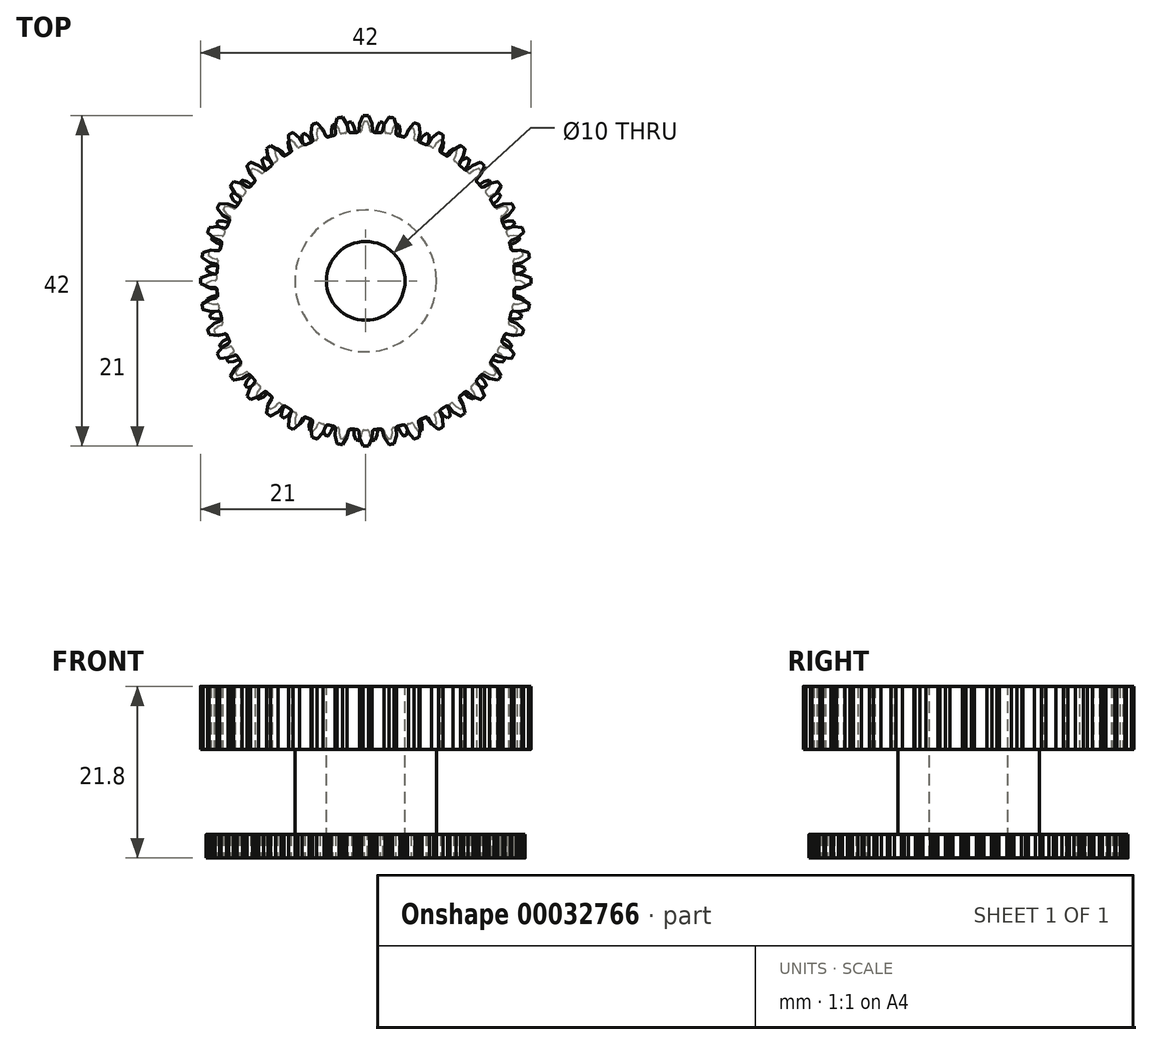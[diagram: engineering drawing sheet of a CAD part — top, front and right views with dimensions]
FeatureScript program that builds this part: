
annotation { "Feature Type Name" : "Feature", "Feature Type Description" : "" }
export const myFeature = defineFeature(function(context is Context, id is Id, definition is map)
    precondition{}
    {
        {
            var Q0;
            Q0=qCreatedBy(makeId("Top.planeOp"),FACE);
            var sketch = newSketch(context, id + "F0", { "sketchPlane" : qUnion([Q0])});
            skArc(sketch, "E0", {"start": v(31.82, 1.48) * mm, "mid": v(31.63, 1.37) * mm, "end": v(31.56, 1.16) * mm});
            skLineSegment(sketch, "E1", {"start": v(31.82, 1.48) * mm, "end": v(32.69, 1.63) * mm});
            skLineSegment(sketch, "E2", {"start": v(32.69, 1.63) * mm, "end": v(33.7, 2.16) * mm});
            skArc(sketch, "E3", {"start": v(31.39, 3.53) * mm, "mid": v(31.34, 3.91) * mm, "end": v(31.29, 4.3) * mm});
            skArc(sketch, "E4", {"start": v(31.81, -1.7) * mm, "mid": v(31.61, -1.79) * mm, "end": v(31.52, -1.99) * mm});
            skArc(sketch, "E5", {"start": v(31.52, 4.64) * mm, "mid": v(31.34, 4.51) * mm, "end": v(31.29, 4.3) * mm});
            skLineSegment(sketch, "E6", {"start": v(31.81, -1.7) * mm, "end": v(32.69, -1.63) * mm});
            skLineSegment(sketch, "E7", {"start": v(31.52, 4.64) * mm, "end": v(32.36, 4.88) * mm});
            skLineSegment(sketch, "E8", {"start": v(32.69, -1.63) * mm, "end": v(33.75, -1.2) * mm});
            skLineSegment(sketch, "E9", {"start": v(32.36, 4.88) * mm, "end": v(33.31, 5.5) * mm});
            skArc(sketch, "E10", {"start": v(30.88, 6.64) * mm, "mid": v(30.8, 7.02) * mm, "end": v(30.7, 7.4) * mm});
            skArc(sketch, "E11", {"start": v(31.49, -4.85) * mm, "mid": v(31.28, -4.93) * mm, "end": v(31.17, -5.12) * mm});
            skArc(sketch, "E12", {"start": v(30.9, 7.76) * mm, "mid": v(30.73, 7.61) * mm, "end": v(30.7, 7.4) * mm});
            skLineSegment(sketch, "E13", {"start": v(31.49, -4.85) * mm, "end": v(32.36, -4.88) * mm});
            skLineSegment(sketch, "E14", {"start": v(30.9, 7.76) * mm, "end": v(31.71, 8.07) * mm});
            skLineSegment(sketch, "E15", {"start": v(32.36, -4.88) * mm, "end": v(33.46, -4.56) * mm});
            skLineSegment(sketch, "E16", {"start": v(31.71, 8.07) * mm, "end": v(32.6, 8.8) * mm});
            skArc(sketch, "E17", {"start": v(30.06, 9.68) * mm, "mid": v(29.94, 10.05) * mm, "end": v(29.81, 10.41) * mm});
            skArc(sketch, "E18", {"start": v(30.85, -7.97) * mm, "mid": v(30.64, -8.02) * mm, "end": v(30.5, -8.2) * mm});
            skArc(sketch, "E19", {"start": v(29.97, 10.8) * mm, "mid": v(29.82, 10.63) * mm, "end": v(29.81, 10.41) * mm});
            skLineSegment(sketch, "E20", {"start": v(30.85, -7.97) * mm, "end": v(31.72, -8.08) * mm});
            skLineSegment(sketch, "E21", {"start": v(29.97, 10.8) * mm, "end": v(30.75, 11.2) * mm});
            skLineSegment(sketch, "E22", {"start": v(31.72, -8.08) * mm, "end": v(32.84, -7.86) * mm});
            skLineSegment(sketch, "E23", {"start": v(30.75, 11.2) * mm, "end": v(31.56, 12) * mm});
            skArc(sketch, "E24", {"start": v(28.95, 12.62) * mm, "mid": v(28.8, 12.98) * mm, "end": v(28.63, 13.33) * mm});
            skArc(sketch, "E25", {"start": v(29.9, -11) * mm, "mid": v(29.69, -11.03) * mm, "end": v(29.54, -11.2) * mm});
            skArc(sketch, "E26", {"start": v(28.74, 13.72) * mm, "mid": v(28.61, 13.55) * mm, "end": v(28.63, 13.33) * mm});
            skLineSegment(sketch, "E27", {"start": v(29.9, -11) * mm, "end": v(30.76, -11.2) * mm});
            skLineSegment(sketch, "E28", {"start": v(28.74, 13.72) * mm, "end": v(29.48, 14.2) * mm});
            skLineSegment(sketch, "E29", {"start": v(30.76, -11.2) * mm, "end": v(31.9, -11.1) * mm});
            skLineSegment(sketch, "E30", {"start": v(29.48, 14.2) * mm, "end": v(30.2, 15.08) * mm});
            skArc(sketch, "E31", {"start": v(27.55, 15.44) * mm, "mid": v(27.35, 15.78) * mm, "end": v(27.16, 16.11) * mm});
            skArc(sketch, "E32", {"start": v(28.66, -13.92) * mm, "mid": v(28.44, -13.93) * mm, "end": v(28.28, -14.08) * mm});
            skArc(sketch, "E33", {"start": v(27.23, 16.52) * mm, "mid": v(27.12, 16.33) * mm, "end": v(27.16, 16.11) * mm});
            skLineSegment(sketch, "E34", {"start": v(28.66, -13.92) * mm, "end": v(29.5, -14.2) * mm});
            skLineSegment(sketch, "E35", {"start": v(27.23, 16.52) * mm, "end": v(27.92, 17.06) * mm});
            skLineSegment(sketch, "E36", {"start": v(29.5, -14.2) * mm, "end": v(30.64, -14.22) * mm});
            skLineSegment(sketch, "E37", {"start": v(27.92, 17.06) * mm, "end": v(28.55, 18.02) * mm});
            skArc(sketch, "E38", {"start": v(25.87, 18.1) * mm, "mid": v(25.65, 18.42) * mm, "end": v(25.42, 18.74) * mm});
            skArc(sketch, "E39", {"start": v(27.13, -16.7) * mm, "mid": v(26.92, -16.69) * mm, "end": v(26.74, -16.82) * mm});
            skArc(sketch, "E40", {"start": v(25.45, 19.15) * mm, "mid": v(25.36, 18.95) * mm, "end": v(25.42, 18.74) * mm});
            skLineSegment(sketch, "E41", {"start": v(27.13, -16.7) * mm, "end": v(27.93, -17.07) * mm});
            skLineSegment(sketch, "E42", {"start": v(25.45, 19.15) * mm, "end": v(26.08, 19.76) * mm});
            skLineSegment(sketch, "E43", {"start": v(27.93, -17.07) * mm, "end": v(29.07, -17.2) * mm});
            skLineSegment(sketch, "E44", {"start": v(26.08, 19.76) * mm, "end": v(26.62, 20.77) * mm});
            skArc(sketch, "E45", {"start": v(23.94, 20.6) * mm, "mid": v(23.68, 20.89) * mm, "end": v(23.42, 21.18) * mm});
            skArc(sketch, "E46", {"start": v(25.34, -19.32) * mm, "mid": v(25.12, -19.29) * mm, "end": v(24.93, -19.4) * mm});
            skArc(sketch, "E47", {"start": v(23.42, 21.59) * mm, "mid": v(23.34, 21.38) * mm, "end": v(23.42, 21.18) * mm});
            skLineSegment(sketch, "E48", {"start": v(25.34, -19.32) * mm, "end": v(26.1, -19.77) * mm});
            skLineSegment(sketch, "E49", {"start": v(23.42, 21.59) * mm, "end": v(23.98, 22.26) * mm});
            skLineSegment(sketch, "E50", {"start": v(26.1, -19.77) * mm, "end": v(27.21, -20) * mm});
            skLineSegment(sketch, "E51", {"start": v(23.98, 22.26) * mm, "end": v(24.41, 23.32) * mm});
            skArc(sketch, "E52", {"start": v(21.77, 22.88) * mm, "mid": v(21.48, 23.14) * mm, "end": v(21.2, 23.4) * mm});
            skArc(sketch, "E53", {"start": v(23.29, -21.75) * mm, "mid": v(23.08, -21.7) * mm, "end": v(22.88, -21.79) * mm});
            skArc(sketch, "E54", {"start": v(21.15, 23.81) * mm, "mid": v(21.1, 23.6) * mm, "end": v(21.2, 23.4) * mm});
            skLineSegment(sketch, "E55", {"start": v(23.29, -21.75) * mm, "end": v(24, -22.27) * mm});
            skLineSegment(sketch, "E56", {"start": v(21.15, 23.81) * mm, "end": v(21.65, 24.53) * mm});
            skLineSegment(sketch, "E57", {"start": v(24, -22.27) * mm, "end": v(25.09, -22.62) * mm});
            skLineSegment(sketch, "E58", {"start": v(21.65, 24.53) * mm, "end": v(21.97, 25.63) * mm});
            skArc(sketch, "E59", {"start": v(19.38, 24.93) * mm, "mid": v(19.07, 25.16) * mm, "end": v(18.76, 25.4) * mm});
            skArc(sketch, "E60", {"start": v(21, -23.96) * mm, "mid": v(20.8, -23.88) * mm, "end": v(20.6, -23.96) * mm});
            skArc(sketch, "E61", {"start": v(18.67, 25.8) * mm, "mid": v(18.64, 25.58) * mm, "end": v(18.76, 25.4) * mm});
            skLineSegment(sketch, "E62", {"start": v(21, -23.96) * mm, "end": v(21.66, -24.55) * mm});
            skLineSegment(sketch, "E63", {"start": v(18.67, 25.8) * mm, "end": v(19.1, 26.57) * mm});
            skLineSegment(sketch, "E64", {"start": v(21.66, -24.55) * mm, "end": v(22.71, -25) * mm});
            skLineSegment(sketch, "E65", {"start": v(19.1, 26.57) * mm, "end": v(19.3, 27.7) * mm});
            skArc(sketch, "E66", {"start": v(16.8, 26.73) * mm, "mid": v(16.47, 26.94) * mm, "end": v(16.14, 27.14) * mm});
            skArc(sketch, "E67", {"start": v(18.52, -25.93) * mm, "mid": v(18.32, -25.84) * mm, "end": v(18.11, -25.89) * mm});
            skArc(sketch, "E68", {"start": v(16.01, 27.53) * mm, "mid": v(16, 27.3) * mm, "end": v(16.14, 27.14) * mm});
            skLineSegment(sketch, "E69", {"start": v(18.52, -25.93) * mm, "end": v(19.11, -26.58) * mm});
            skLineSegment(sketch, "E70", {"start": v(16.01, 27.53) * mm, "end": v(16.35, 28.34) * mm});
            skLineSegment(sketch, "E71", {"start": v(19.11, -26.58) * mm, "end": v(20.11, -27.14) * mm});
            skLineSegment(sketch, "E72", {"start": v(16.35, 28.34) * mm, "end": v(16.45, 29.47) * mm});
            skArc(sketch, "E73", {"start": v(14.05, 28.27) * mm, "mid": v(13.7, 28.44) * mm, "end": v(13.35, 28.61) * mm});
            skArc(sketch, "E74", {"start": v(15.85, -27.65) * mm, "mid": v(15.66, -27.53) * mm, "end": v(15.45, -27.56) * mm});
            skArc(sketch, "E75", {"start": v(13.19, 28.99) * mm, "mid": v(13.2, 28.77) * mm, "end": v(13.35, 28.61) * mm});
            skLineSegment(sketch, "E76", {"start": v(15.85, -27.65) * mm, "end": v(16.37, -28.35) * mm});
            skLineSegment(sketch, "E77", {"start": v(13.19, 28.99) * mm, "end": v(13.45, 29.82) * mm});
            skLineSegment(sketch, "E78", {"start": v(16.37, -28.35) * mm, "end": v(17.31, -29) * mm});
            skLineSegment(sketch, "E79", {"start": v(13.45, 29.82) * mm, "end": v(13.44, 30.97) * mm});
            skArc(sketch, "E80", {"start": v(11.17, 29.53) * mm, "mid": v(10.8, 29.67) * mm, "end": v(10.44, 29.8) * mm});
            skArc(sketch, "E81", {"start": v(13.02, -29.1) * mm, "mid": v(12.84, -28.95) * mm, "end": v(12.63, -28.97) * mm});
            skArc(sketch, "E82", {"start": v(10.24, 30.16) * mm, "mid": v(10.27, 29.94) * mm, "end": v(10.44, 29.8) * mm});
            skLineSegment(sketch, "E83", {"start": v(13.02, -29.1) * mm, "end": v(13.47, -29.84) * mm});
            skLineSegment(sketch, "E84", {"start": v(10.24, 30.16) * mm, "end": v(10.41, 31.01) * mm});
            skLineSegment(sketch, "E85", {"start": v(13.47, -29.84) * mm, "end": v(14.34, -30.59) * mm});
            skLineSegment(sketch, "E86", {"start": v(10.41, 31.01) * mm, "end": v(10.28, 32.15) * mm});
            skArc(sketch, "E87", {"start": v(8.17, 30.5) * mm, "mid": v(7.8, 30.6) * mm, "end": v(7.42, 30.69) * mm});
            skArc(sketch, "E88", {"start": v(10.06, -30.24) * mm, "mid": v(9.9, -30.09) * mm, "end": v(9.68, -30.08) * mm});
            skArc(sketch, "E89", {"start": v(7.18, 31.02) * mm, "mid": v(7.24, 30.81) * mm, "end": v(7.42, 30.69) * mm});
            skLineSegment(sketch, "E90", {"start": v(10.06, -30.24) * mm, "end": v(10.43, -31.03) * mm});
            skLineSegment(sketch, "E91", {"start": v(7.18, 31.02) * mm, "end": v(7.27, 31.9) * mm});
            skLineSegment(sketch, "E92", {"start": v(10.43, -31.03) * mm, "end": v(11.22, -31.86) * mm});
            skLineSegment(sketch, "E93", {"start": v(7.27, 31.9) * mm, "end": v(7.03, 33.01) * mm});
            skArc(sketch, "E94", {"start": v(5.1, 31.16) * mm, "mid": v(4.7, 31.22) * mm, "end": v(4.32, 31.27) * mm});
            skArc(sketch, "E95", {"start": v(7, -31.1) * mm, "mid": v(6.86, -30.93) * mm, "end": v(6.64, -30.9) * mm});
            skArc(sketch, "E96", {"start": v(4.05, 31.59) * mm, "mid": v(4.13, 31.38) * mm, "end": v(4.32, 31.27) * mm});
            skLineSegment(sketch, "E97", {"start": v(7, -31.1) * mm, "end": v(7.3, -31.92) * mm});
            skLineSegment(sketch, "E98", {"start": v(4.05, 31.59) * mm, "end": v(4.06, 32.46) * mm});
            skLineSegment(sketch, "E99", {"start": v(7.3, -31.92) * mm, "end": v(8, -32.82) * mm});
            skLineSegment(sketch, "E100", {"start": v(4.06, 32.46) * mm, "end": v(3.7, 33.55) * mm});
            skArc(sketch, "E101", {"start": v(1.96, 31.51) * mm, "mid": v(1.57, 31.53) * mm, "end": v(1.19, 31.55) * mm});
            skArc(sketch, "E102", {"start": v(3.87, -31.64) * mm, "mid": v(3.74, -31.45) * mm, "end": v(3.53, -31.4) * mm});
            skArc(sketch, "E103", {"start": v(0.89, 31.83) * mm, "mid": v(0.98, 31.63) * mm, "end": v(1.19, 31.55) * mm});
            skLineSegment(sketch, "E104", {"start": v(3.87, -31.64) * mm, "end": v(4.08, -32.49) * mm});
            skLineSegment(sketch, "E105", {"start": v(0.89, 31.83) * mm, "end": v(0.8, 32.7) * mm});
            skLineSegment(sketch, "E106", {"start": v(4.08, -32.49) * mm, "end": v(4.69, -33.45) * mm});
            skLineSegment(sketch, "E107", {"start": v(0.8, 32.7) * mm, "end": v(0.35, 33.75) * mm});
            skArc(sketch, "E108", {"start": v(-1.19, 31.55) * mm, "mid": v(-1.57, 31.53) * mm, "end": v(-1.96, 31.51) * mm});
            skArc(sketch, "E109", {"start": v(0.7, -31.86) * mm, "mid": v(0.6, -31.67) * mm, "end": v(0.39, -31.6) * mm});
            skArc(sketch, "E110", {"start": v(-2.29, 31.76) * mm, "mid": v(-2.17, 31.58) * mm, "end": v(-1.96, 31.51) * mm});
            skLineSegment(sketch, "E111", {"start": v(0.7, -31.86) * mm, "end": v(0.83, -32.73) * mm});
            skLineSegment(sketch, "E112", {"start": v(-2.29, 31.76) * mm, "end": v(-2.46, 32.62) * mm});
            skLineSegment(sketch, "E113", {"start": v(0.83, -32.73) * mm, "end": v(1.34, -33.75) * mm});
            skLineSegment(sketch, "E114", {"start": v(-2.46, 32.62) * mm, "end": v(-3.02, 33.62) * mm});
            skArc(sketch, "E115", {"start": v(-4.32, 31.27) * mm, "mid": v(-4.7, 31.22) * mm, "end": v(-5.1, 31.16) * mm});
            skArc(sketch, "E116", {"start": v(-2.47, -31.77) * mm, "mid": v(-2.56, -31.57) * mm, "end": v(-2.76, -31.48) * mm});
            skArc(sketch, "E117", {"start": v(-5.44, 31.38) * mm, "mid": v(-5.3, 31.2) * mm, "end": v(-5.1, 31.16) * mm});
            skLineSegment(sketch, "E118", {"start": v(-2.47, -31.77) * mm, "end": v(-2.44, -32.65) * mm});
            skLineSegment(sketch, "E119", {"start": v(-5.44, 31.38) * mm, "end": v(-5.7, 32.22) * mm});
            skLineSegment(sketch, "E120", {"start": v(-2.44, -32.65) * mm, "end": v(-2.03, -33.72) * mm});
            skLineSegment(sketch, "E121", {"start": v(-5.7, 32.22) * mm, "end": v(-6.35, 33.15) * mm});
            skArc(sketch, "E122", {"start": v(-7.42, 30.69) * mm, "mid": v(-7.8, 30.6) * mm, "end": v(-8.17, 30.5) * mm});
            skArc(sketch, "E123", {"start": v(-5.62, -31.37) * mm, "mid": v(-5.7, -31.16) * mm, "end": v(-5.88, -31.05) * mm});
            skArc(sketch, "E124", {"start": v(-8.54, 30.68) * mm, "mid": v(-8.39, 30.52) * mm, "end": v(-8.17, 30.5) * mm});
            skLineSegment(sketch, "E125", {"start": v(-5.62, -31.37) * mm, "end": v(-5.67, -32.25) * mm});
            skLineSegment(sketch, "E126", {"start": v(-8.54, 30.68) * mm, "end": v(-8.87, 31.49) * mm});
            skLineSegment(sketch, "E127", {"start": v(-5.67, -32.25) * mm, "end": v(-5.38, -33.35) * mm});
            skLineSegment(sketch, "E128", {"start": v(-8.87, 31.49) * mm, "end": v(-9.62, 32.35) * mm});
            skArc(sketch, "E129", {"start": v(-10.44, 29.8) * mm, "mid": v(-10.8, 29.67) * mm, "end": v(-11.17, 29.53) * mm});
            skArc(sketch, "E130", {"start": v(-8.72, -30.65) * mm, "mid": v(-8.76, -30.44) * mm, "end": v(-8.94, -30.3) * mm});
            skArc(sketch, "E131", {"start": v(-11.55, 29.68) * mm, "mid": v(-11.39, 29.53) * mm, "end": v(-11.17, 29.53) * mm});
            skLineSegment(sketch, "E132", {"start": v(-8.72, -30.65) * mm, "end": v(-8.85, -31.52) * mm});
            skLineSegment(sketch, "E133", {"start": v(-11.55, 29.68) * mm, "end": v(-11.97, 30.45) * mm});
            skLineSegment(sketch, "E134", {"start": v(-8.85, -31.52) * mm, "end": v(-8.67, -32.65) * mm});
            skLineSegment(sketch, "E135", {"start": v(-11.97, 30.45) * mm, "end": v(-12.8, 31.24) * mm});
            skArc(sketch, "E136", {"start": v(-13.35, 28.61) * mm, "mid": v(-13.7, 28.44) * mm, "end": v(-14.05, 28.27) * mm});
            skArc(sketch, "E137", {"start": v(-11.73, -29.63) * mm, "mid": v(-11.75, -29.42) * mm, "end": v(-11.91, -29.27) * mm});
            skArc(sketch, "E138", {"start": v(-14.45, 28.38) * mm, "mid": v(-14.27, 28.25) * mm, "end": v(-14.05, 28.27) * mm});
            skLineSegment(sketch, "E139", {"start": v(-11.73, -29.63) * mm, "end": v(-11.95, -30.48) * mm});
            skLineSegment(sketch, "E140", {"start": v(-14.45, 28.38) * mm, "end": v(-14.94, 29.1) * mm});
            skLineSegment(sketch, "E141", {"start": v(-11.95, -30.48) * mm, "end": v(-11.87, -31.62) * mm});
            skLineSegment(sketch, "E142", {"start": v(-14.94, 29.1) * mm, "end": v(-15.84, 29.8) * mm});
            skArc(sketch, "E143", {"start": v(-16.14, 27.14) * mm, "mid": v(-16.47, 26.94) * mm, "end": v(-16.8, 26.73) * mm});
            skArc(sketch, "E144", {"start": v(-14.62, -28.32) * mm, "mid": v(-14.62, -28.1) * mm, "end": v(-14.76, -27.94) * mm});
            skArc(sketch, "E145", {"start": v(-17.2, 26.8) * mm, "mid": v(-17.01, 26.7) * mm, "end": v(-16.8, 26.73) * mm});
            skLineSegment(sketch, "E146", {"start": v(-14.62, -28.32) * mm, "end": v(-14.92, -29.14) * mm});
            skLineSegment(sketch, "E147", {"start": v(-17.2, 26.8) * mm, "end": v(-17.77, 27.47) * mm});
            skLineSegment(sketch, "E148", {"start": v(-14.92, -29.14) * mm, "end": v(-14.96, -30.28) * mm});
            skLineSegment(sketch, "E149", {"start": v(-17.77, 27.47) * mm, "end": v(-18.73, 28.08) * mm});
            skArc(sketch, "E150", {"start": v(-18.76, 25.4) * mm, "mid": v(-19.07, 25.16) * mm, "end": v(-19.38, 24.93) * mm});
            skArc(sketch, "E151", {"start": v(-17.36, -26.72) * mm, "mid": v(-17.34, -26.5) * mm, "end": v(-17.47, -26.33) * mm});
            skArc(sketch, "E152", {"start": v(-19.79, 24.95) * mm, "mid": v(-19.59, 24.86) * mm, "end": v(-19.38, 24.93) * mm});
            skLineSegment(sketch, "E153", {"start": v(-17.36, -26.72) * mm, "end": v(-17.75, -27.51) * mm});
            skLineSegment(sketch, "E154", {"start": v(-19.79, 24.95) * mm, "end": v(-20.41, 25.57) * mm});
            skLineSegment(sketch, "E155", {"start": v(-17.75, -27.51) * mm, "end": v(-17.9, -28.64) * mm});
            skLineSegment(sketch, "E156", {"start": v(-20.41, 25.57) * mm, "end": v(-21.44, 26.08) * mm});
            skArc(sketch, "E157", {"start": v(-21.2, 23.4) * mm, "mid": v(-21.48, 23.14) * mm, "end": v(-21.77, 22.88) * mm});
            skArc(sketch, "E158", {"start": v(-19.94, -24.86) * mm, "mid": v(-19.9, -24.65) * mm, "end": v(-20, -24.46) * mm});
            skArc(sketch, "E159", {"start": v(-22.18, 22.86) * mm, "mid": v(-21.97, 22.79) * mm, "end": v(-21.77, 22.88) * mm});
            skLineSegment(sketch, "E160", {"start": v(-19.94, -24.86) * mm, "end": v(-20.4, -25.6) * mm});
            skLineSegment(sketch, "E161", {"start": v(-22.18, 22.86) * mm, "end": v(-22.86, 23.4) * mm});
            skLineSegment(sketch, "E162", {"start": v(-20.4, -25.6) * mm, "end": v(-20.66, -26.72) * mm});
            skLineSegment(sketch, "E163", {"start": v(-22.86, 23.4) * mm, "end": v(-23.93, 23.81) * mm});
            skArc(sketch, "E164", {"start": v(-23.42, 21.18) * mm, "mid": v(-23.68, 20.89) * mm, "end": v(-23.94, 20.6) * mm});
            skArc(sketch, "E165", {"start": v(-22.31, -22.75) * mm, "mid": v(-22.25, -22.54) * mm, "end": v(-22.34, -22.34) * mm});
            skArc(sketch, "E166", {"start": v(-24.34, 20.54) * mm, "mid": v(-24.13, 20.49) * mm, "end": v(-23.94, 20.6) * mm});
            skLineSegment(sketch, "E167", {"start": v(-22.31, -22.75) * mm, "end": v(-22.84, -23.45) * mm});
            skLineSegment(sketch, "E168", {"start": v(-24.34, 20.54) * mm, "end": v(-25.08, 21.02) * mm});
            skLineSegment(sketch, "E169", {"start": v(-22.84, -23.45) * mm, "end": v(-23.22, -24.53) * mm});
            skLineSegment(sketch, "E170", {"start": v(-25.08, 21.02) * mm, "end": v(-26.18, 21.31) * mm});
            skArc(sketch, "E171", {"start": v(-25.42, 18.74) * mm, "mid": v(-25.65, 18.42) * mm, "end": v(-25.87, 18.1) * mm});
            skArc(sketch, "E172", {"start": v(-24.46, -20.42) * mm, "mid": v(-24.38, -20.22) * mm, "end": v(-24.45, -20) * mm});
            skArc(sketch, "E173", {"start": v(-26.27, 18.01) * mm, "mid": v(-26.05, 17.98) * mm, "end": v(-25.87, 18.1) * mm});
            skLineSegment(sketch, "E174", {"start": v(-24.46, -20.42) * mm, "end": v(-25.06, -21.06) * mm});
            skLineSegment(sketch, "E175", {"start": v(-26.27, 18.01) * mm, "end": v(-27.05, 18.41) * mm});
            skLineSegment(sketch, "E176", {"start": v(-25.06, -21.06) * mm, "end": v(-25.55, -22.1) * mm});
            skLineSegment(sketch, "E177", {"start": v(-27.05, 18.41) * mm, "end": v(-28.18, 18.6) * mm});
            skArc(sketch, "E178", {"start": v(-27.16, 16.11) * mm, "mid": v(-27.35, 15.78) * mm, "end": v(-27.55, 15.44) * mm});
            skArc(sketch, "E179", {"start": v(-26.37, -17.88) * mm, "mid": v(-26.27, -17.69) * mm, "end": v(-26.32, -17.47) * mm});
            skArc(sketch, "E180", {"start": v(-27.93, 15.3) * mm, "mid": v(-27.71, 15.3) * mm, "end": v(-27.55, 15.44) * mm});
            skLineSegment(sketch, "E181", {"start": v(-26.37, -17.88) * mm, "end": v(-27.04, -18.46) * mm});
            skLineSegment(sketch, "E182", {"start": v(-27.93, 15.3) * mm, "end": v(-28.75, 15.63) * mm});
            skLineSegment(sketch, "E183", {"start": v(-27.04, -18.46) * mm, "end": v(-27.62, -19.44) * mm});
            skLineSegment(sketch, "E184", {"start": v(-28.75, 15.63) * mm, "end": v(-29.89, 15.7) * mm});
            skArc(sketch, "E185", {"start": v(-28.63, 13.33) * mm, "mid": v(-28.8, 12.98) * mm, "end": v(-28.95, 12.62) * mm});
            skArc(sketch, "E186", {"start": v(-28.02, -15.17) * mm, "mid": v(-27.9, -14.98) * mm, "end": v(-27.93, -14.77) * mm});
            skArc(sketch, "E187", {"start": v(-29.32, 12.45) * mm, "mid": v(-29.1, 12.47) * mm, "end": v(-28.95, 12.62) * mm});
            skLineSegment(sketch, "E188", {"start": v(-28.02, -15.17) * mm, "end": v(-28.74, -15.68) * mm});
            skLineSegment(sketch, "E189", {"start": v(-29.32, 12.45) * mm, "end": v(-30.16, 12.69) * mm});
            skLineSegment(sketch, "E190", {"start": v(-28.74, -15.68) * mm, "end": v(-29.42, -16.6) * mm});
            skLineSegment(sketch, "E191", {"start": v(-30.16, 12.69) * mm, "end": v(-31.3, 12.65) * mm});
            skArc(sketch, "E192", {"start": v(-29.82, 10.41) * mm, "mid": v(-29.94, 10.05) * mm, "end": v(-30.06, 9.68) * mm});
            skArc(sketch, "E193", {"start": v(-29.4, -12.3) * mm, "mid": v(-29.25, -12.13) * mm, "end": v(-29.26, -11.91) * mm});
            skArc(sketch, "E194", {"start": v(-30.41, 9.47) * mm, "mid": v(-30.2, 9.5) * mm, "end": v(-30.06, 9.68) * mm});
            skLineSegment(sketch, "E195", {"start": v(-29.4, -12.3) * mm, "end": v(-30.15, -12.74) * mm});
            skLineSegment(sketch, "E196", {"start": v(-30.41, 9.47) * mm, "end": v(-31.28, 9.62) * mm});
            skLineSegment(sketch, "E197", {"start": v(-30.15, -12.74) * mm, "end": v(-30.92, -13.58) * mm});
            skLineSegment(sketch, "E198", {"start": v(-31.28, 9.62) * mm, "end": v(-32.4, 9.47) * mm});
            skArc(sketch, "E199", {"start": v(-30.7, 7.4) * mm, "mid": v(-30.8, 7.02) * mm, "end": v(-30.88, 6.64) * mm});
            skArc(sketch, "E200", {"start": v(-30.47, -9.31) * mm, "mid": v(-30.31, -9.16) * mm, "end": v(-30.3, -8.94) * mm});
            skArc(sketch, "E201", {"start": v(-31.2, 6.4) * mm, "mid": v(-31, 6.45) * mm, "end": v(-30.88, 6.64) * mm});
            skLineSegment(sketch, "E202", {"start": v(-30.47, -9.31) * mm, "end": v(-31.27, -9.67) * mm});
            skLineSegment(sketch, "E203", {"start": v(-31.2, 6.4) * mm, "end": v(-32.08, 6.46) * mm});
            skLineSegment(sketch, "E204", {"start": v(-31.27, -9.67) * mm, "end": v(-32.12, -10.44) * mm});
            skLineSegment(sketch, "E205", {"start": v(-32.08, 6.46) * mm, "end": v(-33.2, 6.2) * mm});
            skArc(sketch, "E206", {"start": v(-31.29, 4.3) * mm, "mid": v(-31.34, 3.91) * mm, "end": v(-31.39, 3.53) * mm});
            skArc(sketch, "E207", {"start": v(-31.24, -6.23) * mm, "mid": v(-31.07, -6.1) * mm, "end": v(-31.04, -5.88) * mm});
            skArc(sketch, "E208", {"start": v(-31.69, 3.25) * mm, "mid": v(-31.49, 3.33) * mm, "end": v(-31.39, 3.53) * mm});
            skLineSegment(sketch, "E209", {"start": v(-31.24, -6.23) * mm, "end": v(-32.08, -6.5) * mm});
            skLineSegment(sketch, "E210", {"start": v(-31.69, 3.25) * mm, "end": v(-32.57, 3.23) * mm});
            skLineSegment(sketch, "E211", {"start": v(-32.08, -6.5) * mm, "end": v(-33, -7.19) * mm});
            skLineSegment(sketch, "E212", {"start": v(-32.57, 3.23) * mm, "end": v(-33.65, 2.86) * mm});
            skArc(sketch, "E213", {"start": v(-31.7, -3.1) * mm, "mid": v(-31.52, -2.97) * mm, "end": v(-31.47, -2.76) * mm});
            skArc(sketch, "E214", {"start": v(-31.56, 1.16) * mm, "mid": v(-31.58, 0.77) * mm, "end": v(-31.58, 0.39) * mm});
            skLineSegment(sketch, "E215", {"start": v(-31.7, -3.1) * mm, "end": v(-32.56, -3.28) * mm});
            skArc(sketch, "E216", {"start": v(-31.86, 0.08) * mm, "mid": v(-31.66, 0.18) * mm, "end": v(-31.58, 0.39) * mm});
            skLineSegment(sketch, "E217", {"start": v(-32.56, -3.28) * mm, "end": v(-33.55, -3.87) * mm});
            skLineSegment(sketch, "E218", {"start": v(-31.86, 0.08) * mm, "end": v(-32.73, -0.02) * mm});
            skLineSegment(sketch, "E219", {"start": v(-32.73, -0.02) * mm, "end": v(-33.76, -0.5) * mm});
            skLineSegment(sketch, "E220", {"start": v(-33.75, -1.2) * mm, "end": v(-32.69, -1.63) * mm});
            skLineSegment(sketch, "E221", {"start": v(-32.69, -1.63) * mm, "end": v(-31.81, -1.7) * mm});
            skArc(sketch, "E222", {"start": v(-31.52, -1.99) * mm, "mid": v(-31.61, -1.79) * mm, "end": v(-31.81, -1.7) * mm});
            skArc(sketch, "E223", {"start": v(-31.52, -1.99) * mm, "mid": v(-31.5, -2.37) * mm, "end": v(-31.47, -2.76) * mm});
            skLineSegment(sketch, "E224", {"start": v(-33.46, -4.56) * mm, "end": v(-32.36, -4.88) * mm});
            skLineSegment(sketch, "E225", {"start": v(-32.36, -4.88) * mm, "end": v(-31.49, -4.85) * mm});
            skArc(sketch, "E226", {"start": v(-31.17, -5.12) * mm, "mid": v(-31.28, -4.93) * mm, "end": v(-31.49, -4.85) * mm});
            skArc(sketch, "E227", {"start": v(-31.17, -5.12) * mm, "mid": v(-31.1, -5.5) * mm, "end": v(-31.04, -5.88) * mm});
            skLineSegment(sketch, "E228", {"start": v(-32.84, -7.86) * mm, "end": v(-31.72, -8.08) * mm});
            skLineSegment(sketch, "E229", {"start": v(-31.72, -8.08) * mm, "end": v(-30.85, -7.97) * mm});
            skArc(sketch, "E230", {"start": v(-30.5, -8.2) * mm, "mid": v(-30.64, -8.02) * mm, "end": v(-30.85, -7.97) * mm});
            skArc(sketch, "E231", {"start": v(-30.5, -8.2) * mm, "mid": v(-30.4, -8.57) * mm, "end": v(-30.3, -8.94) * mm});
            skLineSegment(sketch, "E232", {"start": v(-31.9, -11.1) * mm, "end": v(-30.76, -11.2) * mm});
            skLineSegment(sketch, "E233", {"start": v(-30.76, -11.2) * mm, "end": v(-29.9, -11) * mm});
            skArc(sketch, "E234", {"start": v(-29.54, -11.2) * mm, "mid": v(-29.69, -11.03) * mm, "end": v(-29.9, -11) * mm});
            skArc(sketch, "E235", {"start": v(-29.54, -11.2) * mm, "mid": v(-29.4, -11.55) * mm, "end": v(-29.26, -11.91) * mm});
            skLineSegment(sketch, "E236", {"start": v(-30.64, -14.22) * mm, "end": v(-29.5, -14.2) * mm});
            skLineSegment(sketch, "E237", {"start": v(-29.5, -14.2) * mm, "end": v(-28.66, -13.92) * mm});
            skArc(sketch, "E238", {"start": v(-28.28, -14.08) * mm, "mid": v(-28.44, -13.93) * mm, "end": v(-28.66, -13.92) * mm});
            skArc(sketch, "E239", {"start": v(-28.28, -14.08) * mm, "mid": v(-28.1, -14.42) * mm, "end": v(-27.93, -14.77) * mm});
            skLineSegment(sketch, "E240", {"start": v(-29.07, -17.2) * mm, "end": v(-27.93, -17.07) * mm});
            skLineSegment(sketch, "E241", {"start": v(-27.93, -17.07) * mm, "end": v(-27.13, -16.7) * mm});
            skArc(sketch, "E242", {"start": v(-26.74, -16.82) * mm, "mid": v(-26.92, -16.69) * mm, "end": v(-27.13, -16.7) * mm});
            skArc(sketch, "E243", {"start": v(-26.74, -16.82) * mm, "mid": v(-26.53, -17.15) * mm, "end": v(-26.32, -17.47) * mm});
            skLineSegment(sketch, "E244", {"start": v(-27.21, -20) * mm, "end": v(-26.1, -19.77) * mm});
            skLineSegment(sketch, "E245", {"start": v(-26.1, -19.77) * mm, "end": v(-25.34, -19.32) * mm});
            skArc(sketch, "E246", {"start": v(-24.93, -19.4) * mm, "mid": v(-25.12, -19.29) * mm, "end": v(-25.34, -19.32) * mm});
            skArc(sketch, "E247", {"start": v(-24.93, -19.4) * mm, "mid": v(-24.7, -19.7) * mm, "end": v(-24.45, -20) * mm});
            skLineSegment(sketch, "E248", {"start": v(-25.09, -22.62) * mm, "end": v(-24, -22.27) * mm});
            skLineSegment(sketch, "E249", {"start": v(-24, -22.27) * mm, "end": v(-23.29, -21.75) * mm});
            skArc(sketch, "E250", {"start": v(-22.88, -21.79) * mm, "mid": v(-23.08, -21.7) * mm, "end": v(-23.29, -21.75) * mm});
            skArc(sketch, "E251", {"start": v(-22.88, -21.79) * mm, "mid": v(-22.61, -22.07) * mm, "end": v(-22.34, -22.34) * mm});
            skLineSegment(sketch, "E252", {"start": v(-22.71, -25) * mm, "end": v(-21.66, -24.55) * mm});
            skLineSegment(sketch, "E253", {"start": v(-21.66, -24.55) * mm, "end": v(-21, -23.96) * mm});
            skArc(sketch, "E254", {"start": v(-20.6, -23.96) * mm, "mid": v(-20.8, -23.88) * mm, "end": v(-21, -23.96) * mm});
            skArc(sketch, "E255", {"start": v(-20.6, -23.96) * mm, "mid": v(-20.3, -24.2) * mm, "end": v(-20, -24.46) * mm});
            skLineSegment(sketch, "E256", {"start": v(-20.11, -27.14) * mm, "end": v(-19.11, -26.58) * mm});
            skLineSegment(sketch, "E257", {"start": v(-19.11, -26.58) * mm, "end": v(-18.52, -25.93) * mm});
            skArc(sketch, "E258", {"start": v(-18.11, -25.89) * mm, "mid": v(-18.32, -25.84) * mm, "end": v(-18.52, -25.93) * mm});
            skArc(sketch, "E259", {"start": v(-18.11, -25.89) * mm, "mid": v(-17.8, -26.11) * mm, "end": v(-17.47, -26.33) * mm});
            skLineSegment(sketch, "E260", {"start": v(-17.31, -29) * mm, "end": v(-16.37, -28.35) * mm});
            skLineSegment(sketch, "E261", {"start": v(-16.37, -28.35) * mm, "end": v(-15.85, -27.65) * mm});
            skArc(sketch, "E262", {"start": v(-15.45, -27.56) * mm, "mid": v(-15.66, -27.53) * mm, "end": v(-15.85, -27.65) * mm});
            skArc(sketch, "E263", {"start": v(-15.45, -27.56) * mm, "mid": v(-15.1, -27.75) * mm, "end": v(-14.76, -27.94) * mm});
            skLineSegment(sketch, "E264", {"start": v(-14.34, -30.59) * mm, "end": v(-13.47, -29.84) * mm});
            skLineSegment(sketch, "E265", {"start": v(-13.47, -29.84) * mm, "end": v(-13.02, -29.1) * mm});
            skArc(sketch, "E266", {"start": v(-12.63, -28.97) * mm, "mid": v(-12.84, -28.95) * mm, "end": v(-13.02, -29.1) * mm});
            skArc(sketch, "E267", {"start": v(-12.63, -28.97) * mm, "mid": v(-12.27, -29.12) * mm, "end": v(-11.91, -29.27) * mm});
            skLineSegment(sketch, "E268", {"start": v(-11.22, -31.86) * mm, "end": v(-10.43, -31.03) * mm});
            skLineSegment(sketch, "E269", {"start": v(-10.43, -31.03) * mm, "end": v(-10.06, -30.24) * mm});
            skArc(sketch, "E270", {"start": v(-9.68, -30.08) * mm, "mid": v(-9.9, -30.09) * mm, "end": v(-10.06, -30.24) * mm});
            skArc(sketch, "E271", {"start": v(-9.68, -30.08) * mm, "mid": v(-9.3, -30.2) * mm, "end": v(-8.94, -30.3) * mm});
            skLineSegment(sketch, "E272", {"start": v(-8, -32.82) * mm, "end": v(-7.3, -31.92) * mm});
            skLineSegment(sketch, "E273", {"start": v(-7.3, -31.92) * mm, "end": v(-7, -31.1) * mm});
            skArc(sketch, "E274", {"start": v(-6.64, -30.9) * mm, "mid": v(-6.86, -30.93) * mm, "end": v(-7, -31.1) * mm});
            skArc(sketch, "E275", {"start": v(-6.64, -30.9) * mm, "mid": v(-6.26, -30.97) * mm, "end": v(-5.88, -31.05) * mm});
            skLineSegment(sketch, "E276", {"start": v(-4.69, -33.45) * mm, "end": v(-4.08, -32.49) * mm});
            skLineSegment(sketch, "E277", {"start": v(-4.08, -32.49) * mm, "end": v(-3.87, -31.64) * mm});
            skArc(sketch, "E278", {"start": v(-3.53, -31.4) * mm, "mid": v(-3.74, -31.45) * mm, "end": v(-3.87, -31.64) * mm});
            skArc(sketch, "E279", {"start": v(-3.53, -31.4) * mm, "mid": v(-3.14, -31.44) * mm, "end": v(-2.76, -31.48) * mm});
            skLineSegment(sketch, "E280", {"start": v(-1.34, -33.75) * mm, "end": v(-0.83, -32.73) * mm});
            skLineSegment(sketch, "E281", {"start": v(-0.83, -32.73) * mm, "end": v(-0.7, -31.86) * mm});
            skArc(sketch, "E282", {"start": v(-0.39, -31.6) * mm, "mid": v(-0.6, -31.67) * mm, "end": v(-0.7, -31.86) * mm});
            skArc(sketch, "E283", {"start": v(-0.39, -31.6) * mm, "mid": v(0, -31.6) * mm, "end": v(0.39, -31.6) * mm});
            skLineSegment(sketch, "E284", {"start": v(2.03, -33.72) * mm, "end": v(2.44, -32.65) * mm});
            skLineSegment(sketch, "E285", {"start": v(2.44, -32.65) * mm, "end": v(2.47, -31.77) * mm});
            skArc(sketch, "E286", {"start": v(2.76, -31.48) * mm, "mid": v(2.56, -31.57) * mm, "end": v(2.47, -31.77) * mm});
            skArc(sketch, "E287", {"start": v(2.76, -31.48) * mm, "mid": v(3.14, -31.44) * mm, "end": v(3.53, -31.4) * mm});
            skLineSegment(sketch, "E288", {"start": v(5.38, -33.35) * mm, "end": v(5.67, -32.25) * mm});
            skLineSegment(sketch, "E289", {"start": v(5.67, -32.25) * mm, "end": v(5.62, -31.37) * mm});
            skArc(sketch, "E290", {"start": v(5.88, -31.05) * mm, "mid": v(5.7, -31.16) * mm, "end": v(5.62, -31.37) * mm});
            skArc(sketch, "E291", {"start": v(5.88, -31.05) * mm, "mid": v(6.26, -30.97) * mm, "end": v(6.64, -30.9) * mm});
            skLineSegment(sketch, "E292", {"start": v(8.67, -32.65) * mm, "end": v(8.85, -31.52) * mm});
            skLineSegment(sketch, "E293", {"start": v(8.85, -31.52) * mm, "end": v(8.72, -30.65) * mm});
            skArc(sketch, "E294", {"start": v(8.94, -30.3) * mm, "mid": v(8.76, -30.44) * mm, "end": v(8.72, -30.65) * mm});
            skArc(sketch, "E295", {"start": v(8.94, -30.3) * mm, "mid": v(9.3, -30.2) * mm, "end": v(9.68, -30.08) * mm});
            skLineSegment(sketch, "E296", {"start": v(11.87, -31.62) * mm, "end": v(11.95, -30.48) * mm});
            skLineSegment(sketch, "E297", {"start": v(11.95, -30.48) * mm, "end": v(11.73, -29.63) * mm});
            skArc(sketch, "E298", {"start": v(11.91, -29.27) * mm, "mid": v(11.75, -29.42) * mm, "end": v(11.73, -29.63) * mm});
            skArc(sketch, "E299", {"start": v(11.91, -29.27) * mm, "mid": v(12.27, -29.12) * mm, "end": v(12.63, -28.97) * mm});
            skLineSegment(sketch, "E300", {"start": v(14.96, -30.28) * mm, "end": v(14.92, -29.14) * mm});
            skLineSegment(sketch, "E301", {"start": v(14.92, -29.14) * mm, "end": v(14.62, -28.32) * mm});
            skArc(sketch, "E302", {"start": v(14.76, -27.94) * mm, "mid": v(14.62, -28.1) * mm, "end": v(14.62, -28.32) * mm});
            skArc(sketch, "E303", {"start": v(14.76, -27.94) * mm, "mid": v(15.1, -27.75) * mm, "end": v(15.45, -27.56) * mm});
            skLineSegment(sketch, "E304", {"start": v(17.9, -28.64) * mm, "end": v(17.75, -27.51) * mm});
            skLineSegment(sketch, "E305", {"start": v(17.75, -27.51) * mm, "end": v(17.36, -26.72) * mm});
            skArc(sketch, "E306", {"start": v(17.47, -26.33) * mm, "mid": v(17.34, -26.5) * mm, "end": v(17.36, -26.72) * mm});
            skArc(sketch, "E307", {"start": v(17.47, -26.33) * mm, "mid": v(17.8, -26.11) * mm, "end": v(18.11, -25.89) * mm});
            skLineSegment(sketch, "E308", {"start": v(20.66, -26.72) * mm, "end": v(20.4, -25.6) * mm});
            skLineSegment(sketch, "E309", {"start": v(20.4, -25.6) * mm, "end": v(19.94, -24.86) * mm});
            skArc(sketch, "E310", {"start": v(20, -24.46) * mm, "mid": v(19.9, -24.65) * mm, "end": v(19.94, -24.86) * mm});
            skArc(sketch, "E311", {"start": v(20, -24.46) * mm, "mid": v(20.3, -24.2) * mm, "end": v(20.6, -23.96) * mm});
            skLineSegment(sketch, "E312", {"start": v(23.22, -24.53) * mm, "end": v(22.84, -23.45) * mm});
            skLineSegment(sketch, "E313", {"start": v(22.84, -23.45) * mm, "end": v(22.31, -22.75) * mm});
            skArc(sketch, "E314", {"start": v(22.34, -22.34) * mm, "mid": v(22.25, -22.54) * mm, "end": v(22.31, -22.75) * mm});
            skArc(sketch, "E315", {"start": v(22.34, -22.34) * mm, "mid": v(22.61, -22.07) * mm, "end": v(22.88, -21.79) * mm});
            skLineSegment(sketch, "E316", {"start": v(25.55, -22.1) * mm, "end": v(25.06, -21.06) * mm});
            skLineSegment(sketch, "E317", {"start": v(25.06, -21.06) * mm, "end": v(24.46, -20.42) * mm});
            skArc(sketch, "E318", {"start": v(24.45, -20) * mm, "mid": v(24.38, -20.22) * mm, "end": v(24.46, -20.42) * mm});
            skArc(sketch, "E319", {"start": v(24.45, -20) * mm, "mid": v(24.7, -19.7) * mm, "end": v(24.93, -19.4) * mm});
            skLineSegment(sketch, "E320", {"start": v(27.62, -19.44) * mm, "end": v(27.04, -18.46) * mm});
            skLineSegment(sketch, "E321", {"start": v(27.04, -18.46) * mm, "end": v(26.37, -17.88) * mm});
            skArc(sketch, "E322", {"start": v(26.32, -17.47) * mm, "mid": v(26.27, -17.69) * mm, "end": v(26.37, -17.88) * mm});
            skArc(sketch, "E323", {"start": v(26.32, -17.47) * mm, "mid": v(26.53, -17.15) * mm, "end": v(26.74, -16.82) * mm});
            skLineSegment(sketch, "E324", {"start": v(29.42, -16.6) * mm, "end": v(28.74, -15.68) * mm});
            skLineSegment(sketch, "E325", {"start": v(28.74, -15.68) * mm, "end": v(28.02, -15.17) * mm});
            skArc(sketch, "E326", {"start": v(27.93, -14.77) * mm, "mid": v(27.9, -14.98) * mm, "end": v(28.02, -15.17) * mm});
            skArc(sketch, "E327", {"start": v(27.93, -14.77) * mm, "mid": v(28.1, -14.42) * mm, "end": v(28.28, -14.08) * mm});
            skLineSegment(sketch, "E328", {"start": v(30.92, -13.58) * mm, "end": v(30.15, -12.74) * mm});
            skLineSegment(sketch, "E329", {"start": v(30.15, -12.74) * mm, "end": v(29.4, -12.3) * mm});
            skArc(sketch, "E330", {"start": v(29.26, -11.91) * mm, "mid": v(29.25, -12.13) * mm, "end": v(29.4, -12.3) * mm});
            skArc(sketch, "E331", {"start": v(29.26, -11.91) * mm, "mid": v(29.4, -11.55) * mm, "end": v(29.54, -11.2) * mm});
            skLineSegment(sketch, "E332", {"start": v(32.12, -10.44) * mm, "end": v(31.27, -9.67) * mm});
            skLineSegment(sketch, "E333", {"start": v(31.27, -9.67) * mm, "end": v(30.47, -9.31) * mm});
            skArc(sketch, "E334", {"start": v(30.3, -8.94) * mm, "mid": v(30.31, -9.16) * mm, "end": v(30.47, -9.31) * mm});
            skArc(sketch, "E335", {"start": v(30.3, -8.94) * mm, "mid": v(30.4, -8.57) * mm, "end": v(30.5, -8.2) * mm});
            skLineSegment(sketch, "E336", {"start": v(33, -7.19) * mm, "end": v(32.08, -6.5) * mm});
            skLineSegment(sketch, "E337", {"start": v(32.08, -6.5) * mm, "end": v(31.24, -6.23) * mm});
            skArc(sketch, "E338", {"start": v(31.04, -5.88) * mm, "mid": v(31.07, -6.1) * mm, "end": v(31.24, -6.23) * mm});
            skArc(sketch, "E339", {"start": v(31.04, -5.88) * mm, "mid": v(31.1, -5.5) * mm, "end": v(31.17, -5.12) * mm});
            skLineSegment(sketch, "E340", {"start": v(33.55, -3.87) * mm, "end": v(32.56, -3.28) * mm});
            skLineSegment(sketch, "E341", {"start": v(32.56, -3.28) * mm, "end": v(31.7, -3.1) * mm});
            skArc(sketch, "E342", {"start": v(31.47, -2.76) * mm, "mid": v(31.52, -2.97) * mm, "end": v(31.7, -3.1) * mm});
            skArc(sketch, "E343", {"start": v(31.47, -2.76) * mm, "mid": v(31.5, -2.37) * mm, "end": v(31.52, -1.99) * mm});
            skLineSegment(sketch, "E344", {"start": v(33.76, -0.5) * mm, "end": v(32.73, -0.02) * mm});
            skLineSegment(sketch, "E345", {"start": v(32.73, -0.02) * mm, "end": v(31.86, 0.08) * mm});
            skArc(sketch, "E346", {"start": v(31.58, 0.39) * mm, "mid": v(31.66, 0.18) * mm, "end": v(31.86, 0.08) * mm});
            skArc(sketch, "E347", {"start": v(31.58, 0.39) * mm, "mid": v(31.58, 0.77) * mm, "end": v(31.56, 1.16) * mm});
            skLineSegment(sketch, "E348", {"start": v(33.65, 2.86) * mm, "end": v(32.57, 3.23) * mm});
            skLineSegment(sketch, "E349", {"start": v(32.57, 3.23) * mm, "end": v(31.69, 3.25) * mm});
            skArc(sketch, "E350", {"start": v(31.39, 3.53) * mm, "mid": v(31.49, 3.33) * mm, "end": v(31.69, 3.25) * mm});
            skLineSegment(sketch, "E351", {"start": v(33.2, 6.2) * mm, "end": v(32.08, 6.46) * mm});
            skLineSegment(sketch, "E352", {"start": v(32.08, 6.46) * mm, "end": v(31.2, 6.4) * mm});
            skArc(sketch, "E353", {"start": v(30.88, 6.64) * mm, "mid": v(31, 6.45) * mm, "end": v(31.2, 6.4) * mm});
            skLineSegment(sketch, "E354", {"start": v(32.4, 9.47) * mm, "end": v(31.28, 9.62) * mm});
            skLineSegment(sketch, "E355", {"start": v(31.28, 9.62) * mm, "end": v(30.41, 9.47) * mm});
            skArc(sketch, "E356", {"start": v(30.06, 9.68) * mm, "mid": v(30.2, 9.5) * mm, "end": v(30.41, 9.47) * mm});
            skLineSegment(sketch, "E357", {"start": v(31.3, 12.65) * mm, "end": v(30.16, 12.69) * mm});
            skLineSegment(sketch, "E358", {"start": v(30.16, 12.69) * mm, "end": v(29.32, 12.45) * mm});
            skArc(sketch, "E359", {"start": v(28.95, 12.62) * mm, "mid": v(29.1, 12.47) * mm, "end": v(29.32, 12.45) * mm});
            skLineSegment(sketch, "E360", {"start": v(29.89, 15.7) * mm, "end": v(28.75, 15.63) * mm});
            skLineSegment(sketch, "E361", {"start": v(28.75, 15.63) * mm, "end": v(27.93, 15.3) * mm});
            skArc(sketch, "E362", {"start": v(27.55, 15.44) * mm, "mid": v(27.71, 15.3) * mm, "end": v(27.93, 15.3) * mm});
            skLineSegment(sketch, "E363", {"start": v(28.18, 18.6) * mm, "end": v(27.05, 18.41) * mm});
            skLineSegment(sketch, "E364", {"start": v(27.05, 18.41) * mm, "end": v(26.27, 18.01) * mm});
            skArc(sketch, "E365", {"start": v(25.87, 18.1) * mm, "mid": v(26.05, 17.98) * mm, "end": v(26.27, 18.01) * mm});
            skLineSegment(sketch, "E366", {"start": v(26.18, 21.31) * mm, "end": v(25.08, 21.02) * mm});
            skLineSegment(sketch, "E367", {"start": v(25.08, 21.02) * mm, "end": v(24.34, 20.54) * mm});
            skArc(sketch, "E368", {"start": v(23.94, 20.6) * mm, "mid": v(24.13, 20.49) * mm, "end": v(24.34, 20.54) * mm});
            skLineSegment(sketch, "E369", {"start": v(23.93, 23.81) * mm, "end": v(22.86, 23.4) * mm});
            skLineSegment(sketch, "E370", {"start": v(22.86, 23.4) * mm, "end": v(22.18, 22.86) * mm});
            skArc(sketch, "E371", {"start": v(21.77, 22.88) * mm, "mid": v(21.97, 22.79) * mm, "end": v(22.18, 22.86) * mm});
            skLineSegment(sketch, "E372", {"start": v(21.44, 26.08) * mm, "end": v(20.41, 25.57) * mm});
            skLineSegment(sketch, "E373", {"start": v(20.41, 25.57) * mm, "end": v(19.79, 24.95) * mm});
            skArc(sketch, "E374", {"start": v(19.38, 24.93) * mm, "mid": v(19.59, 24.86) * mm, "end": v(19.79, 24.95) * mm});
            skLineSegment(sketch, "E375", {"start": v(18.73, 28.08) * mm, "end": v(17.77, 27.47) * mm});
            skLineSegment(sketch, "E376", {"start": v(17.77, 27.47) * mm, "end": v(17.2, 26.8) * mm});
            skArc(sketch, "E377", {"start": v(16.8, 26.73) * mm, "mid": v(17.01, 26.7) * mm, "end": v(17.2, 26.8) * mm});
            skLineSegment(sketch, "E378", {"start": v(15.84, 29.8) * mm, "end": v(14.94, 29.1) * mm});
            skLineSegment(sketch, "E379", {"start": v(14.94, 29.1) * mm, "end": v(14.45, 28.38) * mm});
            skArc(sketch, "E380", {"start": v(14.05, 28.27) * mm, "mid": v(14.27, 28.25) * mm, "end": v(14.45, 28.38) * mm});
            skLineSegment(sketch, "E381", {"start": v(12.8, 31.24) * mm, "end": v(11.97, 30.45) * mm});
            skLineSegment(sketch, "E382", {"start": v(11.97, 30.45) * mm, "end": v(11.55, 29.68) * mm});
            skArc(sketch, "E383", {"start": v(11.17, 29.53) * mm, "mid": v(11.39, 29.53) * mm, "end": v(11.55, 29.68) * mm});
            skLineSegment(sketch, "E384", {"start": v(9.62, 32.35) * mm, "end": v(8.87, 31.49) * mm});
            skLineSegment(sketch, "E385", {"start": v(8.87, 31.49) * mm, "end": v(8.54, 30.68) * mm});
            skArc(sketch, "E386", {"start": v(8.17, 30.5) * mm, "mid": v(8.39, 30.52) * mm, "end": v(8.54, 30.68) * mm});
            skLineSegment(sketch, "E387", {"start": v(6.35, 33.15) * mm, "end": v(5.7, 32.22) * mm});
            skLineSegment(sketch, "E388", {"start": v(5.7, 32.22) * mm, "end": v(5.44, 31.38) * mm});
            skArc(sketch, "E389", {"start": v(5.1, 31.16) * mm, "mid": v(5.3, 31.2) * mm, "end": v(5.44, 31.38) * mm});
            skLineSegment(sketch, "E390", {"start": v(3.02, 33.62) * mm, "end": v(2.46, 32.62) * mm});
            skLineSegment(sketch, "E391", {"start": v(2.46, 32.62) * mm, "end": v(2.29, 31.76) * mm});
            skArc(sketch, "E392", {"start": v(1.96, 31.51) * mm, "mid": v(2.17, 31.58) * mm, "end": v(2.29, 31.76) * mm});
            skLineSegment(sketch, "E393", {"start": v(-0.35, 33.75) * mm, "end": v(-0.8, 32.7) * mm});
            skLineSegment(sketch, "E394", {"start": v(-0.8, 32.7) * mm, "end": v(-0.89, 31.83) * mm});
            skArc(sketch, "E395", {"start": v(-1.19, 31.55) * mm, "mid": v(-0.98, 31.63) * mm, "end": v(-0.89, 31.83) * mm});
            skLineSegment(sketch, "E396", {"start": v(-3.7, 33.55) * mm, "end": v(-4.06, 32.46) * mm});
            skLineSegment(sketch, "E397", {"start": v(-4.06, 32.46) * mm, "end": v(-4.05, 31.59) * mm});
            skArc(sketch, "E398", {"start": v(-4.32, 31.27) * mm, "mid": v(-4.13, 31.38) * mm, "end": v(-4.05, 31.59) * mm});
            skLineSegment(sketch, "E399", {"start": v(-7.03, 33.01) * mm, "end": v(-7.27, 31.9) * mm});
            skLineSegment(sketch, "E400", {"start": v(-7.27, 31.9) * mm, "end": v(-7.18, 31.02) * mm});
            skArc(sketch, "E401", {"start": v(-7.42, 30.69) * mm, "mid": v(-7.24, 30.81) * mm, "end": v(-7.18, 31.02) * mm});
            skLineSegment(sketch, "E402", {"start": v(-10.28, 32.15) * mm, "end": v(-10.41, 31.01) * mm});
            skLineSegment(sketch, "E403", {"start": v(-10.41, 31.01) * mm, "end": v(-10.24, 30.16) * mm});
            skArc(sketch, "E404", {"start": v(-10.44, 29.8) * mm, "mid": v(-10.27, 29.94) * mm, "end": v(-10.24, 30.16) * mm});
            skLineSegment(sketch, "E405", {"start": v(-13.44, 30.97) * mm, "end": v(-13.45, 29.82) * mm});
            skLineSegment(sketch, "E406", {"start": v(-13.45, 29.82) * mm, "end": v(-13.19, 28.99) * mm});
            skArc(sketch, "E407", {"start": v(-13.35, 28.61) * mm, "mid": v(-13.2, 28.77) * mm, "end": v(-13.19, 28.99) * mm});
            skLineSegment(sketch, "E408", {"start": v(-16.45, 29.47) * mm, "end": v(-16.35, 28.34) * mm});
            skLineSegment(sketch, "E409", {"start": v(-16.35, 28.34) * mm, "end": v(-16.01, 27.53) * mm});
            skArc(sketch, "E410", {"start": v(-16.14, 27.14) * mm, "mid": v(-16, 27.3) * mm, "end": v(-16.01, 27.53) * mm});
            skLineSegment(sketch, "E411", {"start": v(-19.3, 27.7) * mm, "end": v(-19.1, 26.57) * mm});
            skLineSegment(sketch, "E412", {"start": v(-19.1, 26.57) * mm, "end": v(-18.67, 25.8) * mm});
            skArc(sketch, "E413", {"start": v(-18.76, 25.4) * mm, "mid": v(-18.64, 25.58) * mm, "end": v(-18.67, 25.8) * mm});
            skLineSegment(sketch, "E414", {"start": v(-21.97, 25.63) * mm, "end": v(-21.65, 24.53) * mm});
            skLineSegment(sketch, "E415", {"start": v(-21.65, 24.53) * mm, "end": v(-21.15, 23.81) * mm});
            skArc(sketch, "E416", {"start": v(-21.2, 23.4) * mm, "mid": v(-21.1, 23.6) * mm, "end": v(-21.15, 23.81) * mm});
            skLineSegment(sketch, "E417", {"start": v(-24.41, 23.32) * mm, "end": v(-23.98, 22.26) * mm});
            skLineSegment(sketch, "E418", {"start": v(-23.98, 22.26) * mm, "end": v(-23.42, 21.59) * mm});
            skArc(sketch, "E419", {"start": v(-23.42, 21.18) * mm, "mid": v(-23.34, 21.38) * mm, "end": v(-23.42, 21.59) * mm});
            skLineSegment(sketch, "E420", {"start": v(-26.62, 20.77) * mm, "end": v(-26.08, 19.76) * mm});
            skLineSegment(sketch, "E421", {"start": v(-26.08, 19.76) * mm, "end": v(-25.45, 19.15) * mm});
            skArc(sketch, "E422", {"start": v(-25.42, 18.74) * mm, "mid": v(-25.36, 18.95) * mm, "end": v(-25.45, 19.15) * mm});
            skLineSegment(sketch, "E423", {"start": v(-28.55, 18.02) * mm, "end": v(-27.92, 17.06) * mm});
            skLineSegment(sketch, "E424", {"start": v(-27.92, 17.06) * mm, "end": v(-27.23, 16.52) * mm});
            skArc(sketch, "E425", {"start": v(-27.16, 16.11) * mm, "mid": v(-27.12, 16.33) * mm, "end": v(-27.23, 16.52) * mm});
            skLineSegment(sketch, "E426", {"start": v(-30.2, 15.08) * mm, "end": v(-29.48, 14.2) * mm});
            skLineSegment(sketch, "E427", {"start": v(-29.48, 14.2) * mm, "end": v(-28.74, 13.72) * mm});
            skArc(sketch, "E428", {"start": v(-28.63, 13.33) * mm, "mid": v(-28.61, 13.55) * mm, "end": v(-28.74, 13.72) * mm});
            skLineSegment(sketch, "E429", {"start": v(-31.56, 12) * mm, "end": v(-30.75, 11.2) * mm});
            skLineSegment(sketch, "E430", {"start": v(-30.75, 11.2) * mm, "end": v(-29.97, 10.8) * mm});
            skArc(sketch, "E431", {"start": v(-29.81, 10.41) * mm, "mid": v(-29.82, 10.63) * mm, "end": v(-29.97, 10.8) * mm});
            skLineSegment(sketch, "E432", {"start": v(-32.6, 8.8) * mm, "end": v(-31.71, 8.07) * mm});
            skLineSegment(sketch, "E433", {"start": v(-31.71, 8.07) * mm, "end": v(-30.9, 7.76) * mm});
            skArc(sketch, "E434", {"start": v(-30.7, 7.4) * mm, "mid": v(-30.73, 7.61) * mm, "end": v(-30.9, 7.76) * mm});
            skLineSegment(sketch, "E435", {"start": v(-33.31, 5.5) * mm, "end": v(-32.36, 4.88) * mm});
            skLineSegment(sketch, "E436", {"start": v(-32.36, 4.88) * mm, "end": v(-31.52, 4.64) * mm});
            skArc(sketch, "E437", {"start": v(-31.29, 4.3) * mm, "mid": v(-31.34, 4.51) * mm, "end": v(-31.52, 4.64) * mm});
            skLineSegment(sketch, "E438", {"start": v(-33.7, 2.16) * mm, "end": v(-32.69, 1.63) * mm});
            skLineSegment(sketch, "E439", {"start": v(-32.69, 1.63) * mm, "end": v(-31.82, 1.48) * mm});
            skArc(sketch, "E440", {"start": v(-31.56, 1.16) * mm, "mid": v(-31.63, 1.37) * mm, "end": v(-31.82, 1.48) * mm});
            skArc(sketch, "E441", {"start": v(-33.76, -0.5) * mm, "mid": v(-33.76, -0.86) * mm, "end": v(-33.75, -1.2) * mm});
            skArc(sketch, "E442", {"start": v(-33.55, -3.87) * mm, "mid": v(-33.5, -4.21) * mm, "end": v(-33.46, -4.56) * mm});
            skArc(sketch, "E443", {"start": v(-33.65, 2.86) * mm, "mid": v(-33.67, 2.51) * mm, "end": v(-33.7, 2.16) * mm});
            skArc(sketch, "E444", {"start": v(-33, -7.19) * mm, "mid": v(-32.92, -7.53) * mm, "end": v(-32.84, -7.86) * mm});
            skArc(sketch, "E445", {"start": v(-33.2, 6.2) * mm, "mid": v(-33.25, 5.85) * mm, "end": v(-33.31, 5.5) * mm});
            skArc(sketch, "E446", {"start": v(-32.12, -10.44) * mm, "mid": v(-32, -10.77) * mm, "end": v(-31.9, -11.1) * mm});
            skArc(sketch, "E447", {"start": v(-32.4, 9.47) * mm, "mid": v(-32.5, 9.13) * mm, "end": v(-32.6, 8.8) * mm});
            skArc(sketch, "E448", {"start": v(-30.92, -13.58) * mm, "mid": v(-30.78, -13.9) * mm, "end": v(-30.64, -14.22) * mm});
            skArc(sketch, "E449", {"start": v(-31.3, 12.65) * mm, "mid": v(-31.43, 12.32) * mm, "end": v(-31.56, 12) * mm});
            skArc(sketch, "E450", {"start": v(-29.42, -16.6) * mm, "mid": v(-29.24, -16.9) * mm, "end": v(-29.07, -17.2) * mm});
            skArc(sketch, "E451", {"start": v(-29.89, 15.7) * mm, "mid": v(-30.05, 15.4) * mm, "end": v(-30.2, 15.08) * mm});
            skArc(sketch, "E452", {"start": v(-27.62, -19.44) * mm, "mid": v(-27.42, -19.72) * mm, "end": v(-27.21, -20) * mm});
            skArc(sketch, "E453", {"start": v(-28.18, 18.6) * mm, "mid": v(-28.37, 18.3) * mm, "end": v(-28.55, 18.02) * mm});
            skArc(sketch, "E454", {"start": v(-25.55, -22.1) * mm, "mid": v(-25.32, -22.36) * mm, "end": v(-25.09, -22.62) * mm});
            skArc(sketch, "E455", {"start": v(-26.18, 21.31) * mm, "mid": v(-26.4, 21.04) * mm, "end": v(-26.62, 20.77) * mm});
            skArc(sketch, "E456", {"start": v(-23.22, -24.53) * mm, "mid": v(-22.97, -24.77) * mm, "end": v(-22.71, -25) * mm});
            skArc(sketch, "E457", {"start": v(-23.93, 23.81) * mm, "mid": v(-24.17, 23.56) * mm, "end": v(-24.41, 23.32) * mm});
            skArc(sketch, "E458", {"start": v(-20.66, -26.72) * mm, "mid": v(-20.39, -26.93) * mm, "end": v(-20.11, -27.14) * mm});
            skArc(sketch, "E459", {"start": v(-21.44, 26.08) * mm, "mid": v(-21.7, 25.85) * mm, "end": v(-21.97, 25.63) * mm});
            skArc(sketch, "E460", {"start": v(-17.9, -28.64) * mm, "mid": v(-17.6, -28.83) * mm, "end": v(-17.31, -29) * mm});
            skArc(sketch, "E461", {"start": v(-18.73, 28.08) * mm, "mid": v(-19.02, 27.89) * mm, "end": v(-19.3, 27.7) * mm});
            skArc(sketch, "E462", {"start": v(-14.96, -30.28) * mm, "mid": v(-14.65, -30.44) * mm, "end": v(-14.34, -30.59) * mm});
            skArc(sketch, "E463", {"start": v(-15.84, 29.8) * mm, "mid": v(-16.15, 29.64) * mm, "end": v(-16.45, 29.47) * mm});
            skArc(sketch, "E464", {"start": v(-11.87, -31.62) * mm, "mid": v(-11.55, -31.74) * mm, "end": v(-11.22, -31.86) * mm});
            skArc(sketch, "E465", {"start": v(-12.8, 31.24) * mm, "mid": v(-13.12, 31.1) * mm, "end": v(-13.44, 30.97) * mm});
            skArc(sketch, "E466", {"start": v(-8.67, -32.65) * mm, "mid": v(-8.33, -32.74) * mm, "end": v(-8, -32.82) * mm});
            skArc(sketch, "E467", {"start": v(-9.62, 32.35) * mm, "mid": v(-9.95, 32.25) * mm, "end": v(-10.28, 32.15) * mm});
            skArc(sketch, "E468", {"start": v(-5.38, -33.35) * mm, "mid": v(-5.03, -33.4) * mm, "end": v(-4.69, -33.45) * mm});
            skArc(sketch, "E469", {"start": v(-6.35, 33.15) * mm, "mid": v(-6.7, 33.08) * mm, "end": v(-7.03, 33.01) * mm});
            skArc(sketch, "E470", {"start": v(-2.03, -33.72) * mm, "mid": v(-1.68, -33.74) * mm, "end": v(-1.34, -33.75) * mm});
            skArc(sketch, "E471", {"start": v(-3.02, 33.62) * mm, "mid": v(-3.36, 33.59) * mm, "end": v(-3.7, 33.55) * mm});
            skArc(sketch, "E472", {"start": v(1.34, -33.75) * mm, "mid": v(1.68, -33.74) * mm, "end": v(2.03, -33.72) * mm});
            skArc(sketch, "E473", {"start": v(0.35, 33.75) * mm, "mid": v(0, 33.75) * mm, "end": v(-0.35, 33.75) * mm});
            skArc(sketch, "E474", {"start": v(4.69, -33.45) * mm, "mid": v(5.03, -33.4) * mm, "end": v(5.38, -33.35) * mm});
            skArc(sketch, "E475", {"start": v(3.7, 33.55) * mm, "mid": v(3.36, 33.59) * mm, "end": v(3.02, 33.62) * mm});
            skArc(sketch, "E476", {"start": v(8, -32.82) * mm, "mid": v(8.33, -32.74) * mm, "end": v(8.67, -32.65) * mm});
            skArc(sketch, "E477", {"start": v(7.03, 33.01) * mm, "mid": v(6.7, 33.08) * mm, "end": v(6.35, 33.15) * mm});
            skArc(sketch, "E478", {"start": v(11.22, -31.86) * mm, "mid": v(11.55, -31.74) * mm, "end": v(11.87, -31.62) * mm});
            skArc(sketch, "E479", {"start": v(10.28, 32.15) * mm, "mid": v(9.95, 32.25) * mm, "end": v(9.62, 32.35) * mm});
            skArc(sketch, "E480", {"start": v(14.34, -30.59) * mm, "mid": v(14.65, -30.44) * mm, "end": v(14.96, -30.28) * mm});
            skArc(sketch, "E481", {"start": v(13.44, 30.97) * mm, "mid": v(13.12, 31.1) * mm, "end": v(12.8, 31.24) * mm});
            skArc(sketch, "E482", {"start": v(17.31, -29) * mm, "mid": v(17.6, -28.83) * mm, "end": v(17.9, -28.64) * mm});
            skArc(sketch, "E483", {"start": v(16.45, 29.47) * mm, "mid": v(16.15, 29.64) * mm, "end": v(15.84, 29.8) * mm});
            skArc(sketch, "E484", {"start": v(20.11, -27.14) * mm, "mid": v(20.39, -26.93) * mm, "end": v(20.66, -26.72) * mm});
            skArc(sketch, "E485", {"start": v(19.3, 27.7) * mm, "mid": v(19.02, 27.89) * mm, "end": v(18.73, 28.08) * mm});
            skArc(sketch, "E486", {"start": v(22.71, -25) * mm, "mid": v(22.97, -24.77) * mm, "end": v(23.22, -24.53) * mm});
            skArc(sketch, "E487", {"start": v(21.97, 25.63) * mm, "mid": v(21.7, 25.85) * mm, "end": v(21.44, 26.08) * mm});
            skArc(sketch, "E488", {"start": v(25.09, -22.62) * mm, "mid": v(25.32, -22.36) * mm, "end": v(25.55, -22.1) * mm});
            skArc(sketch, "E489", {"start": v(24.41, 23.32) * mm, "mid": v(24.17, 23.56) * mm, "end": v(23.93, 23.81) * mm});
            skArc(sketch, "E490", {"start": v(27.21, -20) * mm, "mid": v(27.42, -19.72) * mm, "end": v(27.62, -19.44) * mm});
            skArc(sketch, "E491", {"start": v(26.62, 20.77) * mm, "mid": v(26.4, 21.04) * mm, "end": v(26.18, 21.31) * mm});
            skArc(sketch, "E492", {"start": v(29.07, -17.2) * mm, "mid": v(29.24, -16.9) * mm, "end": v(29.42, -16.6) * mm});
            skArc(sketch, "E493", {"start": v(28.55, 18.02) * mm, "mid": v(28.37, 18.3) * mm, "end": v(28.18, 18.6) * mm});
            skArc(sketch, "E494", {"start": v(30.64, -14.22) * mm, "mid": v(30.78, -13.9) * mm, "end": v(30.92, -13.58) * mm});
            skArc(sketch, "E495", {"start": v(30.2, 15.08) * mm, "mid": v(30.05, 15.4) * mm, "end": v(29.89, 15.7) * mm});
            skArc(sketch, "E496", {"start": v(31.9, -11.1) * mm, "mid": v(32, -10.77) * mm, "end": v(32.12, -10.44) * mm});
            skArc(sketch, "E497", {"start": v(31.56, 12) * mm, "mid": v(31.43, 12.32) * mm, "end": v(31.3, 12.65) * mm});
            skArc(sketch, "E498", {"start": v(32.84, -7.86) * mm, "mid": v(-30.7, 14.05) * mm, "end": v(27.4, -19.76) * mm});
            skArc(sketch, "E499", {"start": v(32.6, 8.8) * mm, "mid": v(32.5, 9.13) * mm, "end": v(32.4, 9.47) * mm});
            skArc(sketch, "E500", {"start": v(33.46, -4.56) * mm, "mid": v(33.5, -4.21) * mm, "end": v(33.55, -3.87) * mm});
            skArc(sketch, "E501", {"start": v(33.31, 5.5) * mm, "mid": v(33.25, 5.85) * mm, "end": v(33.2, 6.2) * mm});
            skArc(sketch, "E502", {"start": v(33.75, -1.2) * mm, "mid": v(33.76, -0.86) * mm, "end": v(33.76, -0.5) * mm});
            skArc(sketch, "E503", {"start": v(33.7, 2.16) * mm, "mid": v(33.67, 2.51) * mm, "end": v(33.65, 2.86) * mm});
            skCircle(sketch, "E504", {"center": v(0, 0) * mm, "radius": 36.96 * mm});
            skCircle(sketch, "E505", {"center": v(0, 0) * mm, "radius": 9 * mm});
            skCircle(sketch, "E506", {"center": v(0, 0) * mm, "radius": 5 * mm});
            skLineSegment(sketch, "E507", {"start": v(0, 0) * mm, "end": v(36.96, 0) * mm});
            skLineSegment(sketch, "E508", {"start": v(0, 36.96) * mm, "end": v(0, -36.96) * mm});
            skLineSegment(sketch, "E509", {"start": v(0, 0) * mm, "end": v(-36.96, -0.02) * mm});
            skLineSegment(sketch, "E510", {"start": v(0, 0) * mm, "end": v(31.24, -19.76) * mm});
            skLineSegment(sketch, "E511", {"start": v(31.24, -19.76) * mm, "end": v(-31.24, 19.76) * mm});
            skSolve(sketch);
        }
        {
            var Q0;
            Q0=makeQuery(id+"F0.imprint","IMPRINT",FACE,{"disambiguationData":[TD([[makeQuery(id+"F0.imprint","IMPRINT",EDGE,{"derivedFrom":sQuery(id+"F0.wireOp",EDGE,"E0")}),-1.0]])]});
            var Q1;
            {var subQ8=sQuery(id+"F0.wireOp",EDGE,"E4");Q1=makeQuery(id+"F0.imprint","IMPRINT",FACE,{"disambiguationData":[TD([[makeQuery(id+"F0.imprint","IMPRINT",EDGE,{"derivedFrom":subQ8}),-1.0]])]});}
            var Q2;
            Q2=makeQuery(id+"F0.imprint","IMPRINT",FACE,{"disambiguationData":[TD([[makeQuery(id+"F0.imprint","IMPRINT",EDGE,{"derivedFrom":sQuery(id+"F0.wireOp",EDGE,"E46")}),-1.0]])]});
            var Q3;
            Q3=makeQuery(id+"F0.imprint","IMPRINT",FACE,{"disambiguationData":[TD([[makeQuery(id+"F0.imprint","IMPRINT",EDGE,{"derivedFrom":sQuery(id+"F0.wireOp",EDGE,"E116")}),-1.0]])]});
            var Q4;
            {var subQ27=sQuery(id+"F0.wireOp",EDGE,"E178");Q4=makeQuery(id+"F0.imprint","IMPRINT",FACE,{"disambiguationData":[TD([[makeQuery(id+"F0.imprint","IMPRINT",EDGE,{"derivedFrom":subQ27}),1.0]])]});}
            var Q5;
            {var subQ40=sQuery(id+"F0.wireOp",EDGE,"E108");Q5=makeQuery(id+"F0.imprint","IMPRINT",FACE,{"disambiguationData":[TD([[makeQuery(id+"F0.imprint","IMPRINT",EDGE,{"derivedFrom":subQ40}),1.0]])]});}
            var Q6;
            {var subQ3=sQuery(id+"F0.wireOp",EDGE,"E505");var subQ5=sQuery(id+"F0.wireOp",EDGE,"E508");var subQ7=makeQuery(id+"F0.imprint","INTERSECT",VERTEX,{"disambiguationData":[OD(0.0)],"derivedFrom":[subQ3,subQ5]});Q6=makeQuery(id+"F0.imprint","IMPRINT",FACE,{"disambiguationData":[TD([[makeQuery(id+"F0.imprint","IMPRINT",EDGE,{"disambiguationData":[TD([[subQ7,-1.0]])],"derivedFrom":subQ3}),1.0]])]});}
            var Q7;
            {var subQ0=sQuery(id+"F0.wireOp",EDGE,"E508");var subQ3=sQuery(id+"F0.wireOp",EDGE,"E505");var subQ4=makeQuery(id+"F0.imprint","INTERSECT",VERTEX,{"disambiguationData":[OD(0.0)],"derivedFrom":[subQ3,subQ0]});Q7=makeQuery(id+"F0.imprint","IMPRINT",FACE,{"disambiguationData":[TD([[makeQuery(id+"F0.imprint","IMPRINT",EDGE,{"disambiguationData":[TD([[subQ4,1.0]])],"derivedFrom":subQ3}),1.0]])]});}
            var Q8;
            {var subQ3=sQuery(id+"F0.wireOp",EDGE,"E505");var subQ5=sQuery(id+"F0.wireOp",EDGE,"E507");var subQ7=makeQuery(id+"F0.imprint","INTERSECT",VERTEX,{"derivedFrom":[subQ3,subQ5]});Q8=makeQuery(id+"F0.imprint","IMPRINT",FACE,{"disambiguationData":[TD([[makeQuery(id+"F0.imprint","IMPRINT",EDGE,{"disambiguationData":[TD([[subQ7,1.0]])],"derivedFrom":subQ3}),1.0]])]});}
            var Q9;
            {var subQ3=sQuery(id+"F0.wireOp",EDGE,"E505");var subQ5=sQuery(id+"F0.wireOp",EDGE,"E508");var subQ7=makeQuery(id+"F0.imprint","INTERSECT",VERTEX,{"disambiguationData":[OD(1.0)],"derivedFrom":[subQ3,subQ5]});Q9=makeQuery(id+"F0.imprint","IMPRINT",FACE,{"disambiguationData":[TD([[makeQuery(id+"F0.imprint","IMPRINT",EDGE,{"disambiguationData":[TD([[subQ7,-1.0]])],"derivedFrom":subQ3}),1.0]])]});}
            var Q10;
            {var subQ0=sQuery(id+"F0.wireOp",EDGE,"E509");var subQ3=sQuery(id+"F0.wireOp",EDGE,"E505");var subQ4=makeQuery(id+"F0.imprint","INTERSECT",VERTEX,{"derivedFrom":[subQ3,subQ0]});Q10=makeQuery(id+"F0.imprint","IMPRINT",FACE,{"disambiguationData":[TD([[makeQuery(id+"F0.imprint","IMPRINT",EDGE,{"disambiguationData":[TD([[subQ4,-1.0]])],"derivedFrom":subQ3}),1.0]])]});}
            var Q11;
            {var subQ0=sQuery(id+"F0.wireOp",EDGE,"E511");var subQ3=sQuery(id+"F0.wireOp",EDGE,"E505");var subQ4=makeQuery(id+"F0.imprint","INTERSECT",VERTEX,{"disambiguationData":[OD(0.0)],"derivedFrom":[subQ3,subQ0]});Q11=makeQuery(id+"F0.imprint","IMPRINT",FACE,{"disambiguationData":[TD([[makeQuery(id+"F0.imprint","IMPRINT",EDGE,{"disambiguationData":[TD([[subQ4,-1.0]])],"derivedFrom":subQ3}),1.0]])]});}
            extrude(context, id + "F1", {"entities" : qUnion([Q0, Q1, Q2, Q3, Q4, Q5, Q6, Q7, Q8, Q9, Q10, Q11]), "depth" : 5 * mm});
        }
        {
            var Q0;
            Q0=makeQuery(id+"F1.opExtrude","SWEPT_BODY",BODY,{"disambiguationData":[OSD([sQuery(id+"F0.wireOp",EDGE,"E0"),sQuery(id+"F0.wireOp",EDGE,"E1"),sQuery(id+"F0.wireOp",EDGE,"E2"),sQuery(id+"F0.wireOp",EDGE,"E3"),sQuery(id+"F0.wireOp",EDGE,"E4"),sQuery(id+"F0.wireOp",EDGE,"E5"),sQuery(id+"F0.wireOp",EDGE,"E6"),sQuery(id+"F0.wireOp",EDGE,"E7"),sQuery(id+"F0.wireOp",EDGE,"E8"),sQuery(id+"F0.wireOp",EDGE,"E9"),sQuery(id+"F0.wireOp",EDGE,"E10"),sQuery(id+"F0.wireOp",EDGE,"E11"),sQuery(id+"F0.wireOp",EDGE,"E12"),sQuery(id+"F0.wireOp",EDGE,"E13"),sQuery(id+"F0.wireOp",EDGE,"E14"),sQuery(id+"F0.wireOp",EDGE,"E15"),sQuery(id+"F0.wireOp",EDGE,"E16"),sQuery(id+"F0.wireOp",EDGE,"E17"),sQuery(id+"F0.wireOp",EDGE,"E18"),sQuery(id+"F0.wireOp",EDGE,"E19"),sQuery(id+"F0.wireOp",EDGE,"E20"),sQuery(id+"F0.wireOp",EDGE,"E21"),sQuery(id+"F0.wireOp",EDGE,"E22"),sQuery(id+"F0.wireOp",EDGE,"E23"),sQuery(id+"F0.wireOp",EDGE,"E24"),sQuery(id+"F0.wireOp",EDGE,"E25"),sQuery(id+"F0.wireOp",EDGE,"E26"),sQuery(id+"F0.wireOp",EDGE,"E27"),sQuery(id+"F0.wireOp",EDGE,"E28"),sQuery(id+"F0.wireOp",EDGE,"E29"),sQuery(id+"F0.wireOp",EDGE,"E30"),sQuery(id+"F0.wireOp",EDGE,"E31"),sQuery(id+"F0.wireOp",EDGE,"E32"),sQuery(id+"F0.wireOp",EDGE,"E33"),sQuery(id+"F0.wireOp",EDGE,"E34"),sQuery(id+"F0.wireOp",EDGE,"E35"),sQuery(id+"F0.wireOp",EDGE,"E36"),sQuery(id+"F0.wireOp",EDGE,"E37"),sQuery(id+"F0.wireOp",EDGE,"E38"),sQuery(id+"F0.wireOp",EDGE,"E39"),sQuery(id+"F0.wireOp",EDGE,"E40"),sQuery(id+"F0.wireOp",EDGE,"E41"),sQuery(id+"F0.wireOp",EDGE,"E42"),sQuery(id+"F0.wireOp",EDGE,"E43"),sQuery(id+"F0.wireOp",EDGE,"E44"),sQuery(id+"F0.wireOp",EDGE,"E45"),sQuery(id+"F0.wireOp",EDGE,"E46"),sQuery(id+"F0.wireOp",EDGE,"E47"),sQuery(id+"F0.wireOp",EDGE,"E48"),sQuery(id+"F0.wireOp",EDGE,"E49"),sQuery(id+"F0.wireOp",EDGE,"E50"),sQuery(id+"F0.wireOp",EDGE,"E51"),sQuery(id+"F0.wireOp",EDGE,"E52"),sQuery(id+"F0.wireOp",EDGE,"E53"),sQuery(id+"F0.wireOp",EDGE,"E54"),sQuery(id+"F0.wireOp",EDGE,"E55"),sQuery(id+"F0.wireOp",EDGE,"E56"),sQuery(id+"F0.wireOp",EDGE,"E57"),sQuery(id+"F0.wireOp",EDGE,"E58"),sQuery(id+"F0.wireOp",EDGE,"E59"),sQuery(id+"F0.wireOp",EDGE,"E60"),sQuery(id+"F0.wireOp",EDGE,"E61"),sQuery(id+"F0.wireOp",EDGE,"E62"),sQuery(id+"F0.wireOp",EDGE,"E63"),sQuery(id+"F0.wireOp",EDGE,"E64"),sQuery(id+"F0.wireOp",EDGE,"E65"),sQuery(id+"F0.wireOp",EDGE,"E66"),sQuery(id+"F0.wireOp",EDGE,"E67"),sQuery(id+"F0.wireOp",EDGE,"E68"),sQuery(id+"F0.wireOp",EDGE,"E69"),sQuery(id+"F0.wireOp",EDGE,"E70"),sQuery(id+"F0.wireOp",EDGE,"E71"),sQuery(id+"F0.wireOp",EDGE,"E72"),sQuery(id+"F0.wireOp",EDGE,"E73"),sQuery(id+"F0.wireOp",EDGE,"E74"),sQuery(id+"F0.wireOp",EDGE,"E75"),sQuery(id+"F0.wireOp",EDGE,"E76"),sQuery(id+"F0.wireOp",EDGE,"E77"),sQuery(id+"F0.wireOp",EDGE,"E78"),sQuery(id+"F0.wireOp",EDGE,"E79"),sQuery(id+"F0.wireOp",EDGE,"E80"),sQuery(id+"F0.wireOp",EDGE,"E81"),sQuery(id+"F0.wireOp",EDGE,"E82"),sQuery(id+"F0.wireOp",EDGE,"E83"),sQuery(id+"F0.wireOp",EDGE,"E84"),sQuery(id+"F0.wireOp",EDGE,"E85"),sQuery(id+"F0.wireOp",EDGE,"E86"),sQuery(id+"F0.wireOp",EDGE,"E87"),sQuery(id+"F0.wireOp",EDGE,"E88"),sQuery(id+"F0.wireOp",EDGE,"E89"),sQuery(id+"F0.wireOp",EDGE,"E90"),sQuery(id+"F0.wireOp",EDGE,"E91"),sQuery(id+"F0.wireOp",EDGE,"E92"),sQuery(id+"F0.wireOp",EDGE,"E93"),sQuery(id+"F0.wireOp",EDGE,"E94"),sQuery(id+"F0.wireOp",EDGE,"E95"),sQuery(id+"F0.wireOp",EDGE,"E96"),sQuery(id+"F0.wireOp",EDGE,"E97"),sQuery(id+"F0.wireOp",EDGE,"E98"),sQuery(id+"F0.wireOp",EDGE,"E99"),sQuery(id+"F0.wireOp",EDGE,"E100"),sQuery(id+"F0.wireOp",EDGE,"E101"),sQuery(id+"F0.wireOp",EDGE,"E102"),sQuery(id+"F0.wireOp",EDGE,"E103"),sQuery(id+"F0.wireOp",EDGE,"E104"),sQuery(id+"F0.wireOp",EDGE,"E105"),sQuery(id+"F0.wireOp",EDGE,"E106"),sQuery(id+"F0.wireOp",EDGE,"E107"),sQuery(id+"F0.wireOp",EDGE,"E108"),sQuery(id+"F0.wireOp",EDGE,"E109"),sQuery(id+"F0.wireOp",EDGE,"E110"),sQuery(id+"F0.wireOp",EDGE,"E111"),sQuery(id+"F0.wireOp",EDGE,"E112"),sQuery(id+"F0.wireOp",EDGE,"E113"),sQuery(id+"F0.wireOp",EDGE,"E114"),sQuery(id+"F0.wireOp",EDGE,"E115"),sQuery(id+"F0.wireOp",EDGE,"E116"),sQuery(id+"F0.wireOp",EDGE,"E117"),sQuery(id+"F0.wireOp",EDGE,"E118"),sQuery(id+"F0.wireOp",EDGE,"E119"),sQuery(id+"F0.wireOp",EDGE,"E120"),sQuery(id+"F0.wireOp",EDGE,"E121"),sQuery(id+"F0.wireOp",EDGE,"E122"),sQuery(id+"F0.wireOp",EDGE,"E123"),sQuery(id+"F0.wireOp",EDGE,"E124"),sQuery(id+"F0.wireOp",EDGE,"E125"),sQuery(id+"F0.wireOp",EDGE,"E126"),sQuery(id+"F0.wireOp",EDGE,"E127"),sQuery(id+"F0.wireOp",EDGE,"E128"),sQuery(id+"F0.wireOp",EDGE,"E129"),sQuery(id+"F0.wireOp",EDGE,"E130"),sQuery(id+"F0.wireOp",EDGE,"E131"),sQuery(id+"F0.wireOp",EDGE,"E132"),sQuery(id+"F0.wireOp",EDGE,"E133"),sQuery(id+"F0.wireOp",EDGE,"E134"),sQuery(id+"F0.wireOp",EDGE,"E135"),sQuery(id+"F0.wireOp",EDGE,"E136"),sQuery(id+"F0.wireOp",EDGE,"E137"),sQuery(id+"F0.wireOp",EDGE,"E138"),sQuery(id+"F0.wireOp",EDGE,"E139"),sQuery(id+"F0.wireOp",EDGE,"E140"),sQuery(id+"F0.wireOp",EDGE,"E141"),sQuery(id+"F0.wireOp",EDGE,"E142"),sQuery(id+"F0.wireOp",EDGE,"E143"),sQuery(id+"F0.wireOp",EDGE,"E144"),sQuery(id+"F0.wireOp",EDGE,"E145"),sQuery(id+"F0.wireOp",EDGE,"E146"),sQuery(id+"F0.wireOp",EDGE,"E147"),sQuery(id+"F0.wireOp",EDGE,"E148"),sQuery(id+"F0.wireOp",EDGE,"E149"),sQuery(id+"F0.wireOp",EDGE,"E150"),sQuery(id+"F0.wireOp",EDGE,"E151"),sQuery(id+"F0.wireOp",EDGE,"E152"),sQuery(id+"F0.wireOp",EDGE,"E153"),sQuery(id+"F0.wireOp",EDGE,"E154"),sQuery(id+"F0.wireOp",EDGE,"E155"),sQuery(id+"F0.wireOp",EDGE,"E156"),sQuery(id+"F0.wireOp",EDGE,"E157"),sQuery(id+"F0.wireOp",EDGE,"E158"),sQuery(id+"F0.wireOp",EDGE,"E159"),sQuery(id+"F0.wireOp",EDGE,"E160"),sQuery(id+"F0.wireOp",EDGE,"E161"),sQuery(id+"F0.wireOp",EDGE,"E162"),sQuery(id+"F0.wireOp",EDGE,"E163"),sQuery(id+"F0.wireOp",EDGE,"E164"),sQuery(id+"F0.wireOp",EDGE,"E165"),sQuery(id+"F0.wireOp",EDGE,"E166"),sQuery(id+"F0.wireOp",EDGE,"E167"),sQuery(id+"F0.wireOp",EDGE,"E168"),sQuery(id+"F0.wireOp",EDGE,"E169"),sQuery(id+"F0.wireOp",EDGE,"E170"),sQuery(id+"F0.wireOp",EDGE,"E171"),sQuery(id+"F0.wireOp",EDGE,"E172"),sQuery(id+"F0.wireOp",EDGE,"E173"),sQuery(id+"F0.wireOp",EDGE,"E174"),sQuery(id+"F0.wireOp",EDGE,"E175"),sQuery(id+"F0.wireOp",EDGE,"E176"),sQuery(id+"F0.wireOp",EDGE,"E177"),sQuery(id+"F0.wireOp",EDGE,"E178"),sQuery(id+"F0.wireOp",EDGE,"E179"),sQuery(id+"F0.wireOp",EDGE,"E180"),sQuery(id+"F0.wireOp",EDGE,"E181"),sQuery(id+"F0.wireOp",EDGE,"E182"),sQuery(id+"F0.wireOp",EDGE,"E183"),sQuery(id+"F0.wireOp",EDGE,"E184"),sQuery(id+"F0.wireOp",EDGE,"E185"),sQuery(id+"F0.wireOp",EDGE,"E186"),sQuery(id+"F0.wireOp",EDGE,"E187"),sQuery(id+"F0.wireOp",EDGE,"E188"),sQuery(id+"F0.wireOp",EDGE,"E189"),sQuery(id+"F0.wireOp",EDGE,"E190"),sQuery(id+"F0.wireOp",EDGE,"E191"),sQuery(id+"F0.wireOp",EDGE,"E192"),sQuery(id+"F0.wireOp",EDGE,"E193"),sQuery(id+"F0.wireOp",EDGE,"E194"),sQuery(id+"F0.wireOp",EDGE,"E195"),sQuery(id+"F0.wireOp",EDGE,"E196"),sQuery(id+"F0.wireOp",EDGE,"E197"),sQuery(id+"F0.wireOp",EDGE,"E198"),sQuery(id+"F0.wireOp",EDGE,"E199"),sQuery(id+"F0.wireOp",EDGE,"E200"),sQuery(id+"F0.wireOp",EDGE,"E201"),sQuery(id+"F0.wireOp",EDGE,"E202"),sQuery(id+"F0.wireOp",EDGE,"E203"),sQuery(id+"F0.wireOp",EDGE,"E204"),sQuery(id+"F0.wireOp",EDGE,"E205"),sQuery(id+"F0.wireOp",EDGE,"E206"),sQuery(id+"F0.wireOp",EDGE,"E207"),sQuery(id+"F0.wireOp",EDGE,"E208"),sQuery(id+"F0.wireOp",EDGE,"E209"),sQuery(id+"F0.wireOp",EDGE,"E210"),sQuery(id+"F0.wireOp",EDGE,"E211"),sQuery(id+"F0.wireOp",EDGE,"E212"),sQuery(id+"F0.wireOp",EDGE,"E213"),sQuery(id+"F0.wireOp",EDGE,"E214"),sQuery(id+"F0.wireOp",EDGE,"E215"),sQuery(id+"F0.wireOp",EDGE,"E216"),sQuery(id+"F0.wireOp",EDGE,"E217"),sQuery(id+"F0.wireOp",EDGE,"E218"),sQuery(id+"F0.wireOp",EDGE,"E219"),sQuery(id+"F0.wireOp",EDGE,"E220"),sQuery(id+"F0.wireOp",EDGE,"E221"),sQuery(id+"F0.wireOp",EDGE,"E222"),sQuery(id+"F0.wireOp",EDGE,"E223"),sQuery(id+"F0.wireOp",EDGE,"E224"),sQuery(id+"F0.wireOp",EDGE,"E225"),sQuery(id+"F0.wireOp",EDGE,"E226"),sQuery(id+"F0.wireOp",EDGE,"E227"),sQuery(id+"F0.wireOp",EDGE,"E228"),sQuery(id+"F0.wireOp",EDGE,"E229"),sQuery(id+"F0.wireOp",EDGE,"E230"),sQuery(id+"F0.wireOp",EDGE,"E231"),sQuery(id+"F0.wireOp",EDGE,"E232"),sQuery(id+"F0.wireOp",EDGE,"E233"),sQuery(id+"F0.wireOp",EDGE,"E234"),sQuery(id+"F0.wireOp",EDGE,"E235"),sQuery(id+"F0.wireOp",EDGE,"E236"),sQuery(id+"F0.wireOp",EDGE,"E237"),sQuery(id+"F0.wireOp",EDGE,"E238"),sQuery(id+"F0.wireOp",EDGE,"E239"),sQuery(id+"F0.wireOp",EDGE,"E240"),sQuery(id+"F0.wireOp",EDGE,"E241"),sQuery(id+"F0.wireOp",EDGE,"E242"),sQuery(id+"F0.wireOp",EDGE,"E243"),sQuery(id+"F0.wireOp",EDGE,"E244"),sQuery(id+"F0.wireOp",EDGE,"E245"),sQuery(id+"F0.wireOp",EDGE,"E246"),sQuery(id+"F0.wireOp",EDGE,"E247"),sQuery(id+"F0.wireOp",EDGE,"E248"),sQuery(id+"F0.wireOp",EDGE,"E249"),sQuery(id+"F0.wireOp",EDGE,"E250"),sQuery(id+"F0.wireOp",EDGE,"E251"),sQuery(id+"F0.wireOp",EDGE,"E252"),sQuery(id+"F0.wireOp",EDGE,"E253"),sQuery(id+"F0.wireOp",EDGE,"E254"),sQuery(id+"F0.wireOp",EDGE,"E255"),sQuery(id+"F0.wireOp",EDGE,"E256"),sQuery(id+"F0.wireOp",EDGE,"E257"),sQuery(id+"F0.wireOp",EDGE,"E258"),sQuery(id+"F0.wireOp",EDGE,"E259"),sQuery(id+"F0.wireOp",EDGE,"E260"),sQuery(id+"F0.wireOp",EDGE,"E261"),sQuery(id+"F0.wireOp",EDGE,"E262"),sQuery(id+"F0.wireOp",EDGE,"E263"),sQuery(id+"F0.wireOp",EDGE,"E264"),sQuery(id+"F0.wireOp",EDGE,"E265"),sQuery(id+"F0.wireOp",EDGE,"E266"),sQuery(id+"F0.wireOp",EDGE,"E267"),sQuery(id+"F0.wireOp",EDGE,"E268"),sQuery(id+"F0.wireOp",EDGE,"E269"),sQuery(id+"F0.wireOp",EDGE,"E270"),sQuery(id+"F0.wireOp",EDGE,"E271"),sQuery(id+"F0.wireOp",EDGE,"E272"),sQuery(id+"F0.wireOp",EDGE,"E273"),sQuery(id+"F0.wireOp",EDGE,"E274"),sQuery(id+"F0.wireOp",EDGE,"E275"),sQuery(id+"F0.wireOp",EDGE,"E276"),sQuery(id+"F0.wireOp",EDGE,"E277"),sQuery(id+"F0.wireOp",EDGE,"E278"),sQuery(id+"F0.wireOp",EDGE,"E279"),sQuery(id+"F0.wireOp",EDGE,"E280"),sQuery(id+"F0.wireOp",EDGE,"E281"),sQuery(id+"F0.wireOp",EDGE,"E282"),sQuery(id+"F0.wireOp",EDGE,"E283"),sQuery(id+"F0.wireOp",EDGE,"E284"),sQuery(id+"F0.wireOp",EDGE,"E285"),sQuery(id+"F0.wireOp",EDGE,"E286"),sQuery(id+"F0.wireOp",EDGE,"E287"),sQuery(id+"F0.wireOp",EDGE,"E288"),sQuery(id+"F0.wireOp",EDGE,"E289"),sQuery(id+"F0.wireOp",EDGE,"E290"),sQuery(id+"F0.wireOp",EDGE,"E291"),sQuery(id+"F0.wireOp",EDGE,"E292"),sQuery(id+"F0.wireOp",EDGE,"E293"),sQuery(id+"F0.wireOp",EDGE,"E294"),sQuery(id+"F0.wireOp",EDGE,"E295"),sQuery(id+"F0.wireOp",EDGE,"E296"),sQuery(id+"F0.wireOp",EDGE,"E297"),sQuery(id+"F0.wireOp",EDGE,"E298"),sQuery(id+"F0.wireOp",EDGE,"E299"),sQuery(id+"F0.wireOp",EDGE,"E300"),sQuery(id+"F0.wireOp",EDGE,"E301"),sQuery(id+"F0.wireOp",EDGE,"E302"),sQuery(id+"F0.wireOp",EDGE,"E303"),sQuery(id+"F0.wireOp",EDGE,"E304"),sQuery(id+"F0.wireOp",EDGE,"E305"),sQuery(id+"F0.wireOp",EDGE,"E306"),sQuery(id+"F0.wireOp",EDGE,"E307"),sQuery(id+"F0.wireOp",EDGE,"E308"),sQuery(id+"F0.wireOp",EDGE,"E309"),sQuery(id+"F0.wireOp",EDGE,"E310"),sQuery(id+"F0.wireOp",EDGE,"E311"),sQuery(id+"F0.wireOp",EDGE,"E312"),sQuery(id+"F0.wireOp",EDGE,"E313"),sQuery(id+"F0.wireOp",EDGE,"E314"),sQuery(id+"F0.wireOp",EDGE,"E315"),sQuery(id+"F0.wireOp",EDGE,"E316"),sQuery(id+"F0.wireOp",EDGE,"E317"),sQuery(id+"F0.wireOp",EDGE,"E318"),sQuery(id+"F0.wireOp",EDGE,"E319"),sQuery(id+"F0.wireOp",EDGE,"E320"),sQuery(id+"F0.wireOp",EDGE,"E321"),sQuery(id+"F0.wireOp",EDGE,"E322"),sQuery(id+"F0.wireOp",EDGE,"E323"),sQuery(id+"F0.wireOp",EDGE,"E324"),sQuery(id+"F0.wireOp",EDGE,"E325"),sQuery(id+"F0.wireOp",EDGE,"E326"),sQuery(id+"F0.wireOp",EDGE,"E327"),sQuery(id+"F0.wireOp",EDGE,"E328"),sQuery(id+"F0.wireOp",EDGE,"E329"),sQuery(id+"F0.wireOp",EDGE,"E330"),sQuery(id+"F0.wireOp",EDGE,"E331"),sQuery(id+"F0.wireOp",EDGE,"E332"),sQuery(id+"F0.wireOp",EDGE,"E333"),sQuery(id+"F0.wireOp",EDGE,"E334"),sQuery(id+"F0.wireOp",EDGE,"E335"),sQuery(id+"F0.wireOp",EDGE,"E336"),sQuery(id+"F0.wireOp",EDGE,"E337"),sQuery(id+"F0.wireOp",EDGE,"E338"),sQuery(id+"F0.wireOp",EDGE,"E339"),sQuery(id+"F0.wireOp",EDGE,"E340"),sQuery(id+"F0.wireOp",EDGE,"E341"),sQuery(id+"F0.wireOp",EDGE,"E342"),sQuery(id+"F0.wireOp",EDGE,"E343"),sQuery(id+"F0.wireOp",EDGE,"E344"),sQuery(id+"F0.wireOp",EDGE,"E345"),sQuery(id+"F0.wireOp",EDGE,"E346"),sQuery(id+"F0.wireOp",EDGE,"E347"),sQuery(id+"F0.wireOp",EDGE,"E348"),sQuery(id+"F0.wireOp",EDGE,"E349"),sQuery(id+"F0.wireOp",EDGE,"E350"),sQuery(id+"F0.wireOp",EDGE,"E351"),sQuery(id+"F0.wireOp",EDGE,"E352"),sQuery(id+"F0.wireOp",EDGE,"E353"),sQuery(id+"F0.wireOp",EDGE,"E354"),sQuery(id+"F0.wireOp",EDGE,"E355"),sQuery(id+"F0.wireOp",EDGE,"E356"),sQuery(id+"F0.wireOp",EDGE,"E357"),sQuery(id+"F0.wireOp",EDGE,"E358"),sQuery(id+"F0.wireOp",EDGE,"E359"),sQuery(id+"F0.wireOp",EDGE,"E360"),sQuery(id+"F0.wireOp",EDGE,"E361"),sQuery(id+"F0.wireOp",EDGE,"E362"),sQuery(id+"F0.wireOp",EDGE,"E363"),sQuery(id+"F0.wireOp",EDGE,"E364"),sQuery(id+"F0.wireOp",EDGE,"E365"),sQuery(id+"F0.wireOp",EDGE,"E366"),sQuery(id+"F0.wireOp",EDGE,"E367"),sQuery(id+"F0.wireOp",EDGE,"E368"),sQuery(id+"F0.wireOp",EDGE,"E369"),sQuery(id+"F0.wireOp",EDGE,"E370"),sQuery(id+"F0.wireOp",EDGE,"E371"),sQuery(id+"F0.wireOp",EDGE,"E372"),sQuery(id+"F0.wireOp",EDGE,"E373"),sQuery(id+"F0.wireOp",EDGE,"E374"),sQuery(id+"F0.wireOp",EDGE,"E375"),sQuery(id+"F0.wireOp",EDGE,"E376"),sQuery(id+"F0.wireOp",EDGE,"E377"),sQuery(id+"F0.wireOp",EDGE,"E378"),sQuery(id+"F0.wireOp",EDGE,"E379"),sQuery(id+"F0.wireOp",EDGE,"E380"),sQuery(id+"F0.wireOp",EDGE,"E381"),sQuery(id+"F0.wireOp",EDGE,"E382"),sQuery(id+"F0.wireOp",EDGE,"E383"),sQuery(id+"F0.wireOp",EDGE,"E384"),sQuery(id+"F0.wireOp",EDGE,"E385"),sQuery(id+"F0.wireOp",EDGE,"E386"),sQuery(id+"F0.wireOp",EDGE,"E387"),sQuery(id+"F0.wireOp",EDGE,"E388"),sQuery(id+"F0.wireOp",EDGE,"E389"),sQuery(id+"F0.wireOp",EDGE,"E390"),sQuery(id+"F0.wireOp",EDGE,"E391"),sQuery(id+"F0.wireOp",EDGE,"E392"),sQuery(id+"F0.wireOp",EDGE,"E393"),sQuery(id+"F0.wireOp",EDGE,"E394"),sQuery(id+"F0.wireOp",EDGE,"E395"),sQuery(id+"F0.wireOp",EDGE,"E396"),sQuery(id+"F0.wireOp",EDGE,"E397"),sQuery(id+"F0.wireOp",EDGE,"E398"),sQuery(id+"F0.wireOp",EDGE,"E399"),sQuery(id+"F0.wireOp",EDGE,"E400"),sQuery(id+"F0.wireOp",EDGE,"E401"),sQuery(id+"F0.wireOp",EDGE,"E402"),sQuery(id+"F0.wireOp",EDGE,"E403"),sQuery(id+"F0.wireOp",EDGE,"E404"),sQuery(id+"F0.wireOp",EDGE,"E405"),sQuery(id+"F0.wireOp",EDGE,"E406"),sQuery(id+"F0.wireOp",EDGE,"E407"),sQuery(id+"F0.wireOp",EDGE,"E408"),sQuery(id+"F0.wireOp",EDGE,"E409"),sQuery(id+"F0.wireOp",EDGE,"E410"),sQuery(id+"F0.wireOp",EDGE,"E411"),sQuery(id+"F0.wireOp",EDGE,"E412"),sQuery(id+"F0.wireOp",EDGE,"E413"),sQuery(id+"F0.wireOp",EDGE,"E414"),sQuery(id+"F0.wireOp",EDGE,"E415"),sQuery(id+"F0.wireOp",EDGE,"E416"),sQuery(id+"F0.wireOp",EDGE,"E417"),sQuery(id+"F0.wireOp",EDGE,"E418"),sQuery(id+"F0.wireOp",EDGE,"E419"),sQuery(id+"F0.wireOp",EDGE,"E420"),sQuery(id+"F0.wireOp",EDGE,"E421"),sQuery(id+"F0.wireOp",EDGE,"E422"),sQuery(id+"F0.wireOp",EDGE,"E423"),sQuery(id+"F0.wireOp",EDGE,"E424"),sQuery(id+"F0.wireOp",EDGE,"E425"),sQuery(id+"F0.wireOp",EDGE,"E426"),sQuery(id+"F0.wireOp",EDGE,"E427"),sQuery(id+"F0.wireOp",EDGE,"E428"),sQuery(id+"F0.wireOp",EDGE,"E429"),sQuery(id+"F0.wireOp",EDGE,"E430"),sQuery(id+"F0.wireOp",EDGE,"E431"),sQuery(id+"F0.wireOp",EDGE,"E432"),sQuery(id+"F0.wireOp",EDGE,"E433"),sQuery(id+"F0.wireOp",EDGE,"E434"),sQuery(id+"F0.wireOp",EDGE,"E435"),sQuery(id+"F0.wireOp",EDGE,"E436"),sQuery(id+"F0.wireOp",EDGE,"E437"),sQuery(id+"F0.wireOp",EDGE,"E438"),sQuery(id+"F0.wireOp",EDGE,"E439"),sQuery(id+"F0.wireOp",EDGE,"E440"),sQuery(id+"F0.wireOp",EDGE,"E490"),sQuery(id+"F0.wireOp",EDGE,"E492"),sQuery(id+"F0.wireOp",EDGE,"E494"),sQuery(id+"F0.wireOp",EDGE,"E496"),sQuery(id+"F0.wireOp",EDGE,"E498"),sQuery(id+"F0.wireOp",EDGE,"E499"),sQuery(id+"F0.wireOp",EDGE,"E500"),sQuery(id+"F0.wireOp",EDGE,"E501"),sQuery(id+"F0.wireOp",EDGE,"E502"),sQuery(id+"F0.wireOp",EDGE,"E503"),sQuery(id+"F0.wireOp",EDGE,"E506")])]});
            var Q1;
            Q1=qCreatedBy(makeId("Origin.pointOp"),VERTEX);
            transform(context, id + "F2", {"entities" : qUnion([Q0]), "transformType" : TransformType.SCALE_UNIFORMLY, "scale" : .6, "makeCopy" : false, "scalePoint" : qUnion([Q1])});
        }
        {
            var Q0;
            Q0=makeQuery(id+"F1.opExtrude","CAP_FACE",FACE,{"disambiguationData":[OSD([sQuery(id+"F0.wireOp",EDGE,"E0"),sQuery(id+"F0.wireOp",EDGE,"E1"),sQuery(id+"F0.wireOp",EDGE,"E2"),sQuery(id+"F0.wireOp",EDGE,"E3"),sQuery(id+"F0.wireOp",EDGE,"E4"),sQuery(id+"F0.wireOp",EDGE,"E5"),sQuery(id+"F0.wireOp",EDGE,"E6"),sQuery(id+"F0.wireOp",EDGE,"E7"),sQuery(id+"F0.wireOp",EDGE,"E8"),sQuery(id+"F0.wireOp",EDGE,"E9"),sQuery(id+"F0.wireOp",EDGE,"E10"),sQuery(id+"F0.wireOp",EDGE,"E11"),sQuery(id+"F0.wireOp",EDGE,"E12"),sQuery(id+"F0.wireOp",EDGE,"E13"),sQuery(id+"F0.wireOp",EDGE,"E14"),sQuery(id+"F0.wireOp",EDGE,"E15"),sQuery(id+"F0.wireOp",EDGE,"E16"),sQuery(id+"F0.wireOp",EDGE,"E17"),sQuery(id+"F0.wireOp",EDGE,"E18"),sQuery(id+"F0.wireOp",EDGE,"E19"),sQuery(id+"F0.wireOp",EDGE,"E20"),sQuery(id+"F0.wireOp",EDGE,"E21"),sQuery(id+"F0.wireOp",EDGE,"E22"),sQuery(id+"F0.wireOp",EDGE,"E23"),sQuery(id+"F0.wireOp",EDGE,"E24"),sQuery(id+"F0.wireOp",EDGE,"E25"),sQuery(id+"F0.wireOp",EDGE,"E26"),sQuery(id+"F0.wireOp",EDGE,"E27"),sQuery(id+"F0.wireOp",EDGE,"E28"),sQuery(id+"F0.wireOp",EDGE,"E29"),sQuery(id+"F0.wireOp",EDGE,"E30"),sQuery(id+"F0.wireOp",EDGE,"E31"),sQuery(id+"F0.wireOp",EDGE,"E32"),sQuery(id+"F0.wireOp",EDGE,"E33"),sQuery(id+"F0.wireOp",EDGE,"E34"),sQuery(id+"F0.wireOp",EDGE,"E35"),sQuery(id+"F0.wireOp",EDGE,"E36"),sQuery(id+"F0.wireOp",EDGE,"E37"),sQuery(id+"F0.wireOp",EDGE,"E38"),sQuery(id+"F0.wireOp",EDGE,"E39"),sQuery(id+"F0.wireOp",EDGE,"E40"),sQuery(id+"F0.wireOp",EDGE,"E41"),sQuery(id+"F0.wireOp",EDGE,"E42"),sQuery(id+"F0.wireOp",EDGE,"E43"),sQuery(id+"F0.wireOp",EDGE,"E44"),sQuery(id+"F0.wireOp",EDGE,"E45"),sQuery(id+"F0.wireOp",EDGE,"E46"),sQuery(id+"F0.wireOp",EDGE,"E47"),sQuery(id+"F0.wireOp",EDGE,"E48"),sQuery(id+"F0.wireOp",EDGE,"E49"),sQuery(id+"F0.wireOp",EDGE,"E50"),sQuery(id+"F0.wireOp",EDGE,"E51"),sQuery(id+"F0.wireOp",EDGE,"E52"),sQuery(id+"F0.wireOp",EDGE,"E53"),sQuery(id+"F0.wireOp",EDGE,"E54"),sQuery(id+"F0.wireOp",EDGE,"E55"),sQuery(id+"F0.wireOp",EDGE,"E56"),sQuery(id+"F0.wireOp",EDGE,"E57"),sQuery(id+"F0.wireOp",EDGE,"E58"),sQuery(id+"F0.wireOp",EDGE,"E59"),sQuery(id+"F0.wireOp",EDGE,"E60"),sQuery(id+"F0.wireOp",EDGE,"E61"),sQuery(id+"F0.wireOp",EDGE,"E62"),sQuery(id+"F0.wireOp",EDGE,"E63"),sQuery(id+"F0.wireOp",EDGE,"E64"),sQuery(id+"F0.wireOp",EDGE,"E65"),sQuery(id+"F0.wireOp",EDGE,"E66"),sQuery(id+"F0.wireOp",EDGE,"E67"),sQuery(id+"F0.wireOp",EDGE,"E68"),sQuery(id+"F0.wireOp",EDGE,"E69"),sQuery(id+"F0.wireOp",EDGE,"E70"),sQuery(id+"F0.wireOp",EDGE,"E71"),sQuery(id+"F0.wireOp",EDGE,"E72"),sQuery(id+"F0.wireOp",EDGE,"E73"),sQuery(id+"F0.wireOp",EDGE,"E74"),sQuery(id+"F0.wireOp",EDGE,"E75"),sQuery(id+"F0.wireOp",EDGE,"E76"),sQuery(id+"F0.wireOp",EDGE,"E77"),sQuery(id+"F0.wireOp",EDGE,"E78"),sQuery(id+"F0.wireOp",EDGE,"E79"),sQuery(id+"F0.wireOp",EDGE,"E80"),sQuery(id+"F0.wireOp",EDGE,"E81"),sQuery(id+"F0.wireOp",EDGE,"E82"),sQuery(id+"F0.wireOp",EDGE,"E83"),sQuery(id+"F0.wireOp",EDGE,"E84"),sQuery(id+"F0.wireOp",EDGE,"E85"),sQuery(id+"F0.wireOp",EDGE,"E86"),sQuery(id+"F0.wireOp",EDGE,"E87"),sQuery(id+"F0.wireOp",EDGE,"E88"),sQuery(id+"F0.wireOp",EDGE,"E89"),sQuery(id+"F0.wireOp",EDGE,"E90"),sQuery(id+"F0.wireOp",EDGE,"E91"),sQuery(id+"F0.wireOp",EDGE,"E92"),sQuery(id+"F0.wireOp",EDGE,"E93"),sQuery(id+"F0.wireOp",EDGE,"E94"),sQuery(id+"F0.wireOp",EDGE,"E95"),sQuery(id+"F0.wireOp",EDGE,"E96"),sQuery(id+"F0.wireOp",EDGE,"E97"),sQuery(id+"F0.wireOp",EDGE,"E98"),sQuery(id+"F0.wireOp",EDGE,"E99"),sQuery(id+"F0.wireOp",EDGE,"E100"),sQuery(id+"F0.wireOp",EDGE,"E101"),sQuery(id+"F0.wireOp",EDGE,"E102"),sQuery(id+"F0.wireOp",EDGE,"E103"),sQuery(id+"F0.wireOp",EDGE,"E104"),sQuery(id+"F0.wireOp",EDGE,"E105"),sQuery(id+"F0.wireOp",EDGE,"E106"),sQuery(id+"F0.wireOp",EDGE,"E107"),sQuery(id+"F0.wireOp",EDGE,"E108"),sQuery(id+"F0.wireOp",EDGE,"E109"),sQuery(id+"F0.wireOp",EDGE,"E110"),sQuery(id+"F0.wireOp",EDGE,"E111"),sQuery(id+"F0.wireOp",EDGE,"E112"),sQuery(id+"F0.wireOp",EDGE,"E113"),sQuery(id+"F0.wireOp",EDGE,"E114"),sQuery(id+"F0.wireOp",EDGE,"E115"),sQuery(id+"F0.wireOp",EDGE,"E116"),sQuery(id+"F0.wireOp",EDGE,"E117"),sQuery(id+"F0.wireOp",EDGE,"E118"),sQuery(id+"F0.wireOp",EDGE,"E119"),sQuery(id+"F0.wireOp",EDGE,"E120"),sQuery(id+"F0.wireOp",EDGE,"E121"),sQuery(id+"F0.wireOp",EDGE,"E122"),sQuery(id+"F0.wireOp",EDGE,"E123"),sQuery(id+"F0.wireOp",EDGE,"E124"),sQuery(id+"F0.wireOp",EDGE,"E125"),sQuery(id+"F0.wireOp",EDGE,"E126"),sQuery(id+"F0.wireOp",EDGE,"E127"),sQuery(id+"F0.wireOp",EDGE,"E128"),sQuery(id+"F0.wireOp",EDGE,"E129"),sQuery(id+"F0.wireOp",EDGE,"E130"),sQuery(id+"F0.wireOp",EDGE,"E131"),sQuery(id+"F0.wireOp",EDGE,"E132"),sQuery(id+"F0.wireOp",EDGE,"E133"),sQuery(id+"F0.wireOp",EDGE,"E134"),sQuery(id+"F0.wireOp",EDGE,"E135"),sQuery(id+"F0.wireOp",EDGE,"E136"),sQuery(id+"F0.wireOp",EDGE,"E137"),sQuery(id+"F0.wireOp",EDGE,"E138"),sQuery(id+"F0.wireOp",EDGE,"E139"),sQuery(id+"F0.wireOp",EDGE,"E140"),sQuery(id+"F0.wireOp",EDGE,"E141"),sQuery(id+"F0.wireOp",EDGE,"E142"),sQuery(id+"F0.wireOp",EDGE,"E143"),sQuery(id+"F0.wireOp",EDGE,"E144"),sQuery(id+"F0.wireOp",EDGE,"E145"),sQuery(id+"F0.wireOp",EDGE,"E146"),sQuery(id+"F0.wireOp",EDGE,"E147"),sQuery(id+"F0.wireOp",EDGE,"E148"),sQuery(id+"F0.wireOp",EDGE,"E149"),sQuery(id+"F0.wireOp",EDGE,"E150"),sQuery(id+"F0.wireOp",EDGE,"E151"),sQuery(id+"F0.wireOp",EDGE,"E152"),sQuery(id+"F0.wireOp",EDGE,"E153"),sQuery(id+"F0.wireOp",EDGE,"E154"),sQuery(id+"F0.wireOp",EDGE,"E155"),sQuery(id+"F0.wireOp",EDGE,"E156"),sQuery(id+"F0.wireOp",EDGE,"E157"),sQuery(id+"F0.wireOp",EDGE,"E158"),sQuery(id+"F0.wireOp",EDGE,"E159"),sQuery(id+"F0.wireOp",EDGE,"E160"),sQuery(id+"F0.wireOp",EDGE,"E161"),sQuery(id+"F0.wireOp",EDGE,"E162"),sQuery(id+"F0.wireOp",EDGE,"E163"),sQuery(id+"F0.wireOp",EDGE,"E164"),sQuery(id+"F0.wireOp",EDGE,"E165"),sQuery(id+"F0.wireOp",EDGE,"E166"),sQuery(id+"F0.wireOp",EDGE,"E167"),sQuery(id+"F0.wireOp",EDGE,"E168"),sQuery(id+"F0.wireOp",EDGE,"E169"),sQuery(id+"F0.wireOp",EDGE,"E170"),sQuery(id+"F0.wireOp",EDGE,"E171"),sQuery(id+"F0.wireOp",EDGE,"E172"),sQuery(id+"F0.wireOp",EDGE,"E173"),sQuery(id+"F0.wireOp",EDGE,"E174"),sQuery(id+"F0.wireOp",EDGE,"E175"),sQuery(id+"F0.wireOp",EDGE,"E176"),sQuery(id+"F0.wireOp",EDGE,"E177"),sQuery(id+"F0.wireOp",EDGE,"E178"),sQuery(id+"F0.wireOp",EDGE,"E179"),sQuery(id+"F0.wireOp",EDGE,"E180"),sQuery(id+"F0.wireOp",EDGE,"E181"),sQuery(id+"F0.wireOp",EDGE,"E182"),sQuery(id+"F0.wireOp",EDGE,"E183"),sQuery(id+"F0.wireOp",EDGE,"E184"),sQuery(id+"F0.wireOp",EDGE,"E185"),sQuery(id+"F0.wireOp",EDGE,"E186"),sQuery(id+"F0.wireOp",EDGE,"E187"),sQuery(id+"F0.wireOp",EDGE,"E188"),sQuery(id+"F0.wireOp",EDGE,"E189"),sQuery(id+"F0.wireOp",EDGE,"E190"),sQuery(id+"F0.wireOp",EDGE,"E191"),sQuery(id+"F0.wireOp",EDGE,"E192"),sQuery(id+"F0.wireOp",EDGE,"E193"),sQuery(id+"F0.wireOp",EDGE,"E194"),sQuery(id+"F0.wireOp",EDGE,"E195"),sQuery(id+"F0.wireOp",EDGE,"E196"),sQuery(id+"F0.wireOp",EDGE,"E197"),sQuery(id+"F0.wireOp",EDGE,"E198"),sQuery(id+"F0.wireOp",EDGE,"E199"),sQuery(id+"F0.wireOp",EDGE,"E200"),sQuery(id+"F0.wireOp",EDGE,"E201"),sQuery(id+"F0.wireOp",EDGE,"E202"),sQuery(id+"F0.wireOp",EDGE,"E203"),sQuery(id+"F0.wireOp",EDGE,"E204"),sQuery(id+"F0.wireOp",EDGE,"E205"),sQuery(id+"F0.wireOp",EDGE,"E206"),sQuery(id+"F0.wireOp",EDGE,"E207"),sQuery(id+"F0.wireOp",EDGE,"E208"),sQuery(id+"F0.wireOp",EDGE,"E209"),sQuery(id+"F0.wireOp",EDGE,"E210"),sQuery(id+"F0.wireOp",EDGE,"E211"),sQuery(id+"F0.wireOp",EDGE,"E212"),sQuery(id+"F0.wireOp",EDGE,"E213"),sQuery(id+"F0.wireOp",EDGE,"E214"),sQuery(id+"F0.wireOp",EDGE,"E215"),sQuery(id+"F0.wireOp",EDGE,"E216"),sQuery(id+"F0.wireOp",EDGE,"E217"),sQuery(id+"F0.wireOp",EDGE,"E218"),sQuery(id+"F0.wireOp",EDGE,"E219"),sQuery(id+"F0.wireOp",EDGE,"E220"),sQuery(id+"F0.wireOp",EDGE,"E221"),sQuery(id+"F0.wireOp",EDGE,"E222"),sQuery(id+"F0.wireOp",EDGE,"E223"),sQuery(id+"F0.wireOp",EDGE,"E224"),sQuery(id+"F0.wireOp",EDGE,"E225"),sQuery(id+"F0.wireOp",EDGE,"E226"),sQuery(id+"F0.wireOp",EDGE,"E227"),sQuery(id+"F0.wireOp",EDGE,"E228"),sQuery(id+"F0.wireOp",EDGE,"E229"),sQuery(id+"F0.wireOp",EDGE,"E230"),sQuery(id+"F0.wireOp",EDGE,"E231"),sQuery(id+"F0.wireOp",EDGE,"E232"),sQuery(id+"F0.wireOp",EDGE,"E233"),sQuery(id+"F0.wireOp",EDGE,"E234"),sQuery(id+"F0.wireOp",EDGE,"E235"),sQuery(id+"F0.wireOp",EDGE,"E236"),sQuery(id+"F0.wireOp",EDGE,"E237"),sQuery(id+"F0.wireOp",EDGE,"E238"),sQuery(id+"F0.wireOp",EDGE,"E239"),sQuery(id+"F0.wireOp",EDGE,"E240"),sQuery(id+"F0.wireOp",EDGE,"E241"),sQuery(id+"F0.wireOp",EDGE,"E242"),sQuery(id+"F0.wireOp",EDGE,"E243"),sQuery(id+"F0.wireOp",EDGE,"E244"),sQuery(id+"F0.wireOp",EDGE,"E245"),sQuery(id+"F0.wireOp",EDGE,"E246"),sQuery(id+"F0.wireOp",EDGE,"E247"),sQuery(id+"F0.wireOp",EDGE,"E248"),sQuery(id+"F0.wireOp",EDGE,"E249"),sQuery(id+"F0.wireOp",EDGE,"E250"),sQuery(id+"F0.wireOp",EDGE,"E251"),sQuery(id+"F0.wireOp",EDGE,"E252"),sQuery(id+"F0.wireOp",EDGE,"E253"),sQuery(id+"F0.wireOp",EDGE,"E254"),sQuery(id+"F0.wireOp",EDGE,"E255"),sQuery(id+"F0.wireOp",EDGE,"E256"),sQuery(id+"F0.wireOp",EDGE,"E257"),sQuery(id+"F0.wireOp",EDGE,"E258"),sQuery(id+"F0.wireOp",EDGE,"E259"),sQuery(id+"F0.wireOp",EDGE,"E260"),sQuery(id+"F0.wireOp",EDGE,"E261"),sQuery(id+"F0.wireOp",EDGE,"E262"),sQuery(id+"F0.wireOp",EDGE,"E263"),sQuery(id+"F0.wireOp",EDGE,"E264"),sQuery(id+"F0.wireOp",EDGE,"E265"),sQuery(id+"F0.wireOp",EDGE,"E266"),sQuery(id+"F0.wireOp",EDGE,"E267"),sQuery(id+"F0.wireOp",EDGE,"E268"),sQuery(id+"F0.wireOp",EDGE,"E269"),sQuery(id+"F0.wireOp",EDGE,"E270"),sQuery(id+"F0.wireOp",EDGE,"E271"),sQuery(id+"F0.wireOp",EDGE,"E272"),sQuery(id+"F0.wireOp",EDGE,"E273"),sQuery(id+"F0.wireOp",EDGE,"E274"),sQuery(id+"F0.wireOp",EDGE,"E275"),sQuery(id+"F0.wireOp",EDGE,"E276"),sQuery(id+"F0.wireOp",EDGE,"E277"),sQuery(id+"F0.wireOp",EDGE,"E278"),sQuery(id+"F0.wireOp",EDGE,"E279"),sQuery(id+"F0.wireOp",EDGE,"E280"),sQuery(id+"F0.wireOp",EDGE,"E281"),sQuery(id+"F0.wireOp",EDGE,"E282"),sQuery(id+"F0.wireOp",EDGE,"E283"),sQuery(id+"F0.wireOp",EDGE,"E284"),sQuery(id+"F0.wireOp",EDGE,"E285"),sQuery(id+"F0.wireOp",EDGE,"E286"),sQuery(id+"F0.wireOp",EDGE,"E287"),sQuery(id+"F0.wireOp",EDGE,"E288"),sQuery(id+"F0.wireOp",EDGE,"E289"),sQuery(id+"F0.wireOp",EDGE,"E290"),sQuery(id+"F0.wireOp",EDGE,"E291"),sQuery(id+"F0.wireOp",EDGE,"E292"),sQuery(id+"F0.wireOp",EDGE,"E293"),sQuery(id+"F0.wireOp",EDGE,"E294"),sQuery(id+"F0.wireOp",EDGE,"E295"),sQuery(id+"F0.wireOp",EDGE,"E296"),sQuery(id+"F0.wireOp",EDGE,"E297"),sQuery(id+"F0.wireOp",EDGE,"E298"),sQuery(id+"F0.wireOp",EDGE,"E299"),sQuery(id+"F0.wireOp",EDGE,"E300"),sQuery(id+"F0.wireOp",EDGE,"E301"),sQuery(id+"F0.wireOp",EDGE,"E302"),sQuery(id+"F0.wireOp",EDGE,"E303"),sQuery(id+"F0.wireOp",EDGE,"E304"),sQuery(id+"F0.wireOp",EDGE,"E305"),sQuery(id+"F0.wireOp",EDGE,"E306"),sQuery(id+"F0.wireOp",EDGE,"E307"),sQuery(id+"F0.wireOp",EDGE,"E308"),sQuery(id+"F0.wireOp",EDGE,"E309"),sQuery(id+"F0.wireOp",EDGE,"E310"),sQuery(id+"F0.wireOp",EDGE,"E311"),sQuery(id+"F0.wireOp",EDGE,"E312"),sQuery(id+"F0.wireOp",EDGE,"E313"),sQuery(id+"F0.wireOp",EDGE,"E314"),sQuery(id+"F0.wireOp",EDGE,"E315"),sQuery(id+"F0.wireOp",EDGE,"E316"),sQuery(id+"F0.wireOp",EDGE,"E317"),sQuery(id+"F0.wireOp",EDGE,"E318"),sQuery(id+"F0.wireOp",EDGE,"E319"),sQuery(id+"F0.wireOp",EDGE,"E320"),sQuery(id+"F0.wireOp",EDGE,"E321"),sQuery(id+"F0.wireOp",EDGE,"E322"),sQuery(id+"F0.wireOp",EDGE,"E323"),sQuery(id+"F0.wireOp",EDGE,"E324"),sQuery(id+"F0.wireOp",EDGE,"E325"),sQuery(id+"F0.wireOp",EDGE,"E326"),sQuery(id+"F0.wireOp",EDGE,"E327"),sQuery(id+"F0.wireOp",EDGE,"E328"),sQuery(id+"F0.wireOp",EDGE,"E329"),sQuery(id+"F0.wireOp",EDGE,"E330"),sQuery(id+"F0.wireOp",EDGE,"E331"),sQuery(id+"F0.wireOp",EDGE,"E332"),sQuery(id+"F0.wireOp",EDGE,"E333"),sQuery(id+"F0.wireOp",EDGE,"E334"),sQuery(id+"F0.wireOp",EDGE,"E335"),sQuery(id+"F0.wireOp",EDGE,"E336"),sQuery(id+"F0.wireOp",EDGE,"E337"),sQuery(id+"F0.wireOp",EDGE,"E338"),sQuery(id+"F0.wireOp",EDGE,"E339"),sQuery(id+"F0.wireOp",EDGE,"E340"),sQuery(id+"F0.wireOp",EDGE,"E341"),sQuery(id+"F0.wireOp",EDGE,"E342"),sQuery(id+"F0.wireOp",EDGE,"E343"),sQuery(id+"F0.wireOp",EDGE,"E344"),sQuery(id+"F0.wireOp",EDGE,"E345"),sQuery(id+"F0.wireOp",EDGE,"E346"),sQuery(id+"F0.wireOp",EDGE,"E347"),sQuery(id+"F0.wireOp",EDGE,"E348"),sQuery(id+"F0.wireOp",EDGE,"E349"),sQuery(id+"F0.wireOp",EDGE,"E350"),sQuery(id+"F0.wireOp",EDGE,"E351"),sQuery(id+"F0.wireOp",EDGE,"E352"),sQuery(id+"F0.wireOp",EDGE,"E353"),sQuery(id+"F0.wireOp",EDGE,"E354"),sQuery(id+"F0.wireOp",EDGE,"E355"),sQuery(id+"F0.wireOp",EDGE,"E356"),sQuery(id+"F0.wireOp",EDGE,"E357"),sQuery(id+"F0.wireOp",EDGE,"E358"),sQuery(id+"F0.wireOp",EDGE,"E359"),sQuery(id+"F0.wireOp",EDGE,"E360"),sQuery(id+"F0.wireOp",EDGE,"E361"),sQuery(id+"F0.wireOp",EDGE,"E362"),sQuery(id+"F0.wireOp",EDGE,"E363"),sQuery(id+"F0.wireOp",EDGE,"E364"),sQuery(id+"F0.wireOp",EDGE,"E365"),sQuery(id+"F0.wireOp",EDGE,"E366"),sQuery(id+"F0.wireOp",EDGE,"E367"),sQuery(id+"F0.wireOp",EDGE,"E368"),sQuery(id+"F0.wireOp",EDGE,"E369"),sQuery(id+"F0.wireOp",EDGE,"E370"),sQuery(id+"F0.wireOp",EDGE,"E371"),sQuery(id+"F0.wireOp",EDGE,"E372"),sQuery(id+"F0.wireOp",EDGE,"E373"),sQuery(id+"F0.wireOp",EDGE,"E374"),sQuery(id+"F0.wireOp",EDGE,"E375"),sQuery(id+"F0.wireOp",EDGE,"E376"),sQuery(id+"F0.wireOp",EDGE,"E377"),sQuery(id+"F0.wireOp",EDGE,"E378"),sQuery(id+"F0.wireOp",EDGE,"E379"),sQuery(id+"F0.wireOp",EDGE,"E380"),sQuery(id+"F0.wireOp",EDGE,"E381"),sQuery(id+"F0.wireOp",EDGE,"E382"),sQuery(id+"F0.wireOp",EDGE,"E383"),sQuery(id+"F0.wireOp",EDGE,"E384"),sQuery(id+"F0.wireOp",EDGE,"E385"),sQuery(id+"F0.wireOp",EDGE,"E386"),sQuery(id+"F0.wireOp",EDGE,"E387"),sQuery(id+"F0.wireOp",EDGE,"E388"),sQuery(id+"F0.wireOp",EDGE,"E389"),sQuery(id+"F0.wireOp",EDGE,"E390"),sQuery(id+"F0.wireOp",EDGE,"E391"),sQuery(id+"F0.wireOp",EDGE,"E392"),sQuery(id+"F0.wireOp",EDGE,"E393"),sQuery(id+"F0.wireOp",EDGE,"E394"),sQuery(id+"F0.wireOp",EDGE,"E395"),sQuery(id+"F0.wireOp",EDGE,"E396"),sQuery(id+"F0.wireOp",EDGE,"E397"),sQuery(id+"F0.wireOp",EDGE,"E398"),sQuery(id+"F0.wireOp",EDGE,"E399"),sQuery(id+"F0.wireOp",EDGE,"E400"),sQuery(id+"F0.wireOp",EDGE,"E401"),sQuery(id+"F0.wireOp",EDGE,"E402"),sQuery(id+"F0.wireOp",EDGE,"E403"),sQuery(id+"F0.wireOp",EDGE,"E404"),sQuery(id+"F0.wireOp",EDGE,"E405"),sQuery(id+"F0.wireOp",EDGE,"E406"),sQuery(id+"F0.wireOp",EDGE,"E407"),sQuery(id+"F0.wireOp",EDGE,"E408"),sQuery(id+"F0.wireOp",EDGE,"E409"),sQuery(id+"F0.wireOp",EDGE,"E410"),sQuery(id+"F0.wireOp",EDGE,"E411"),sQuery(id+"F0.wireOp",EDGE,"E412"),sQuery(id+"F0.wireOp",EDGE,"E413"),sQuery(id+"F0.wireOp",EDGE,"E414"),sQuery(id+"F0.wireOp",EDGE,"E415"),sQuery(id+"F0.wireOp",EDGE,"E416"),sQuery(id+"F0.wireOp",EDGE,"E417"),sQuery(id+"F0.wireOp",EDGE,"E418"),sQuery(id+"F0.wireOp",EDGE,"E419"),sQuery(id+"F0.wireOp",EDGE,"E420"),sQuery(id+"F0.wireOp",EDGE,"E421"),sQuery(id+"F0.wireOp",EDGE,"E422"),sQuery(id+"F0.wireOp",EDGE,"E423"),sQuery(id+"F0.wireOp",EDGE,"E424"),sQuery(id+"F0.wireOp",EDGE,"E425"),sQuery(id+"F0.wireOp",EDGE,"E426"),sQuery(id+"F0.wireOp",EDGE,"E427"),sQuery(id+"F0.wireOp",EDGE,"E428"),sQuery(id+"F0.wireOp",EDGE,"E429"),sQuery(id+"F0.wireOp",EDGE,"E430"),sQuery(id+"F0.wireOp",EDGE,"E431"),sQuery(id+"F0.wireOp",EDGE,"E432"),sQuery(id+"F0.wireOp",EDGE,"E433"),sQuery(id+"F0.wireOp",EDGE,"E434"),sQuery(id+"F0.wireOp",EDGE,"E435"),sQuery(id+"F0.wireOp",EDGE,"E436"),sQuery(id+"F0.wireOp",EDGE,"E437"),sQuery(id+"F0.wireOp",EDGE,"E438"),sQuery(id+"F0.wireOp",EDGE,"E439"),sQuery(id+"F0.wireOp",EDGE,"E440"),sQuery(id+"F0.wireOp",EDGE,"E490"),sQuery(id+"F0.wireOp",EDGE,"E492"),sQuery(id+"F0.wireOp",EDGE,"E494"),sQuery(id+"F0.wireOp",EDGE,"E496"),sQuery(id+"F0.wireOp",EDGE,"E498"),sQuery(id+"F0.wireOp",EDGE,"E499"),sQuery(id+"F0.wireOp",EDGE,"E500"),sQuery(id+"F0.wireOp",EDGE,"E501"),sQuery(id+"F0.wireOp",EDGE,"E502"),sQuery(id+"F0.wireOp",EDGE,"E503"),sQuery(id+"F0.wireOp",EDGE,"E506")])],"isStart":false});
            cPlane(context, id + "F3", {"entities" : qUnion([Q0]), "cplaneType" : CPlaneType.OFFSET, "offset" : 10.8 * mm, "width" : 150 * mm, "height" : 150 * mm});
        }
        {
            var Q0;
            Q0=qCreatedBy(id+"F3.planeOp",FACE);
            var sketch = newSketch(context, id + "F4", { "sketchPlane" : qUnion([Q0])});
            skArc(sketch, "E512", {"start": v(21, -0.33) * mm, "mid": v(21, -0.17) * mm, "end": v(21, 0) * mm});
            skArc(sketch, "E513", {"start": v(0, -5) * mm, "mid": v(5, 0) * mm, "end": v(0, 5) * mm});
            skArc(sketch, "E514", {"start": v(-21, 0) * mm, "mid": v(-21, -0.17) * mm, "end": v(-21, -0.33) * mm});
            skArc(sketch, "E515", {"start": v(18.87, 1.14) * mm, "mid": v(18.84, 1.48) * mm, "end": v(18.81, 1.83) * mm});
            skArc(sketch, "E516", {"start": v(19.04, 2.15) * mm, "mid": v(18.86, 2.03) * mm, "end": v(18.81, 1.83) * mm});
            skLineSegment(sketch, "E517", {"start": v(19.04, 2.15) * mm, "end": v(19.86, 2.36) * mm});
            skArc(sketch, "E518", {"start": v(19.14, -0.86) * mm, "mid": v(18.95, -0.95) * mm, "end": v(18.87, -1.14) * mm});
            skLineSegment(sketch, "E519", {"start": v(19.86, 2.36) * mm, "end": v(20.8, 2.96) * mm});
            skArc(sketch, "E520", {"start": v(18.46, 4.07) * mm, "mid": v(18.38, 4.41) * mm, "end": v(18.3, 4.75) * mm});
            skLineSegment(sketch, "E521", {"start": v(19.14, -0.86) * mm, "end": v(19.98, -0.78) * mm});
            skArc(sketch, "E522", {"start": v(18.46, 5.1) * mm, "mid": v(18.31, 4.96) * mm, "end": v(18.3, 4.75) * mm});
            skLineSegment(sketch, "E523", {"start": v(19.98, -0.78) * mm, "end": v(21, -0.33) * mm});
            skLineSegment(sketch, "E524", {"start": v(18.46, 5.1) * mm, "end": v(19.25, 5.44) * mm});
            skArc(sketch, "E525", {"start": v(18.77, -3.84) * mm, "mid": v(18.57, -3.9) * mm, "end": v(18.46, -4.07) * mm});
            skLineSegment(sketch, "E526", {"start": v(19.25, 5.44) * mm, "end": v(20.07, 6.17) * mm});
            skArc(sketch, "E527", {"start": v(17.6, 6.91) * mm, "mid": v(17.46, 7.23) * mm, "end": v(17.33, 7.55) * mm});
            skLineSegment(sketch, "E528", {"start": v(18.77, -3.84) * mm, "end": v(19.62, -3.9) * mm});
            skArc(sketch, "E529", {"start": v(17.44, 7.93) * mm, "mid": v(17.31, 7.76) * mm, "end": v(17.33, 7.55) * mm});
            skLineSegment(sketch, "E530", {"start": v(19.62, -3.9) * mm, "end": v(20.69, -3.61) * mm});
            skLineSegment(sketch, "E531", {"start": v(17.44, 7.93) * mm, "end": v(18.16, 8.38) * mm});
            skArc(sketch, "E532", {"start": v(17.94, -6.73) * mm, "mid": v(17.73, -6.76) * mm, "end": v(17.6, -6.91) * mm});
            skLineSegment(sketch, "E533", {"start": v(18.16, 8.38) * mm, "end": v(18.86, 9.24) * mm});
            skArc(sketch, "E534", {"start": v(16.3, 9.58) * mm, "mid": v(16.11, 9.88) * mm, "end": v(15.93, 10.17) * mm});
            skLineSegment(sketch, "E535", {"start": v(17.94, -6.73) * mm, "end": v(18.77, -6.91) * mm});
            skArc(sketch, "E536", {"start": v(15.98, 10.56) * mm, "mid": v(15.89, 10.37) * mm, "end": v(15.93, 10.17) * mm});
            skLineSegment(sketch, "E537", {"start": v(18.77, -6.91) * mm, "end": v(19.87, -6.8) * mm});
            skLineSegment(sketch, "E538", {"start": v(15.98, 10.56) * mm, "end": v(16.62, 11.12) * mm});
            skArc(sketch, "E539", {"start": v(16.66, -9.45) * mm, "mid": v(16.45, -9.45) * mm, "end": v(16.3, -9.58) * mm});
            skLineSegment(sketch, "E540", {"start": v(16.62, 11.12) * mm, "end": v(17.18, 12.07) * mm});
            skArc(sketch, "E541", {"start": v(14.6, 12) * mm, "mid": v(14.37, 12.27) * mm, "end": v(14.14, 12.54) * mm});
            skLineSegment(sketch, "E542", {"start": v(16.66, -9.45) * mm, "end": v(17.45, -9.76) * mm});
            skArc(sketch, "E543", {"start": v(14.14, 12.93) * mm, "mid": v(14.07, 12.73) * mm, "end": v(14.14, 12.54) * mm});
            skLineSegment(sketch, "E544", {"start": v(17.45, -9.76) * mm, "end": v(18.56, -9.83) * mm});
            skLineSegment(sketch, "E545", {"start": v(14.14, 12.93) * mm, "end": v(14.68, 13.58) * mm});
            skArc(sketch, "E546", {"start": v(14.98, -11.94) * mm, "mid": v(14.77, -11.9) * mm, "end": v(14.6, -12) * mm});
            skLineSegment(sketch, "E547", {"start": v(14.68, 13.58) * mm, "end": v(15.08, 14.61) * mm});
            skArc(sketch, "E548", {"start": v(12.54, 14.14) * mm, "mid": v(12.27, 14.37) * mm, "end": v(12, 14.6) * mm});
            skLineSegment(sketch, "E549", {"start": v(14.98, -11.94) * mm, "end": v(15.71, -12.37) * mm});
            skArc(sketch, "E550", {"start": v(11.94, 14.98) * mm, "mid": v(11.9, 14.77) * mm, "end": v(12, 14.6) * mm});
            skLineSegment(sketch, "E551", {"start": v(15.71, -12.37) * mm, "end": v(16.8, -12.61) * mm});
            skArc(sketch, "E552", {"start": v(12.93, -14.14) * mm, "mid": v(12.73, -14.07) * mm, "end": v(12.54, -14.14) * mm});
            skLineSegment(sketch, "E553", {"start": v(11.94, 14.98) * mm, "end": v(12.37, 15.71) * mm});
            skLineSegment(sketch, "E554", {"start": v(12.93, -14.14) * mm, "end": v(13.58, -14.68) * mm});
            skLineSegment(sketch, "E555", {"start": v(12.37, 15.71) * mm, "end": v(12.61, 16.8) * mm});
            skArc(sketch, "E556", {"start": v(10.17, 15.93) * mm, "mid": v(9.88, 16.11) * mm, "end": v(9.58, 16.3) * mm});
            skLineSegment(sketch, "E557", {"start": v(13.58, -14.68) * mm, "end": v(14.61, -15.08) * mm});
            skArc(sketch, "E558", {"start": v(9.45, 16.66) * mm, "mid": v(9.45, 16.45) * mm, "end": v(9.58, 16.3) * mm});
            skArc(sketch, "E559", {"start": v(10.56, -15.98) * mm, "mid": v(10.37, -15.89) * mm, "end": v(10.17, -15.93) * mm});
            skLineSegment(sketch, "E560", {"start": v(9.45, 16.66) * mm, "end": v(9.76, 17.45) * mm});
            skLineSegment(sketch, "E561", {"start": v(10.56, -15.98) * mm, "end": v(11.12, -16.62) * mm});
            skLineSegment(sketch, "E562", {"start": v(9.76, 17.45) * mm, "end": v(9.83, 18.56) * mm});
            skArc(sketch, "E563", {"start": v(7.55, 17.33) * mm, "mid": v(7.23, 17.46) * mm, "end": v(6.91, 17.6) * mm});
            skLineSegment(sketch, "E564", {"start": v(11.12, -16.62) * mm, "end": v(12.07, -17.18) * mm});
            skArc(sketch, "E565", {"start": v(6.73, 17.94) * mm, "mid": v(6.76, 17.73) * mm, "end": v(6.91, 17.6) * mm});
            skArc(sketch, "E566", {"start": v(7.93, -17.44) * mm, "mid": v(7.76, -17.31) * mm, "end": v(7.55, -17.33) * mm});
            skLineSegment(sketch, "E567", {"start": v(6.73, 17.94) * mm, "end": v(6.91, 18.77) * mm});
            skLineSegment(sketch, "E568", {"start": v(7.93, -17.44) * mm, "end": v(8.38, -18.16) * mm});
            skLineSegment(sketch, "E569", {"start": v(6.91, 18.77) * mm, "end": v(6.8, 19.87) * mm});
            skArc(sketch, "E570", {"start": v(4.75, 18.3) * mm, "mid": v(4.41, 18.38) * mm, "end": v(4.07, 18.46) * mm});
            skLineSegment(sketch, "E571", {"start": v(8.38, -18.16) * mm, "end": v(9.24, -18.86) * mm});
            skArc(sketch, "E572", {"start": v(3.84, 18.77) * mm, "mid": v(3.9, 18.57) * mm, "end": v(4.07, 18.46) * mm});
            skArc(sketch, "E573", {"start": v(5.1, -18.46) * mm, "mid": v(4.96, -18.31) * mm, "end": v(4.75, -18.3) * mm});
            skLineSegment(sketch, "E574", {"start": v(3.84, 18.77) * mm, "end": v(3.9, 19.62) * mm});
            skLineSegment(sketch, "E575", {"start": v(5.1, -18.46) * mm, "end": v(5.44, -19.25) * mm});
            skLineSegment(sketch, "E576", {"start": v(3.9, 19.62) * mm, "end": v(3.61, 20.69) * mm});
            skArc(sketch, "E577", {"start": v(1.83, 18.81) * mm, "mid": v(1.48, 18.84) * mm, "end": v(1.14, 18.87) * mm});
            skLineSegment(sketch, "E578", {"start": v(5.44, -19.25) * mm, "end": v(6.17, -20.07) * mm});
            skArc(sketch, "E579", {"start": v(0.86, 19.14) * mm, "mid": v(0.95, 18.95) * mm, "end": v(1.14, 18.87) * mm});
            skArc(sketch, "E580", {"start": v(2.15, -19.04) * mm, "mid": v(2.03, -18.86) * mm, "end": v(1.83, -18.81) * mm});
            skLineSegment(sketch, "E581", {"start": v(0.86, 19.14) * mm, "end": v(0.78, 19.98) * mm});
            skArc(sketch, "E582", {"start": v(-1.14, 18.87) * mm, "mid": v(-1.48, 18.84) * mm, "end": v(-1.83, 18.81) * mm});
            skLineSegment(sketch, "E583", {"start": v(2.15, -19.04) * mm, "end": v(2.36, -19.86) * mm});
            skLineSegment(sketch, "E584", {"start": v(0.78, 19.98) * mm, "end": v(0.33, 21) * mm});
            skArc(sketch, "E585", {"start": v(-2.15, 19.04) * mm, "mid": v(-2.03, 18.86) * mm, "end": v(-1.83, 18.81) * mm});
            skLineSegment(sketch, "E586", {"start": v(2.36, -19.86) * mm, "end": v(2.96, -20.8) * mm});
            skArc(sketch, "E587", {"start": v(-0.86, -19.14) * mm, "mid": v(-0.95, -18.95) * mm, "end": v(-1.14, -18.87) * mm});
            skLineSegment(sketch, "E588", {"start": v(-2.15, 19.04) * mm, "end": v(-2.36, 19.86) * mm});
            skLineSegment(sketch, "E589", {"start": v(-0.86, -19.14) * mm, "end": v(-0.78, -19.98) * mm});
            skLineSegment(sketch, "E590", {"start": v(-2.36, 19.86) * mm, "end": v(-2.96, 20.8) * mm});
            skArc(sketch, "E591", {"start": v(-4.07, 18.46) * mm, "mid": v(-4.41, 18.38) * mm, "end": v(-4.75, 18.3) * mm});
            skLineSegment(sketch, "E592", {"start": v(-0.78, -19.98) * mm, "end": v(-0.33, -21) * mm});
            skArc(sketch, "E593", {"start": v(-5.1, 18.46) * mm, "mid": v(-4.96, 18.31) * mm, "end": v(-4.75, 18.3) * mm});
            skArc(sketch, "E594", {"start": v(-3.84, -18.77) * mm, "mid": v(-3.9, -18.57) * mm, "end": v(-4.07, -18.46) * mm});
            skLineSegment(sketch, "E595", {"start": v(-5.1, 18.46) * mm, "end": v(-5.44, 19.25) * mm});
            skLineSegment(sketch, "E596", {"start": v(-3.84, -18.77) * mm, "end": v(-3.9, -19.62) * mm});
            skLineSegment(sketch, "E597", {"start": v(-5.44, 19.25) * mm, "end": v(-6.17, 20.07) * mm});
            skArc(sketch, "E598", {"start": v(-6.91, 17.6) * mm, "mid": v(-7.23, 17.46) * mm, "end": v(-7.55, 17.33) * mm});
            skLineSegment(sketch, "E599", {"start": v(-3.9, -19.62) * mm, "end": v(-3.61, -20.69) * mm});
            skArc(sketch, "E600", {"start": v(-7.93, 17.44) * mm, "mid": v(-7.76, 17.31) * mm, "end": v(-7.55, 17.33) * mm});
            skArc(sketch, "E601", {"start": v(-6.73, -17.94) * mm, "mid": v(-6.76, -17.73) * mm, "end": v(-6.91, -17.6) * mm});
            skLineSegment(sketch, "E602", {"start": v(-7.93, 17.44) * mm, "end": v(-8.38, 18.16) * mm});
            skLineSegment(sketch, "E603", {"start": v(-6.73, -17.94) * mm, "end": v(-6.91, -18.77) * mm});
            skLineSegment(sketch, "E604", {"start": v(-8.38, 18.16) * mm, "end": v(-9.24, 18.86) * mm});
            skArc(sketch, "E605", {"start": v(-9.58, 16.3) * mm, "mid": v(-9.88, 16.11) * mm, "end": v(-10.17, 15.93) * mm});
            skLineSegment(sketch, "E606", {"start": v(-6.91, -18.77) * mm, "end": v(-6.8, -19.87) * mm});
            skArc(sketch, "E607", {"start": v(-10.56, 15.98) * mm, "mid": v(-10.37, 15.89) * mm, "end": v(-10.17, 15.93) * mm});
            skArc(sketch, "E608", {"start": v(-9.45, -16.66) * mm, "mid": v(-9.45, -16.45) * mm, "end": v(-9.58, -16.3) * mm});
            skLineSegment(sketch, "E609", {"start": v(-10.56, 15.98) * mm, "end": v(-11.12, 16.62) * mm});
            skLineSegment(sketch, "E610", {"start": v(-9.45, -16.66) * mm, "end": v(-9.76, -17.45) * mm});
            skLineSegment(sketch, "E611", {"start": v(-11.12, 16.62) * mm, "end": v(-12.07, 17.18) * mm});
            skArc(sketch, "E612", {"start": v(-12, 14.6) * mm, "mid": v(-12.27, 14.37) * mm, "end": v(-12.54, 14.14) * mm});
            skLineSegment(sketch, "E613", {"start": v(-9.76, -17.45) * mm, "end": v(-9.83, -18.56) * mm});
            skArc(sketch, "E614", {"start": v(-12.93, 14.14) * mm, "mid": v(-12.73, 14.07) * mm, "end": v(-12.54, 14.14) * mm});
            skArc(sketch, "E615", {"start": v(-11.94, -14.98) * mm, "mid": v(-11.9, -14.77) * mm, "end": v(-12, -14.6) * mm});
            skLineSegment(sketch, "E616", {"start": v(-12.93, 14.14) * mm, "end": v(-13.58, 14.68) * mm});
            skLineSegment(sketch, "E617", {"start": v(-11.94, -14.98) * mm, "end": v(-12.37, -15.71) * mm});
            skLineSegment(sketch, "E618", {"start": v(-13.58, 14.68) * mm, "end": v(-14.61, 15.08) * mm});
            skArc(sketch, "E619", {"start": v(-14.14, 12.54) * mm, "mid": v(-14.37, 12.27) * mm, "end": v(-14.6, 12) * mm});
            skLineSegment(sketch, "E620", {"start": v(-12.37, -15.71) * mm, "end": v(-12.61, -16.8) * mm});
            skArc(sketch, "E621", {"start": v(-14.98, 11.94) * mm, "mid": v(-14.77, 11.9) * mm, "end": v(-14.6, 12) * mm});
            skArc(sketch, "E622", {"start": v(-14.14, -12.93) * mm, "mid": v(-14.07, -12.73) * mm, "end": v(-14.14, -12.54) * mm});
            skLineSegment(sketch, "E623", {"start": v(-14.98, 11.94) * mm, "end": v(-15.71, 12.37) * mm});
            skLineSegment(sketch, "E624", {"start": v(-14.14, -12.93) * mm, "end": v(-14.68, -13.58) * mm});
            skLineSegment(sketch, "E625", {"start": v(-15.71, 12.37) * mm, "end": v(-16.8, 12.61) * mm});
            skArc(sketch, "E626", {"start": v(-15.93, 10.17) * mm, "mid": v(-16.11, 9.88) * mm, "end": v(-16.3, 9.58) * mm});
            skLineSegment(sketch, "E627", {"start": v(-14.68, -13.58) * mm, "end": v(-15.08, -14.61) * mm});
            skArc(sketch, "E628", {"start": v(-16.66, 9.45) * mm, "mid": v(-16.45, 9.45) * mm, "end": v(-16.3, 9.58) * mm});
            skArc(sketch, "E629", {"start": v(-15.98, -10.56) * mm, "mid": v(-15.89, -10.37) * mm, "end": v(-15.93, -10.17) * mm});
            skLineSegment(sketch, "E630", {"start": v(-16.66, 9.45) * mm, "end": v(-17.45, 9.76) * mm});
            skLineSegment(sketch, "E631", {"start": v(-15.98, -10.56) * mm, "end": v(-16.62, -11.12) * mm});
            skLineSegment(sketch, "E632", {"start": v(-17.45, 9.76) * mm, "end": v(-18.56, 9.83) * mm});
            skArc(sketch, "E633", {"start": v(-17.33, 7.55) * mm, "mid": v(-17.46, 7.23) * mm, "end": v(-17.6, 6.91) * mm});
            skLineSegment(sketch, "E634", {"start": v(-16.62, -11.12) * mm, "end": v(-17.18, -12.07) * mm});
            skArc(sketch, "E635", {"start": v(-17.94, 6.73) * mm, "mid": v(-17.73, 6.76) * mm, "end": v(-17.6, 6.91) * mm});
            skArc(sketch, "E636", {"start": v(-17.44, -7.93) * mm, "mid": v(-17.31, -7.76) * mm, "end": v(-17.33, -7.55) * mm});
            skLineSegment(sketch, "E637", {"start": v(-17.94, 6.73) * mm, "end": v(-18.77, 6.91) * mm});
            skLineSegment(sketch, "E638", {"start": v(-17.44, -7.93) * mm, "end": v(-18.16, -8.38) * mm});
            skLineSegment(sketch, "E639", {"start": v(-18.77, 6.91) * mm, "end": v(-19.87, 6.8) * mm});
            skArc(sketch, "E640", {"start": v(-18.3, 4.75) * mm, "mid": v(-18.38, 4.41) * mm, "end": v(-18.46, 4.07) * mm});
            skLineSegment(sketch, "E641", {"start": v(-18.16, -8.38) * mm, "end": v(-18.86, -9.24) * mm});
            skArc(sketch, "E642", {"start": v(-18.77, 3.84) * mm, "mid": v(-18.57, 3.9) * mm, "end": v(-18.46, 4.07) * mm});
            skArc(sketch, "E643", {"start": v(-18.46, -5.1) * mm, "mid": v(-18.31, -4.96) * mm, "end": v(-18.3, -4.75) * mm});
            skLineSegment(sketch, "E644", {"start": v(-18.77, 3.84) * mm, "end": v(-19.62, 3.9) * mm});
            skLineSegment(sketch, "E645", {"start": v(-18.46, -5.1) * mm, "end": v(-19.25, -5.44) * mm});
            skLineSegment(sketch, "E646", {"start": v(-19.62, 3.9) * mm, "end": v(-20.69, 3.61) * mm});
            skArc(sketch, "E647", {"start": v(-18.81, 1.83) * mm, "mid": v(-18.84, 1.48) * mm, "end": v(-18.87, 1.14) * mm});
            skLineSegment(sketch, "E648", {"start": v(-19.25, -5.44) * mm, "end": v(-20.07, -6.17) * mm});
            skArc(sketch, "E649", {"start": v(-19.14, 0.86) * mm, "mid": v(-18.95, 0.95) * mm, "end": v(-18.87, 1.14) * mm});
            skLineSegment(sketch, "E650", {"start": v(-19.14, 0.86) * mm, "end": v(-19.98, 0.78) * mm});
            skArc(sketch, "E651", {"start": v(-19.04, -2.15) * mm, "mid": v(-18.86, -2.03) * mm, "end": v(-18.81, -1.83) * mm});
            skLineSegment(sketch, "E652", {"start": v(-19.04, -2.15) * mm, "end": v(-19.86, -2.36) * mm});
            skLineSegment(sketch, "E653", {"start": v(-19.98, 0.78) * mm, "end": v(-21, 0.33) * mm});
            skLineSegment(sketch, "E654", {"start": v(-19.86, -2.36) * mm, "end": v(-20.8, -2.96) * mm});
            skLineSegment(sketch, "E655", {"start": v(-21, -0.33) * mm, "end": v(-19.98, -0.78) * mm});
            skLineSegment(sketch, "E656", {"start": v(-19.98, -0.78) * mm, "end": v(-19.14, -0.86) * mm});
            skArc(sketch, "E657", {"start": v(-18.87, -1.14) * mm, "mid": v(-18.95, -0.95) * mm, "end": v(-19.14, -0.86) * mm});
            skArc(sketch, "E658", {"start": v(-18.87, -1.14) * mm, "mid": v(-18.84, -1.48) * mm, "end": v(-18.81, -1.83) * mm});
            skLineSegment(sketch, "E659", {"start": v(-20.69, -3.61) * mm, "end": v(-19.62, -3.9) * mm});
            skLineSegment(sketch, "E660", {"start": v(-19.62, -3.9) * mm, "end": v(-18.77, -3.84) * mm});
            skArc(sketch, "E661", {"start": v(-18.46, -4.07) * mm, "mid": v(-18.57, -3.9) * mm, "end": v(-18.77, -3.84) * mm});
            skArc(sketch, "E662", {"start": v(-18.46, -4.07) * mm, "mid": v(-18.38, -4.41) * mm, "end": v(-18.3, -4.75) * mm});
            skLineSegment(sketch, "E663", {"start": v(-19.87, -6.8) * mm, "end": v(-18.77, -6.91) * mm});
            skLineSegment(sketch, "E664", {"start": v(-18.77, -6.91) * mm, "end": v(-17.94, -6.73) * mm});
            skArc(sketch, "E665", {"start": v(-17.6, -6.91) * mm, "mid": v(-17.73, -6.76) * mm, "end": v(-17.94, -6.73) * mm});
            skArc(sketch, "E666", {"start": v(-17.6, -6.91) * mm, "mid": v(-17.46, -7.23) * mm, "end": v(-17.33, -7.55) * mm});
            skLineSegment(sketch, "E667", {"start": v(-18.56, -9.83) * mm, "end": v(-17.45, -9.76) * mm});
            skLineSegment(sketch, "E668", {"start": v(-17.45, -9.76) * mm, "end": v(-16.66, -9.45) * mm});
            skArc(sketch, "E669", {"start": v(-16.3, -9.58) * mm, "mid": v(-16.45, -9.45) * mm, "end": v(-16.66, -9.45) * mm});
            skArc(sketch, "E670", {"start": v(-16.3, -9.58) * mm, "mid": v(-16.11, -9.88) * mm, "end": v(-15.93, -10.17) * mm});
            skLineSegment(sketch, "E671", {"start": v(-16.8, -12.61) * mm, "end": v(-15.71, -12.37) * mm});
            skLineSegment(sketch, "E672", {"start": v(-15.71, -12.37) * mm, "end": v(-14.98, -11.94) * mm});
            skArc(sketch, "E673", {"start": v(-14.6, -12) * mm, "mid": v(-14.77, -11.9) * mm, "end": v(-14.98, -11.94) * mm});
            skArc(sketch, "E674", {"start": v(-14.6, -12) * mm, "mid": v(-14.37, -12.27) * mm, "end": v(-14.14, -12.54) * mm});
            skLineSegment(sketch, "E675", {"start": v(-14.61, -15.08) * mm, "end": v(-13.58, -14.68) * mm});
            skLineSegment(sketch, "E676", {"start": v(-13.58, -14.68) * mm, "end": v(-12.93, -14.14) * mm});
            skArc(sketch, "E677", {"start": v(-12.54, -14.14) * mm, "mid": v(-12.73, -14.07) * mm, "end": v(-12.93, -14.14) * mm});
            skArc(sketch, "E678", {"start": v(-12.54, -14.14) * mm, "mid": v(-12.27, -14.37) * mm, "end": v(-12, -14.6) * mm});
            skLineSegment(sketch, "E679", {"start": v(-12.07, -17.18) * mm, "end": v(-11.12, -16.62) * mm});
            skLineSegment(sketch, "E680", {"start": v(-11.12, -16.62) * mm, "end": v(-10.56, -15.98) * mm});
            skArc(sketch, "E681", {"start": v(-10.17, -15.93) * mm, "mid": v(-10.37, -15.89) * mm, "end": v(-10.56, -15.98) * mm});
            skArc(sketch, "E682", {"start": v(-10.17, -15.93) * mm, "mid": v(-9.88, -16.11) * mm, "end": v(-9.58, -16.3) * mm});
            skLineSegment(sketch, "E683", {"start": v(-9.24, -18.86) * mm, "end": v(-8.38, -18.16) * mm});
            skLineSegment(sketch, "E684", {"start": v(-8.38, -18.16) * mm, "end": v(-7.93, -17.44) * mm});
            skArc(sketch, "E685", {"start": v(-7.55, -17.33) * mm, "mid": v(-7.76, -17.31) * mm, "end": v(-7.93, -17.44) * mm});
            skArc(sketch, "E686", {"start": v(-7.55, -17.33) * mm, "mid": v(-7.23, -17.46) * mm, "end": v(-6.91, -17.6) * mm});
            skLineSegment(sketch, "E687", {"start": v(-6.17, -20.07) * mm, "end": v(-5.44, -19.25) * mm});
            skLineSegment(sketch, "E688", {"start": v(-5.44, -19.25) * mm, "end": v(-5.1, -18.46) * mm});
            skArc(sketch, "E689", {"start": v(-4.75, -18.3) * mm, "mid": v(-4.96, -18.31) * mm, "end": v(-5.1, -18.46) * mm});
            skArc(sketch, "E690", {"start": v(-4.75, -18.3) * mm, "mid": v(-4.41, -18.38) * mm, "end": v(-4.07, -18.46) * mm});
            skLineSegment(sketch, "E691", {"start": v(-2.96, -20.8) * mm, "end": v(-2.36, -19.86) * mm});
            skLineSegment(sketch, "E692", {"start": v(-2.36, -19.86) * mm, "end": v(-2.15, -19.04) * mm});
            skArc(sketch, "E693", {"start": v(-1.83, -18.81) * mm, "mid": v(-2.03, -18.86) * mm, "end": v(-2.15, -19.04) * mm});
            skArc(sketch, "E694", {"start": v(-1.83, -18.81) * mm, "mid": v(-1.48, -18.84) * mm, "end": v(-1.14, -18.87) * mm});
            skLineSegment(sketch, "E695", {"start": v(0.33, -21) * mm, "end": v(0.78, -19.98) * mm});
            skLineSegment(sketch, "E696", {"start": v(0.78, -19.98) * mm, "end": v(0.86, -19.14) * mm});
            skArc(sketch, "E697", {"start": v(1.14, -18.87) * mm, "mid": v(0.95, -18.95) * mm, "end": v(0.86, -19.14) * mm});
            skArc(sketch, "E698", {"start": v(1.14, -18.87) * mm, "mid": v(1.48, -18.84) * mm, "end": v(1.83, -18.81) * mm});
            skLineSegment(sketch, "E699", {"start": v(3.61, -20.69) * mm, "end": v(3.9, -19.62) * mm});
            skLineSegment(sketch, "E700", {"start": v(3.9, -19.62) * mm, "end": v(3.84, -18.77) * mm});
            skArc(sketch, "E701", {"start": v(4.07, -18.46) * mm, "mid": v(3.9, -18.57) * mm, "end": v(3.84, -18.77) * mm});
            skArc(sketch, "E702", {"start": v(4.07, -18.46) * mm, "mid": v(4.41, -18.38) * mm, "end": v(4.75, -18.3) * mm});
            skLineSegment(sketch, "E703", {"start": v(6.8, -19.87) * mm, "end": v(6.91, -18.77) * mm});
            skLineSegment(sketch, "E704", {"start": v(6.91, -18.77) * mm, "end": v(6.73, -17.94) * mm});
            skArc(sketch, "E705", {"start": v(6.91, -17.6) * mm, "mid": v(6.76, -17.73) * mm, "end": v(6.73, -17.94) * mm});
            skArc(sketch, "E706", {"start": v(6.91, -17.6) * mm, "mid": v(7.23, -17.46) * mm, "end": v(7.55, -17.33) * mm});
            skLineSegment(sketch, "E707", {"start": v(9.83, -18.56) * mm, "end": v(9.76, -17.45) * mm});
            skLineSegment(sketch, "E708", {"start": v(9.76, -17.45) * mm, "end": v(9.45, -16.66) * mm});
            skArc(sketch, "E709", {"start": v(9.58, -16.3) * mm, "mid": v(9.45, -16.45) * mm, "end": v(9.45, -16.66) * mm});
            skArc(sketch, "E710", {"start": v(9.58, -16.3) * mm, "mid": v(9.88, -16.11) * mm, "end": v(10.17, -15.93) * mm});
            skLineSegment(sketch, "E711", {"start": v(12.61, -16.8) * mm, "end": v(12.37, -15.71) * mm});
            skLineSegment(sketch, "E712", {"start": v(12.37, -15.71) * mm, "end": v(11.94, -14.98) * mm});
            skArc(sketch, "E713", {"start": v(12, -14.6) * mm, "mid": v(11.9, -14.77) * mm, "end": v(11.94, -14.98) * mm});
            skArc(sketch, "E714", {"start": v(12, -14.6) * mm, "mid": v(12.27, -14.37) * mm, "end": v(12.54, -14.14) * mm});
            skLineSegment(sketch, "E715", {"start": v(15.08, -14.61) * mm, "end": v(14.68, -13.58) * mm});
            skLineSegment(sketch, "E716", {"start": v(14.68, -13.58) * mm, "end": v(14.14, -12.93) * mm});
            skArc(sketch, "E717", {"start": v(14.14, -12.54) * mm, "mid": v(14.07, -12.73) * mm, "end": v(14.14, -12.93) * mm});
            skArc(sketch, "E718", {"start": v(14.14, -12.54) * mm, "mid": v(14.37, -12.27) * mm, "end": v(14.6, -12) * mm});
            skLineSegment(sketch, "E719", {"start": v(17.18, -12.07) * mm, "end": v(16.62, -11.12) * mm});
            skLineSegment(sketch, "E720", {"start": v(16.62, -11.12) * mm, "end": v(15.98, -10.56) * mm});
            skArc(sketch, "E721", {"start": v(15.93, -10.17) * mm, "mid": v(15.89, -10.37) * mm, "end": v(15.98, -10.56) * mm});
            skArc(sketch, "E722", {"start": v(15.93, -10.17) * mm, "mid": v(16.11, -9.88) * mm, "end": v(16.3, -9.58) * mm});
            skLineSegment(sketch, "E723", {"start": v(18.86, -9.24) * mm, "end": v(18.16, -8.38) * mm});
            skLineSegment(sketch, "E724", {"start": v(18.16, -8.38) * mm, "end": v(17.44, -7.93) * mm});
            skArc(sketch, "E725", {"start": v(17.33, -7.55) * mm, "mid": v(17.31, -7.76) * mm, "end": v(17.44, -7.93) * mm});
            skArc(sketch, "E726", {"start": v(17.33, -7.55) * mm, "mid": v(17.46, -7.23) * mm, "end": v(17.6, -6.91) * mm});
            skLineSegment(sketch, "E727", {"start": v(20.07, -6.17) * mm, "end": v(19.25, -5.44) * mm});
            skLineSegment(sketch, "E728", {"start": v(19.25, -5.44) * mm, "end": v(18.46, -5.1) * mm});
            skArc(sketch, "E729", {"start": v(18.3, -4.75) * mm, "mid": v(18.31, -4.96) * mm, "end": v(18.46, -5.1) * mm});
            skArc(sketch, "E730", {"start": v(18.3, -4.75) * mm, "mid": v(18.38, -4.41) * mm, "end": v(18.46, -4.07) * mm});
            skLineSegment(sketch, "E731", {"start": v(20.8, -2.96) * mm, "end": v(19.86, -2.36) * mm});
            skLineSegment(sketch, "E732", {"start": v(19.86, -2.36) * mm, "end": v(19.04, -2.15) * mm});
            skArc(sketch, "E733", {"start": v(18.81, -1.83) * mm, "mid": v(18.86, -2.03) * mm, "end": v(19.04, -2.15) * mm});
            skArc(sketch, "E734", {"start": v(18.81, -1.83) * mm, "mid": v(18.84, -1.48) * mm, "end": v(18.87, -1.14) * mm});
            skLineSegment(sketch, "E735", {"start": v(21, 0.33) * mm, "end": v(19.98, 0.78) * mm});
            skLineSegment(sketch, "E736", {"start": v(19.98, 0.78) * mm, "end": v(19.14, 0.86) * mm});
            skArc(sketch, "E737", {"start": v(18.87, 1.14) * mm, "mid": v(18.95, 0.95) * mm, "end": v(19.14, 0.86) * mm});
            skLineSegment(sketch, "E738", {"start": v(20.69, 3.61) * mm, "end": v(19.62, 3.9) * mm});
            skLineSegment(sketch, "E739", {"start": v(19.62, 3.9) * mm, "end": v(18.77, 3.84) * mm});
            skArc(sketch, "E740", {"start": v(18.46, 4.07) * mm, "mid": v(18.57, 3.9) * mm, "end": v(18.77, 3.84) * mm});
            skLineSegment(sketch, "E741", {"start": v(19.87, 6.8) * mm, "end": v(18.77, 6.91) * mm});
            skLineSegment(sketch, "E742", {"start": v(18.77, 6.91) * mm, "end": v(17.94, 6.73) * mm});
            skArc(sketch, "E743", {"start": v(17.6, 6.91) * mm, "mid": v(17.73, 6.76) * mm, "end": v(17.94, 6.73) * mm});
            skLineSegment(sketch, "E744", {"start": v(18.56, 9.83) * mm, "end": v(17.45, 9.76) * mm});
            skLineSegment(sketch, "E745", {"start": v(17.45, 9.76) * mm, "end": v(16.66, 9.45) * mm});
            skArc(sketch, "E746", {"start": v(16.3, 9.58) * mm, "mid": v(16.45, 9.45) * mm, "end": v(16.66, 9.45) * mm});
            skLineSegment(sketch, "E747", {"start": v(16.8, 12.61) * mm, "end": v(15.71, 12.37) * mm});
            skLineSegment(sketch, "E748", {"start": v(15.71, 12.37) * mm, "end": v(14.98, 11.94) * mm});
            skArc(sketch, "E749", {"start": v(14.6, 12) * mm, "mid": v(14.77, 11.9) * mm, "end": v(14.98, 11.94) * mm});
            skLineSegment(sketch, "E750", {"start": v(14.61, 15.08) * mm, "end": v(13.58, 14.68) * mm});
            skLineSegment(sketch, "E751", {"start": v(13.58, 14.68) * mm, "end": v(12.93, 14.14) * mm});
            skArc(sketch, "E752", {"start": v(12.54, 14.14) * mm, "mid": v(12.73, 14.07) * mm, "end": v(12.93, 14.14) * mm});
            skLineSegment(sketch, "E753", {"start": v(12.07, 17.18) * mm, "end": v(11.12, 16.62) * mm});
            skLineSegment(sketch, "E754", {"start": v(11.12, 16.62) * mm, "end": v(10.56, 15.98) * mm});
            skArc(sketch, "E755", {"start": v(10.17, 15.93) * mm, "mid": v(10.37, 15.89) * mm, "end": v(10.56, 15.98) * mm});
            skLineSegment(sketch, "E756", {"start": v(9.24, 18.86) * mm, "end": v(8.38, 18.16) * mm});
            skLineSegment(sketch, "E757", {"start": v(8.38, 18.16) * mm, "end": v(7.93, 17.44) * mm});
            skArc(sketch, "E758", {"start": v(7.55, 17.33) * mm, "mid": v(7.76, 17.31) * mm, "end": v(7.93, 17.44) * mm});
            skLineSegment(sketch, "E759", {"start": v(6.17, 20.07) * mm, "end": v(5.44, 19.25) * mm});
            skLineSegment(sketch, "E760", {"start": v(5.44, 19.25) * mm, "end": v(5.1, 18.46) * mm});
            skArc(sketch, "E761", {"start": v(4.75, 18.3) * mm, "mid": v(4.96, 18.31) * mm, "end": v(5.1, 18.46) * mm});
            skLineSegment(sketch, "E762", {"start": v(2.96, 20.8) * mm, "end": v(2.36, 19.86) * mm});
            skLineSegment(sketch, "E763", {"start": v(2.36, 19.86) * mm, "end": v(2.15, 19.04) * mm});
            skArc(sketch, "E764", {"start": v(1.83, 18.81) * mm, "mid": v(2.03, 18.86) * mm, "end": v(2.15, 19.04) * mm});
            skLineSegment(sketch, "E765", {"start": v(-0.33, 21) * mm, "end": v(-0.78, 19.98) * mm});
            skLineSegment(sketch, "E766", {"start": v(-0.78, 19.98) * mm, "end": v(-0.86, 19.14) * mm});
            skArc(sketch, "E767", {"start": v(-1.14, 18.87) * mm, "mid": v(-0.95, 18.95) * mm, "end": v(-0.86, 19.14) * mm});
            skLineSegment(sketch, "E768", {"start": v(-3.61, 20.69) * mm, "end": v(-3.9, 19.62) * mm});
            skLineSegment(sketch, "E769", {"start": v(-3.9, 19.62) * mm, "end": v(-3.84, 18.77) * mm});
            skArc(sketch, "E770", {"start": v(-4.07, 18.46) * mm, "mid": v(-3.9, 18.57) * mm, "end": v(-3.84, 18.77) * mm});
            skLineSegment(sketch, "E771", {"start": v(-6.8, 19.87) * mm, "end": v(-6.91, 18.77) * mm});
            skLineSegment(sketch, "E772", {"start": v(-6.91, 18.77) * mm, "end": v(-6.73, 17.94) * mm});
            skArc(sketch, "E773", {"start": v(-6.91, 17.6) * mm, "mid": v(-6.76, 17.73) * mm, "end": v(-6.73, 17.94) * mm});
            skLineSegment(sketch, "E774", {"start": v(-9.83, 18.56) * mm, "end": v(-9.76, 17.45) * mm});
            skLineSegment(sketch, "E775", {"start": v(-9.76, 17.45) * mm, "end": v(-9.45, 16.66) * mm});
            skArc(sketch, "E776", {"start": v(-9.58, 16.3) * mm, "mid": v(-9.45, 16.45) * mm, "end": v(-9.45, 16.66) * mm});
            skLineSegment(sketch, "E777", {"start": v(-12.61, 16.8) * mm, "end": v(-12.37, 15.71) * mm});
            skLineSegment(sketch, "E778", {"start": v(-12.37, 15.71) * mm, "end": v(-11.94, 14.98) * mm});
            skArc(sketch, "E779", {"start": v(-12, 14.6) * mm, "mid": v(-11.9, 14.77) * mm, "end": v(-11.94, 14.98) * mm});
            skLineSegment(sketch, "E780", {"start": v(-15.08, 14.61) * mm, "end": v(-14.68, 13.58) * mm});
            skLineSegment(sketch, "E781", {"start": v(-14.68, 13.58) * mm, "end": v(-14.14, 12.93) * mm});
            skArc(sketch, "E782", {"start": v(-14.14, 12.54) * mm, "mid": v(-14.07, 12.73) * mm, "end": v(-14.14, 12.93) * mm});
            skLineSegment(sketch, "E783", {"start": v(-17.18, 12.07) * mm, "end": v(-16.62, 11.12) * mm});
            skLineSegment(sketch, "E784", {"start": v(-16.62, 11.12) * mm, "end": v(-15.98, 10.56) * mm});
            skArc(sketch, "E785", {"start": v(-15.93, 10.17) * mm, "mid": v(-15.89, 10.37) * mm, "end": v(-15.98, 10.56) * mm});
            skLineSegment(sketch, "E786", {"start": v(-18.86, 9.24) * mm, "end": v(-18.16, 8.38) * mm});
            skLineSegment(sketch, "E787", {"start": v(-18.16, 8.38) * mm, "end": v(-17.44, 7.93) * mm});
            skArc(sketch, "E788", {"start": v(-17.33, 7.55) * mm, "mid": v(-17.31, 7.76) * mm, "end": v(-17.44, 7.93) * mm});
            skLineSegment(sketch, "E789", {"start": v(-20.07, 6.17) * mm, "end": v(-19.25, 5.44) * mm});
            skLineSegment(sketch, "E790", {"start": v(-19.25, 5.44) * mm, "end": v(-18.46, 5.1) * mm});
            skArc(sketch, "E791", {"start": v(-18.3, 4.75) * mm, "mid": v(-18.31, 4.96) * mm, "end": v(-18.46, 5.1) * mm});
            skLineSegment(sketch, "E792", {"start": v(-20.8, 2.96) * mm, "end": v(-19.86, 2.36) * mm});
            skLineSegment(sketch, "E793", {"start": v(-19.86, 2.36) * mm, "end": v(-19.04, 2.15) * mm});
            skArc(sketch, "E794", {"start": v(-18.81, 1.83) * mm, "mid": v(-18.86, 2.03) * mm, "end": v(-19.04, 2.15) * mm});
            skArc(sketch, "E795", {"start": v(21, 0) * mm, "mid": v(21, 0.17) * mm, "end": v(21, 0.33) * mm});
            skArc(sketch, "E796", {"start": v(20.8, 2.96) * mm, "mid": v(20.74, 3.29) * mm, "end": v(20.69, 3.61) * mm});
            skArc(sketch, "E797", {"start": v(20.07, 6.17) * mm, "mid": v(19.97, 6.49) * mm, "end": v(19.87, 6.8) * mm});
            skArc(sketch, "E798", {"start": v(18.86, 9.24) * mm, "mid": v(18.71, 9.53) * mm, "end": v(18.56, 9.83) * mm});
            skArc(sketch, "E799", {"start": v(17.18, 12.07) * mm, "mid": v(16.99, 12.34) * mm, "end": v(16.8, 12.61) * mm});
            skArc(sketch, "E800", {"start": v(15.08, 14.61) * mm, "mid": v(14.85, 14.85) * mm, "end": v(14.61, 15.08) * mm});
            skArc(sketch, "E801", {"start": v(12.61, 16.8) * mm, "mid": v(12.34, 16.99) * mm, "end": v(12.07, 17.18) * mm});
            skArc(sketch, "E802", {"start": v(9.83, 18.56) * mm, "mid": v(9.53, 18.71) * mm, "end": v(9.24, 18.86) * mm});
            skArc(sketch, "E803", {"start": v(6.8, 19.87) * mm, "mid": v(6.49, 19.97) * mm, "end": v(6.17, 20.07) * mm});
            skArc(sketch, "E804", {"start": v(3.61, 20.69) * mm, "mid": v(3.29, 20.74) * mm, "end": v(2.96, 20.8) * mm});
            skArc(sketch, "E805", {"start": v(0.33, 21) * mm, "mid": v(0, 21) * mm, "end": v(-0.33, 21) * mm});
            skArc(sketch, "E806", {"start": v(-2.96, 20.8) * mm, "mid": v(-3.29, 20.74) * mm, "end": v(-3.61, 20.69) * mm});
            skArc(sketch, "E807", {"start": v(-6.17, 20.07) * mm, "mid": v(-6.49, 19.97) * mm, "end": v(-6.8, 19.87) * mm});
            skArc(sketch, "E808", {"start": v(-9.24, 18.86) * mm, "mid": v(-9.53, 18.71) * mm, "end": v(-9.83, 18.56) * mm});
            skArc(sketch, "E809", {"start": v(-12.07, 17.18) * mm, "mid": v(-12.34, 16.99) * mm, "end": v(-12.61, 16.8) * mm});
            skArc(sketch, "E810", {"start": v(-14.61, 15.08) * mm, "mid": v(-14.85, 14.85) * mm, "end": v(-15.08, 14.61) * mm});
            skArc(sketch, "E811", {"start": v(-16.8, 12.61) * mm, "mid": v(-16.99, 12.34) * mm, "end": v(-17.18, 12.07) * mm});
            skArc(sketch, "E812", {"start": v(-18.56, 9.83) * mm, "mid": v(-18.71, 9.53) * mm, "end": v(-18.86, 9.24) * mm});
            skArc(sketch, "E813", {"start": v(-19.87, 6.8) * mm, "mid": v(-19.97, 6.49) * mm, "end": v(-20.07, 6.17) * mm});
            skArc(sketch, "E814", {"start": v(-20.69, 3.61) * mm, "mid": v(-20.74, 3.29) * mm, "end": v(-20.8, 2.96) * mm});
            skArc(sketch, "E815", {"start": v(-21, 0.33) * mm, "mid": v(-21, 0.17) * mm, "end": v(-21, 0) * mm});
            skArc(sketch, "E816", {"start": v(-20.8, -2.96) * mm, "mid": v(-20.74, -3.29) * mm, "end": v(-20.69, -3.61) * mm});
            skArc(sketch, "E817", {"start": v(-20.07, -6.17) * mm, "mid": v(-19.97, -6.49) * mm, "end": v(-19.87, -6.8) * mm});
            skArc(sketch, "E818", {"start": v(-18.86, -9.24) * mm, "mid": v(-18.71, -9.53) * mm, "end": v(-18.56, -9.83) * mm});
            skArc(sketch, "E819", {"start": v(-17.18, -12.07) * mm, "mid": v(-16.99, -12.34) * mm, "end": v(-16.8, -12.61) * mm});
            skArc(sketch, "E820", {"start": v(-15.08, -14.61) * mm, "mid": v(-14.85, -14.85) * mm, "end": v(-14.61, -15.08) * mm});
            skArc(sketch, "E821", {"start": v(-12.61, -16.8) * mm, "mid": v(-12.34, -16.99) * mm, "end": v(-12.07, -17.18) * mm});
            skArc(sketch, "E822", {"start": v(-9.83, -18.56) * mm, "mid": v(-9.53, -18.71) * mm, "end": v(-9.24, -18.86) * mm});
            skArc(sketch, "E823", {"start": v(-6.8, -19.87) * mm, "mid": v(-6.49, -19.97) * mm, "end": v(-6.17, -20.07) * mm});
            skArc(sketch, "E824", {"start": v(-3.61, -20.69) * mm, "mid": v(-3.29, -20.74) * mm, "end": v(-2.96, -20.8) * mm});
            skArc(sketch, "E825", {"start": v(-0.33, -21) * mm, "mid": v(0, -21) * mm, "end": v(0.33, -21) * mm});
            skArc(sketch, "E826", {"start": v(2.96, -20.8) * mm, "mid": v(3.29, -20.74) * mm, "end": v(3.61, -20.69) * mm});
            skArc(sketch, "E827", {"start": v(6.17, -20.07) * mm, "mid": v(6.49, -19.97) * mm, "end": v(6.8, -19.87) * mm});
            skArc(sketch, "E828", {"start": v(9.24, -18.86) * mm, "mid": v(9.53, -18.71) * mm, "end": v(9.83, -18.56) * mm});
            skArc(sketch, "E829", {"start": v(12.07, -17.18) * mm, "mid": v(12.34, -16.99) * mm, "end": v(12.61, -16.8) * mm});
            skArc(sketch, "E830", {"start": v(14.61, -15.08) * mm, "mid": v(14.85, -14.85) * mm, "end": v(15.08, -14.61) * mm});
            skArc(sketch, "E831", {"start": v(16.8, -12.61) * mm, "mid": v(16.99, -12.34) * mm, "end": v(17.18, -12.07) * mm});
            skArc(sketch, "E832", {"start": v(18.56, -9.83) * mm, "mid": v(18.71, -9.53) * mm, "end": v(18.86, -9.24) * mm});
            skArc(sketch, "E833", {"start": v(19.87, -6.8) * mm, "mid": v(19.97, -6.49) * mm, "end": v(20.07, -6.17) * mm});
            skArc(sketch, "E834", {"start": v(20.69, -3.61) * mm, "mid": v(20.74, -3.29) * mm, "end": v(20.8, -2.96) * mm});
            skArc(sketch, "E835", {"start": v(0, 5) * mm, "mid": v(-5, 0) * mm, "end": v(0, -5) * mm});
            skCircle(sketch, "E836", {"center": v(0, 0) * mm, "radius": 9 * mm});
            skCircle(sketch, "E837.cCircle", {"center": v(0, 0) * mm, "radius": 9 * mm, "construction": true});
            skLineSegment(sketch, "E837.0", {"start": v(6.93, -5.75) * mm, "end": v(-1.51, -8.87) * mm});
            skLineSegment(sketch, "E837.1", {"start": v(-1.51, -8.87) * mm, "end": v(-8.44, -3.12) * mm});
            skLineSegment(sketch, "E837.2", {"start": v(-8.44, -3.12) * mm, "end": v(-6.93, 5.75) * mm});
            skLineSegment(sketch, "E837.3", {"start": v(-6.93, 5.75) * mm, "end": v(1.51, 8.87) * mm});
            skLineSegment(sketch, "E837.4", {"start": v(1.51, 8.87) * mm, "end": v(8.44, 3.12) * mm});
            skLineSegment(sketch, "E837.5", {"start": v(8.44, 3.12) * mm, "end": v(6.93, -5.75) * mm});
            skSolve(sketch);
        }
        {
            var Q0;
            Q0=makeQuery(id+"F4.imprint","IMPRINT",FACE,{"disambiguationData":[TD([[makeQuery(id+"F4.imprint","IMPRINT",EDGE,{"derivedFrom":sQuery(id+"F4.wireOp",EDGE,"E512")}),1.0]])]});
            var Q1;
            {var subQ0=sQuery(id+"F4.wireOp",EDGE,"E837.2");Q1=makeQuery(id+"F4.imprint","IMPRINT",FACE,{"disambiguationData":[TD([[makeQuery(id+"F4.imprint","IMPRINT",EDGE,{"derivedFrom":subQ0}),1.0]])]});}
            var Q2;
            {var subQ0=sQuery(id+"F4.wireOp",EDGE,"E837.3");Q2=makeQuery(id+"F4.imprint","IMPRINT",FACE,{"disambiguationData":[TD([[makeQuery(id+"F4.imprint","IMPRINT",EDGE,{"derivedFrom":subQ0}),1.0]])]});}
            var Q3;
            {var subQ0=sQuery(id+"F4.wireOp",EDGE,"E837.4");Q3=makeQuery(id+"F4.imprint","IMPRINT",FACE,{"disambiguationData":[TD([[makeQuery(id+"F4.imprint","IMPRINT",EDGE,{"derivedFrom":subQ0}),1.0]])]});}
            var Q4;
            {var subQ0=sQuery(id+"F4.wireOp",EDGE,"E837.5");Q4=makeQuery(id+"F4.imprint","IMPRINT",FACE,{"disambiguationData":[TD([[makeQuery(id+"F4.imprint","IMPRINT",EDGE,{"derivedFrom":subQ0}),1.0]])]});}
            var Q5;
            {var subQ0=sQuery(id+"F4.wireOp",EDGE,"E837.1");Q5=makeQuery(id+"F4.imprint","IMPRINT",FACE,{"disambiguationData":[TD([[makeQuery(id+"F4.imprint","IMPRINT",EDGE,{"derivedFrom":subQ0}),1.0]])]});}
            var Q6;
            {var subQ0=sQuery(id+"F4.wireOp",EDGE,"E837.0");Q6=makeQuery(id+"F4.imprint","IMPRINT",FACE,{"disambiguationData":[TD([[makeQuery(id+"F4.imprint","IMPRINT",EDGE,{"derivedFrom":subQ0}),1.0]])]});}
            extrude(context, id + "F5", {"entities" : qUnion([Q0, Q1, Q2, Q3, Q4, Q5, Q6]), "depth" : 8 * mm});
        }
        {
            var Q0;
            Q0=makeQuery(id+"F1.opExtrude","CAP_FACE",FACE,{"disambiguationData":[OSD([sQuery(id+"F0.wireOp",EDGE,"E0"),sQuery(id+"F0.wireOp",EDGE,"E1"),sQuery(id+"F0.wireOp",EDGE,"E2"),sQuery(id+"F0.wireOp",EDGE,"E3"),sQuery(id+"F0.wireOp",EDGE,"E4"),sQuery(id+"F0.wireOp",EDGE,"E5"),sQuery(id+"F0.wireOp",EDGE,"E6"),sQuery(id+"F0.wireOp",EDGE,"E7"),sQuery(id+"F0.wireOp",EDGE,"E8"),sQuery(id+"F0.wireOp",EDGE,"E9"),sQuery(id+"F0.wireOp",EDGE,"E10"),sQuery(id+"F0.wireOp",EDGE,"E11"),sQuery(id+"F0.wireOp",EDGE,"E12"),sQuery(id+"F0.wireOp",EDGE,"E13"),sQuery(id+"F0.wireOp",EDGE,"E14"),sQuery(id+"F0.wireOp",EDGE,"E15"),sQuery(id+"F0.wireOp",EDGE,"E16"),sQuery(id+"F0.wireOp",EDGE,"E17"),sQuery(id+"F0.wireOp",EDGE,"E18"),sQuery(id+"F0.wireOp",EDGE,"E19"),sQuery(id+"F0.wireOp",EDGE,"E20"),sQuery(id+"F0.wireOp",EDGE,"E21"),sQuery(id+"F0.wireOp",EDGE,"E22"),sQuery(id+"F0.wireOp",EDGE,"E23"),sQuery(id+"F0.wireOp",EDGE,"E24"),sQuery(id+"F0.wireOp",EDGE,"E25"),sQuery(id+"F0.wireOp",EDGE,"E26"),sQuery(id+"F0.wireOp",EDGE,"E27"),sQuery(id+"F0.wireOp",EDGE,"E28"),sQuery(id+"F0.wireOp",EDGE,"E29"),sQuery(id+"F0.wireOp",EDGE,"E30"),sQuery(id+"F0.wireOp",EDGE,"E31"),sQuery(id+"F0.wireOp",EDGE,"E32"),sQuery(id+"F0.wireOp",EDGE,"E33"),sQuery(id+"F0.wireOp",EDGE,"E34"),sQuery(id+"F0.wireOp",EDGE,"E35"),sQuery(id+"F0.wireOp",EDGE,"E36"),sQuery(id+"F0.wireOp",EDGE,"E37"),sQuery(id+"F0.wireOp",EDGE,"E38"),sQuery(id+"F0.wireOp",EDGE,"E39"),sQuery(id+"F0.wireOp",EDGE,"E40"),sQuery(id+"F0.wireOp",EDGE,"E41"),sQuery(id+"F0.wireOp",EDGE,"E42"),sQuery(id+"F0.wireOp",EDGE,"E43"),sQuery(id+"F0.wireOp",EDGE,"E44"),sQuery(id+"F0.wireOp",EDGE,"E45"),sQuery(id+"F0.wireOp",EDGE,"E46"),sQuery(id+"F0.wireOp",EDGE,"E47"),sQuery(id+"F0.wireOp",EDGE,"E48"),sQuery(id+"F0.wireOp",EDGE,"E49"),sQuery(id+"F0.wireOp",EDGE,"E50"),sQuery(id+"F0.wireOp",EDGE,"E51"),sQuery(id+"F0.wireOp",EDGE,"E52"),sQuery(id+"F0.wireOp",EDGE,"E53"),sQuery(id+"F0.wireOp",EDGE,"E54"),sQuery(id+"F0.wireOp",EDGE,"E55"),sQuery(id+"F0.wireOp",EDGE,"E56"),sQuery(id+"F0.wireOp",EDGE,"E57"),sQuery(id+"F0.wireOp",EDGE,"E58"),sQuery(id+"F0.wireOp",EDGE,"E59"),sQuery(id+"F0.wireOp",EDGE,"E60"),sQuery(id+"F0.wireOp",EDGE,"E61"),sQuery(id+"F0.wireOp",EDGE,"E62"),sQuery(id+"F0.wireOp",EDGE,"E63"),sQuery(id+"F0.wireOp",EDGE,"E64"),sQuery(id+"F0.wireOp",EDGE,"E65"),sQuery(id+"F0.wireOp",EDGE,"E66"),sQuery(id+"F0.wireOp",EDGE,"E67"),sQuery(id+"F0.wireOp",EDGE,"E68"),sQuery(id+"F0.wireOp",EDGE,"E69"),sQuery(id+"F0.wireOp",EDGE,"E70"),sQuery(id+"F0.wireOp",EDGE,"E71"),sQuery(id+"F0.wireOp",EDGE,"E72"),sQuery(id+"F0.wireOp",EDGE,"E73"),sQuery(id+"F0.wireOp",EDGE,"E74"),sQuery(id+"F0.wireOp",EDGE,"E75"),sQuery(id+"F0.wireOp",EDGE,"E76"),sQuery(id+"F0.wireOp",EDGE,"E77"),sQuery(id+"F0.wireOp",EDGE,"E78"),sQuery(id+"F0.wireOp",EDGE,"E79"),sQuery(id+"F0.wireOp",EDGE,"E80"),sQuery(id+"F0.wireOp",EDGE,"E81"),sQuery(id+"F0.wireOp",EDGE,"E82"),sQuery(id+"F0.wireOp",EDGE,"E83"),sQuery(id+"F0.wireOp",EDGE,"E84"),sQuery(id+"F0.wireOp",EDGE,"E85"),sQuery(id+"F0.wireOp",EDGE,"E86"),sQuery(id+"F0.wireOp",EDGE,"E87"),sQuery(id+"F0.wireOp",EDGE,"E88"),sQuery(id+"F0.wireOp",EDGE,"E89"),sQuery(id+"F0.wireOp",EDGE,"E90"),sQuery(id+"F0.wireOp",EDGE,"E91"),sQuery(id+"F0.wireOp",EDGE,"E92"),sQuery(id+"F0.wireOp",EDGE,"E93"),sQuery(id+"F0.wireOp",EDGE,"E94"),sQuery(id+"F0.wireOp",EDGE,"E95"),sQuery(id+"F0.wireOp",EDGE,"E96"),sQuery(id+"F0.wireOp",EDGE,"E97"),sQuery(id+"F0.wireOp",EDGE,"E98"),sQuery(id+"F0.wireOp",EDGE,"E99"),sQuery(id+"F0.wireOp",EDGE,"E100"),sQuery(id+"F0.wireOp",EDGE,"E101"),sQuery(id+"F0.wireOp",EDGE,"E102"),sQuery(id+"F0.wireOp",EDGE,"E103"),sQuery(id+"F0.wireOp",EDGE,"E104"),sQuery(id+"F0.wireOp",EDGE,"E105"),sQuery(id+"F0.wireOp",EDGE,"E106"),sQuery(id+"F0.wireOp",EDGE,"E107"),sQuery(id+"F0.wireOp",EDGE,"E108"),sQuery(id+"F0.wireOp",EDGE,"E109"),sQuery(id+"F0.wireOp",EDGE,"E110"),sQuery(id+"F0.wireOp",EDGE,"E111"),sQuery(id+"F0.wireOp",EDGE,"E112"),sQuery(id+"F0.wireOp",EDGE,"E113"),sQuery(id+"F0.wireOp",EDGE,"E114"),sQuery(id+"F0.wireOp",EDGE,"E115"),sQuery(id+"F0.wireOp",EDGE,"E116"),sQuery(id+"F0.wireOp",EDGE,"E117"),sQuery(id+"F0.wireOp",EDGE,"E118"),sQuery(id+"F0.wireOp",EDGE,"E119"),sQuery(id+"F0.wireOp",EDGE,"E120"),sQuery(id+"F0.wireOp",EDGE,"E121"),sQuery(id+"F0.wireOp",EDGE,"E122"),sQuery(id+"F0.wireOp",EDGE,"E123"),sQuery(id+"F0.wireOp",EDGE,"E124"),sQuery(id+"F0.wireOp",EDGE,"E125"),sQuery(id+"F0.wireOp",EDGE,"E126"),sQuery(id+"F0.wireOp",EDGE,"E127"),sQuery(id+"F0.wireOp",EDGE,"E128"),sQuery(id+"F0.wireOp",EDGE,"E129"),sQuery(id+"F0.wireOp",EDGE,"E130"),sQuery(id+"F0.wireOp",EDGE,"E131"),sQuery(id+"F0.wireOp",EDGE,"E132"),sQuery(id+"F0.wireOp",EDGE,"E133"),sQuery(id+"F0.wireOp",EDGE,"E134"),sQuery(id+"F0.wireOp",EDGE,"E135"),sQuery(id+"F0.wireOp",EDGE,"E136"),sQuery(id+"F0.wireOp",EDGE,"E137"),sQuery(id+"F0.wireOp",EDGE,"E138"),sQuery(id+"F0.wireOp",EDGE,"E139"),sQuery(id+"F0.wireOp",EDGE,"E140"),sQuery(id+"F0.wireOp",EDGE,"E141"),sQuery(id+"F0.wireOp",EDGE,"E142"),sQuery(id+"F0.wireOp",EDGE,"E143"),sQuery(id+"F0.wireOp",EDGE,"E144"),sQuery(id+"F0.wireOp",EDGE,"E145"),sQuery(id+"F0.wireOp",EDGE,"E146"),sQuery(id+"F0.wireOp",EDGE,"E147"),sQuery(id+"F0.wireOp",EDGE,"E148"),sQuery(id+"F0.wireOp",EDGE,"E149"),sQuery(id+"F0.wireOp",EDGE,"E150"),sQuery(id+"F0.wireOp",EDGE,"E151"),sQuery(id+"F0.wireOp",EDGE,"E152"),sQuery(id+"F0.wireOp",EDGE,"E153"),sQuery(id+"F0.wireOp",EDGE,"E154"),sQuery(id+"F0.wireOp",EDGE,"E155"),sQuery(id+"F0.wireOp",EDGE,"E156"),sQuery(id+"F0.wireOp",EDGE,"E157"),sQuery(id+"F0.wireOp",EDGE,"E158"),sQuery(id+"F0.wireOp",EDGE,"E159"),sQuery(id+"F0.wireOp",EDGE,"E160"),sQuery(id+"F0.wireOp",EDGE,"E161"),sQuery(id+"F0.wireOp",EDGE,"E162"),sQuery(id+"F0.wireOp",EDGE,"E163"),sQuery(id+"F0.wireOp",EDGE,"E164"),sQuery(id+"F0.wireOp",EDGE,"E165"),sQuery(id+"F0.wireOp",EDGE,"E166"),sQuery(id+"F0.wireOp",EDGE,"E167"),sQuery(id+"F0.wireOp",EDGE,"E168"),sQuery(id+"F0.wireOp",EDGE,"E169"),sQuery(id+"F0.wireOp",EDGE,"E170"),sQuery(id+"F0.wireOp",EDGE,"E171"),sQuery(id+"F0.wireOp",EDGE,"E172"),sQuery(id+"F0.wireOp",EDGE,"E173"),sQuery(id+"F0.wireOp",EDGE,"E174"),sQuery(id+"F0.wireOp",EDGE,"E175"),sQuery(id+"F0.wireOp",EDGE,"E176"),sQuery(id+"F0.wireOp",EDGE,"E177"),sQuery(id+"F0.wireOp",EDGE,"E178"),sQuery(id+"F0.wireOp",EDGE,"E179"),sQuery(id+"F0.wireOp",EDGE,"E180"),sQuery(id+"F0.wireOp",EDGE,"E181"),sQuery(id+"F0.wireOp",EDGE,"E182"),sQuery(id+"F0.wireOp",EDGE,"E183"),sQuery(id+"F0.wireOp",EDGE,"E184"),sQuery(id+"F0.wireOp",EDGE,"E185"),sQuery(id+"F0.wireOp",EDGE,"E186"),sQuery(id+"F0.wireOp",EDGE,"E187"),sQuery(id+"F0.wireOp",EDGE,"E188"),sQuery(id+"F0.wireOp",EDGE,"E189"),sQuery(id+"F0.wireOp",EDGE,"E190"),sQuery(id+"F0.wireOp",EDGE,"E191"),sQuery(id+"F0.wireOp",EDGE,"E192"),sQuery(id+"F0.wireOp",EDGE,"E193"),sQuery(id+"F0.wireOp",EDGE,"E194"),sQuery(id+"F0.wireOp",EDGE,"E195"),sQuery(id+"F0.wireOp",EDGE,"E196"),sQuery(id+"F0.wireOp",EDGE,"E197"),sQuery(id+"F0.wireOp",EDGE,"E198"),sQuery(id+"F0.wireOp",EDGE,"E199"),sQuery(id+"F0.wireOp",EDGE,"E200"),sQuery(id+"F0.wireOp",EDGE,"E201"),sQuery(id+"F0.wireOp",EDGE,"E202"),sQuery(id+"F0.wireOp",EDGE,"E203"),sQuery(id+"F0.wireOp",EDGE,"E204"),sQuery(id+"F0.wireOp",EDGE,"E205"),sQuery(id+"F0.wireOp",EDGE,"E206"),sQuery(id+"F0.wireOp",EDGE,"E207"),sQuery(id+"F0.wireOp",EDGE,"E208"),sQuery(id+"F0.wireOp",EDGE,"E209"),sQuery(id+"F0.wireOp",EDGE,"E210"),sQuery(id+"F0.wireOp",EDGE,"E211"),sQuery(id+"F0.wireOp",EDGE,"E212"),sQuery(id+"F0.wireOp",EDGE,"E213"),sQuery(id+"F0.wireOp",EDGE,"E214"),sQuery(id+"F0.wireOp",EDGE,"E215"),sQuery(id+"F0.wireOp",EDGE,"E216"),sQuery(id+"F0.wireOp",EDGE,"E217"),sQuery(id+"F0.wireOp",EDGE,"E218"),sQuery(id+"F0.wireOp",EDGE,"E219"),sQuery(id+"F0.wireOp",EDGE,"E220"),sQuery(id+"F0.wireOp",EDGE,"E221"),sQuery(id+"F0.wireOp",EDGE,"E222"),sQuery(id+"F0.wireOp",EDGE,"E223"),sQuery(id+"F0.wireOp",EDGE,"E224"),sQuery(id+"F0.wireOp",EDGE,"E225"),sQuery(id+"F0.wireOp",EDGE,"E226"),sQuery(id+"F0.wireOp",EDGE,"E227"),sQuery(id+"F0.wireOp",EDGE,"E228"),sQuery(id+"F0.wireOp",EDGE,"E229"),sQuery(id+"F0.wireOp",EDGE,"E230"),sQuery(id+"F0.wireOp",EDGE,"E231"),sQuery(id+"F0.wireOp",EDGE,"E232"),sQuery(id+"F0.wireOp",EDGE,"E233"),sQuery(id+"F0.wireOp",EDGE,"E234"),sQuery(id+"F0.wireOp",EDGE,"E235"),sQuery(id+"F0.wireOp",EDGE,"E236"),sQuery(id+"F0.wireOp",EDGE,"E237"),sQuery(id+"F0.wireOp",EDGE,"E238"),sQuery(id+"F0.wireOp",EDGE,"E239"),sQuery(id+"F0.wireOp",EDGE,"E240"),sQuery(id+"F0.wireOp",EDGE,"E241"),sQuery(id+"F0.wireOp",EDGE,"E242"),sQuery(id+"F0.wireOp",EDGE,"E243"),sQuery(id+"F0.wireOp",EDGE,"E244"),sQuery(id+"F0.wireOp",EDGE,"E245"),sQuery(id+"F0.wireOp",EDGE,"E246"),sQuery(id+"F0.wireOp",EDGE,"E247"),sQuery(id+"F0.wireOp",EDGE,"E248"),sQuery(id+"F0.wireOp",EDGE,"E249"),sQuery(id+"F0.wireOp",EDGE,"E250"),sQuery(id+"F0.wireOp",EDGE,"E251"),sQuery(id+"F0.wireOp",EDGE,"E252"),sQuery(id+"F0.wireOp",EDGE,"E253"),sQuery(id+"F0.wireOp",EDGE,"E254"),sQuery(id+"F0.wireOp",EDGE,"E255"),sQuery(id+"F0.wireOp",EDGE,"E256"),sQuery(id+"F0.wireOp",EDGE,"E257"),sQuery(id+"F0.wireOp",EDGE,"E258"),sQuery(id+"F0.wireOp",EDGE,"E259"),sQuery(id+"F0.wireOp",EDGE,"E260"),sQuery(id+"F0.wireOp",EDGE,"E261"),sQuery(id+"F0.wireOp",EDGE,"E262"),sQuery(id+"F0.wireOp",EDGE,"E263"),sQuery(id+"F0.wireOp",EDGE,"E264"),sQuery(id+"F0.wireOp",EDGE,"E265"),sQuery(id+"F0.wireOp",EDGE,"E266"),sQuery(id+"F0.wireOp",EDGE,"E267"),sQuery(id+"F0.wireOp",EDGE,"E268"),sQuery(id+"F0.wireOp",EDGE,"E269"),sQuery(id+"F0.wireOp",EDGE,"E270"),sQuery(id+"F0.wireOp",EDGE,"E271"),sQuery(id+"F0.wireOp",EDGE,"E272"),sQuery(id+"F0.wireOp",EDGE,"E273"),sQuery(id+"F0.wireOp",EDGE,"E274"),sQuery(id+"F0.wireOp",EDGE,"E275"),sQuery(id+"F0.wireOp",EDGE,"E276"),sQuery(id+"F0.wireOp",EDGE,"E277"),sQuery(id+"F0.wireOp",EDGE,"E278"),sQuery(id+"F0.wireOp",EDGE,"E279"),sQuery(id+"F0.wireOp",EDGE,"E280"),sQuery(id+"F0.wireOp",EDGE,"E281"),sQuery(id+"F0.wireOp",EDGE,"E282"),sQuery(id+"F0.wireOp",EDGE,"E283"),sQuery(id+"F0.wireOp",EDGE,"E284"),sQuery(id+"F0.wireOp",EDGE,"E285"),sQuery(id+"F0.wireOp",EDGE,"E286"),sQuery(id+"F0.wireOp",EDGE,"E287"),sQuery(id+"F0.wireOp",EDGE,"E288"),sQuery(id+"F0.wireOp",EDGE,"E289"),sQuery(id+"F0.wireOp",EDGE,"E290"),sQuery(id+"F0.wireOp",EDGE,"E291"),sQuery(id+"F0.wireOp",EDGE,"E292"),sQuery(id+"F0.wireOp",EDGE,"E293"),sQuery(id+"F0.wireOp",EDGE,"E294"),sQuery(id+"F0.wireOp",EDGE,"E295"),sQuery(id+"F0.wireOp",EDGE,"E296"),sQuery(id+"F0.wireOp",EDGE,"E297"),sQuery(id+"F0.wireOp",EDGE,"E298"),sQuery(id+"F0.wireOp",EDGE,"E299"),sQuery(id+"F0.wireOp",EDGE,"E300"),sQuery(id+"F0.wireOp",EDGE,"E301"),sQuery(id+"F0.wireOp",EDGE,"E302"),sQuery(id+"F0.wireOp",EDGE,"E303"),sQuery(id+"F0.wireOp",EDGE,"E304"),sQuery(id+"F0.wireOp",EDGE,"E305"),sQuery(id+"F0.wireOp",EDGE,"E306"),sQuery(id+"F0.wireOp",EDGE,"E307"),sQuery(id+"F0.wireOp",EDGE,"E308"),sQuery(id+"F0.wireOp",EDGE,"E309"),sQuery(id+"F0.wireOp",EDGE,"E310"),sQuery(id+"F0.wireOp",EDGE,"E311"),sQuery(id+"F0.wireOp",EDGE,"E312"),sQuery(id+"F0.wireOp",EDGE,"E313"),sQuery(id+"F0.wireOp",EDGE,"E314"),sQuery(id+"F0.wireOp",EDGE,"E315"),sQuery(id+"F0.wireOp",EDGE,"E316"),sQuery(id+"F0.wireOp",EDGE,"E317"),sQuery(id+"F0.wireOp",EDGE,"E318"),sQuery(id+"F0.wireOp",EDGE,"E319"),sQuery(id+"F0.wireOp",EDGE,"E320"),sQuery(id+"F0.wireOp",EDGE,"E321"),sQuery(id+"F0.wireOp",EDGE,"E322"),sQuery(id+"F0.wireOp",EDGE,"E323"),sQuery(id+"F0.wireOp",EDGE,"E324"),sQuery(id+"F0.wireOp",EDGE,"E325"),sQuery(id+"F0.wireOp",EDGE,"E326"),sQuery(id+"F0.wireOp",EDGE,"E327"),sQuery(id+"F0.wireOp",EDGE,"E328"),sQuery(id+"F0.wireOp",EDGE,"E329"),sQuery(id+"F0.wireOp",EDGE,"E330"),sQuery(id+"F0.wireOp",EDGE,"E331"),sQuery(id+"F0.wireOp",EDGE,"E332"),sQuery(id+"F0.wireOp",EDGE,"E333"),sQuery(id+"F0.wireOp",EDGE,"E334"),sQuery(id+"F0.wireOp",EDGE,"E335"),sQuery(id+"F0.wireOp",EDGE,"E336"),sQuery(id+"F0.wireOp",EDGE,"E337"),sQuery(id+"F0.wireOp",EDGE,"E338"),sQuery(id+"F0.wireOp",EDGE,"E339"),sQuery(id+"F0.wireOp",EDGE,"E340"),sQuery(id+"F0.wireOp",EDGE,"E341"),sQuery(id+"F0.wireOp",EDGE,"E342"),sQuery(id+"F0.wireOp",EDGE,"E343"),sQuery(id+"F0.wireOp",EDGE,"E344"),sQuery(id+"F0.wireOp",EDGE,"E345"),sQuery(id+"F0.wireOp",EDGE,"E346"),sQuery(id+"F0.wireOp",EDGE,"E347"),sQuery(id+"F0.wireOp",EDGE,"E348"),sQuery(id+"F0.wireOp",EDGE,"E349"),sQuery(id+"F0.wireOp",EDGE,"E350"),sQuery(id+"F0.wireOp",EDGE,"E351"),sQuery(id+"F0.wireOp",EDGE,"E352"),sQuery(id+"F0.wireOp",EDGE,"E353"),sQuery(id+"F0.wireOp",EDGE,"E354"),sQuery(id+"F0.wireOp",EDGE,"E355"),sQuery(id+"F0.wireOp",EDGE,"E356"),sQuery(id+"F0.wireOp",EDGE,"E357"),sQuery(id+"F0.wireOp",EDGE,"E358"),sQuery(id+"F0.wireOp",EDGE,"E359"),sQuery(id+"F0.wireOp",EDGE,"E360"),sQuery(id+"F0.wireOp",EDGE,"E361"),sQuery(id+"F0.wireOp",EDGE,"E362"),sQuery(id+"F0.wireOp",EDGE,"E363"),sQuery(id+"F0.wireOp",EDGE,"E364"),sQuery(id+"F0.wireOp",EDGE,"E365"),sQuery(id+"F0.wireOp",EDGE,"E366"),sQuery(id+"F0.wireOp",EDGE,"E367"),sQuery(id+"F0.wireOp",EDGE,"E368"),sQuery(id+"F0.wireOp",EDGE,"E369"),sQuery(id+"F0.wireOp",EDGE,"E370"),sQuery(id+"F0.wireOp",EDGE,"E371"),sQuery(id+"F0.wireOp",EDGE,"E372"),sQuery(id+"F0.wireOp",EDGE,"E373"),sQuery(id+"F0.wireOp",EDGE,"E374"),sQuery(id+"F0.wireOp",EDGE,"E375"),sQuery(id+"F0.wireOp",EDGE,"E376"),sQuery(id+"F0.wireOp",EDGE,"E377"),sQuery(id+"F0.wireOp",EDGE,"E378"),sQuery(id+"F0.wireOp",EDGE,"E379"),sQuery(id+"F0.wireOp",EDGE,"E380"),sQuery(id+"F0.wireOp",EDGE,"E381"),sQuery(id+"F0.wireOp",EDGE,"E382"),sQuery(id+"F0.wireOp",EDGE,"E383"),sQuery(id+"F0.wireOp",EDGE,"E384"),sQuery(id+"F0.wireOp",EDGE,"E385"),sQuery(id+"F0.wireOp",EDGE,"E386"),sQuery(id+"F0.wireOp",EDGE,"E387"),sQuery(id+"F0.wireOp",EDGE,"E388"),sQuery(id+"F0.wireOp",EDGE,"E389"),sQuery(id+"F0.wireOp",EDGE,"E390"),sQuery(id+"F0.wireOp",EDGE,"E391"),sQuery(id+"F0.wireOp",EDGE,"E392"),sQuery(id+"F0.wireOp",EDGE,"E393"),sQuery(id+"F0.wireOp",EDGE,"E394"),sQuery(id+"F0.wireOp",EDGE,"E395"),sQuery(id+"F0.wireOp",EDGE,"E396"),sQuery(id+"F0.wireOp",EDGE,"E397"),sQuery(id+"F0.wireOp",EDGE,"E398"),sQuery(id+"F0.wireOp",EDGE,"E399"),sQuery(id+"F0.wireOp",EDGE,"E400"),sQuery(id+"F0.wireOp",EDGE,"E401"),sQuery(id+"F0.wireOp",EDGE,"E402"),sQuery(id+"F0.wireOp",EDGE,"E403"),sQuery(id+"F0.wireOp",EDGE,"E404"),sQuery(id+"F0.wireOp",EDGE,"E405"),sQuery(id+"F0.wireOp",EDGE,"E406"),sQuery(id+"F0.wireOp",EDGE,"E407"),sQuery(id+"F0.wireOp",EDGE,"E408"),sQuery(id+"F0.wireOp",EDGE,"E409"),sQuery(id+"F0.wireOp",EDGE,"E410"),sQuery(id+"F0.wireOp",EDGE,"E411"),sQuery(id+"F0.wireOp",EDGE,"E412"),sQuery(id+"F0.wireOp",EDGE,"E413"),sQuery(id+"F0.wireOp",EDGE,"E414"),sQuery(id+"F0.wireOp",EDGE,"E415"),sQuery(id+"F0.wireOp",EDGE,"E416"),sQuery(id+"F0.wireOp",EDGE,"E417"),sQuery(id+"F0.wireOp",EDGE,"E418"),sQuery(id+"F0.wireOp",EDGE,"E419"),sQuery(id+"F0.wireOp",EDGE,"E420"),sQuery(id+"F0.wireOp",EDGE,"E421"),sQuery(id+"F0.wireOp",EDGE,"E422"),sQuery(id+"F0.wireOp",EDGE,"E423"),sQuery(id+"F0.wireOp",EDGE,"E424"),sQuery(id+"F0.wireOp",EDGE,"E425"),sQuery(id+"F0.wireOp",EDGE,"E426"),sQuery(id+"F0.wireOp",EDGE,"E427"),sQuery(id+"F0.wireOp",EDGE,"E428"),sQuery(id+"F0.wireOp",EDGE,"E429"),sQuery(id+"F0.wireOp",EDGE,"E430"),sQuery(id+"F0.wireOp",EDGE,"E431"),sQuery(id+"F0.wireOp",EDGE,"E432"),sQuery(id+"F0.wireOp",EDGE,"E433"),sQuery(id+"F0.wireOp",EDGE,"E434"),sQuery(id+"F0.wireOp",EDGE,"E435"),sQuery(id+"F0.wireOp",EDGE,"E436"),sQuery(id+"F0.wireOp",EDGE,"E437"),sQuery(id+"F0.wireOp",EDGE,"E438"),sQuery(id+"F0.wireOp",EDGE,"E439"),sQuery(id+"F0.wireOp",EDGE,"E440"),sQuery(id+"F0.wireOp",EDGE,"E490"),sQuery(id+"F0.wireOp",EDGE,"E492"),sQuery(id+"F0.wireOp",EDGE,"E494"),sQuery(id+"F0.wireOp",EDGE,"E496"),sQuery(id+"F0.wireOp",EDGE,"E498"),sQuery(id+"F0.wireOp",EDGE,"E499"),sQuery(id+"F0.wireOp",EDGE,"E500"),sQuery(id+"F0.wireOp",EDGE,"E501"),sQuery(id+"F0.wireOp",EDGE,"E502"),sQuery(id+"F0.wireOp",EDGE,"E503"),sQuery(id+"F0.wireOp",EDGE,"E506")])],"isStart":false});
            var sketch = newSketch(context, id + "F6", { "sketchPlane" : qUnion([Q0])});
            skLineSegment(sketch, "E838.0", {"start": v(-6.93, 5.75) * mm, "end": v(1.51, 8.87) * mm});
            skLineSegment(sketch, "E839.0", {"start": v(1.51, 8.87) * mm, "end": v(8.44, 3.12) * mm});
            skLineSegment(sketch, "E840.0", {"start": v(8.44, 3.12) * mm, "end": v(6.93, -5.75) * mm});
            skLineSegment(sketch, "E841.0", {"start": v(6.93, -5.75) * mm, "end": v(-1.51, -8.87) * mm});
            skLineSegment(sketch, "E842.0", {"start": v(-1.51, -8.87) * mm, "end": v(-8.44, -3.12) * mm});
            skLineSegment(sketch, "E843.0", {"start": v(-8.44, -3.12) * mm, "end": v(-6.93, 5.75) * mm});
            skCircle(sketch, "E844", {"center": v(0, 0) * mm, "radius": 9 * mm});
            skSolve(sketch);
        }
        {
            var Q0;
            {var subQ1=sQuery(id+"F6.wireOp",EDGE,"E841.0");Q0=makeQuery(id+"F6.imprint","IMPRINT",FACE,{"disambiguationData":[TD([[makeQuery(id+"F6.imprint","IMPRINT",EDGE,{"derivedFrom":subQ1}),1.0]])]});}
            var Q1;
            Q1=makeQuery(id+"F6.imprint","IMPRINT",FACE,{"disambiguationData":[TD([[makeQuery(id+"F6.imprint","IMPRINT",EDGE,{"derivedFrom":sQuery(id+"F6.wireOp",EDGE,"E838.0")}),-1.0]])]});
            var Q2;
            {var subQ1=sQuery(id+"F6.wireOp",EDGE,"E840.0");Q2=makeQuery(id+"F6.imprint","IMPRINT",FACE,{"disambiguationData":[TD([[makeQuery(id+"F6.imprint","IMPRINT",EDGE,{"derivedFrom":subQ1}),1.0]])]});}
            var Q3;
            {var subQ1=sQuery(id+"F6.wireOp",EDGE,"E842.0");Q3=makeQuery(id+"F6.imprint","IMPRINT",FACE,{"disambiguationData":[TD([[makeQuery(id+"F6.imprint","IMPRINT",EDGE,{"derivedFrom":subQ1}),1.0]])]});}
            var Q4;
            Q4=makeQuery(id+"F6.imprint","IMPRINT",FACE,{"disambiguationData":[TD([[makeQuery(id+"F6.imprint","IMPRINT",EDGE,{"derivedFrom":makeQuery(id+"F1.opExtrude","CAP_EDGE",EDGE,{"disambiguationData":[OSD([sQuery(id+"F0.wireOp",EDGE,"E506")])],"isStart":false})}),1.0]])]});
            var Q5;
            {var subQ1=sQuery(id+"F6.wireOp",EDGE,"E839.0");Q5=makeQuery(id+"F6.imprint","IMPRINT",FACE,{"disambiguationData":[TD([[makeQuery(id+"F6.imprint","IMPRINT",EDGE,{"derivedFrom":subQ1}),1.0]])]});}
            var Q6;
            {var subQ1=sQuery(id+"F6.wireOp",EDGE,"E843.0");Q6=makeQuery(id+"F6.imprint","IMPRINT",FACE,{"disambiguationData":[TD([[makeQuery(id+"F6.imprint","IMPRINT",EDGE,{"derivedFrom":subQ1}),1.0]])]});}
            var Q7;
            {var subQ1=sQuery(id+"F6.wireOp",EDGE,"E838.0");Q7=makeQuery(id+"F6.imprint","IMPRINT",FACE,{"disambiguationData":[TD([[makeQuery(id+"F6.imprint","IMPRINT",EDGE,{"derivedFrom":subQ1}),1.0]])]});}
            var Q8;
            Q8=makeQuery(id+"F5.opExtrude","CAP_FACE",FACE,{"disambiguationData":[OSD([sQuery(id+"F4.wireOp",EDGE,"E512"),sQuery(id+"F4.wireOp",EDGE,"E514"),sQuery(id+"F4.wireOp",EDGE,"E515"),sQuery(id+"F4.wireOp",EDGE,"E516"),sQuery(id+"F4.wireOp",EDGE,"E517"),sQuery(id+"F4.wireOp",EDGE,"E518"),sQuery(id+"F4.wireOp",EDGE,"E519"),sQuery(id+"F4.wireOp",EDGE,"E520"),sQuery(id+"F4.wireOp",EDGE,"E521"),sQuery(id+"F4.wireOp",EDGE,"E522"),sQuery(id+"F4.wireOp",EDGE,"E523"),sQuery(id+"F4.wireOp",EDGE,"E524"),sQuery(id+"F4.wireOp",EDGE,"E525"),sQuery(id+"F4.wireOp",EDGE,"E526"),sQuery(id+"F4.wireOp",EDGE,"E527"),sQuery(id+"F4.wireOp",EDGE,"E528"),sQuery(id+"F4.wireOp",EDGE,"E529"),sQuery(id+"F4.wireOp",EDGE,"E530"),sQuery(id+"F4.wireOp",EDGE,"E531"),sQuery(id+"F4.wireOp",EDGE,"E532"),sQuery(id+"F4.wireOp",EDGE,"E533"),sQuery(id+"F4.wireOp",EDGE,"E534"),sQuery(id+"F4.wireOp",EDGE,"E535"),sQuery(id+"F4.wireOp",EDGE,"E536"),sQuery(id+"F4.wireOp",EDGE,"E537"),sQuery(id+"F4.wireOp",EDGE,"E538"),sQuery(id+"F4.wireOp",EDGE,"E539"),sQuery(id+"F4.wireOp",EDGE,"E540"),sQuery(id+"F4.wireOp",EDGE,"E541"),sQuery(id+"F4.wireOp",EDGE,"E542"),sQuery(id+"F4.wireOp",EDGE,"E543"),sQuery(id+"F4.wireOp",EDGE,"E544"),sQuery(id+"F4.wireOp",EDGE,"E545"),sQuery(id+"F4.wireOp",EDGE,"E546"),sQuery(id+"F4.wireOp",EDGE,"E547"),sQuery(id+"F4.wireOp",EDGE,"E548"),sQuery(id+"F4.wireOp",EDGE,"E549"),sQuery(id+"F4.wireOp",EDGE,"E550"),sQuery(id+"F4.wireOp",EDGE,"E551"),sQuery(id+"F4.wireOp",EDGE,"E552"),sQuery(id+"F4.wireOp",EDGE,"E553"),sQuery(id+"F4.wireOp",EDGE,"E554"),sQuery(id+"F4.wireOp",EDGE,"E555"),sQuery(id+"F4.wireOp",EDGE,"E556"),sQuery(id+"F4.wireOp",EDGE,"E557"),sQuery(id+"F4.wireOp",EDGE,"E558"),sQuery(id+"F4.wireOp",EDGE,"E559"),sQuery(id+"F4.wireOp",EDGE,"E560"),sQuery(id+"F4.wireOp",EDGE,"E561"),sQuery(id+"F4.wireOp",EDGE,"E562"),sQuery(id+"F4.wireOp",EDGE,"E563"),sQuery(id+"F4.wireOp",EDGE,"E564"),sQuery(id+"F4.wireOp",EDGE,"E565"),sQuery(id+"F4.wireOp",EDGE,"E566"),sQuery(id+"F4.wireOp",EDGE,"E567"),sQuery(id+"F4.wireOp",EDGE,"E568"),sQuery(id+"F4.wireOp",EDGE,"E569"),sQuery(id+"F4.wireOp",EDGE,"E570"),sQuery(id+"F4.wireOp",EDGE,"E571"),sQuery(id+"F4.wireOp",EDGE,"E572"),sQuery(id+"F4.wireOp",EDGE,"E573"),sQuery(id+"F4.wireOp",EDGE,"E574"),sQuery(id+"F4.wireOp",EDGE,"E575"),sQuery(id+"F4.wireOp",EDGE,"E576"),sQuery(id+"F4.wireOp",EDGE,"E577"),sQuery(id+"F4.wireOp",EDGE,"E578"),sQuery(id+"F4.wireOp",EDGE,"E579"),sQuery(id+"F4.wireOp",EDGE,"E580"),sQuery(id+"F4.wireOp",EDGE,"E581"),sQuery(id+"F4.wireOp",EDGE,"E582"),sQuery(id+"F4.wireOp",EDGE,"E583"),sQuery(id+"F4.wireOp",EDGE,"E584"),sQuery(id+"F4.wireOp",EDGE,"E585"),sQuery(id+"F4.wireOp",EDGE,"E586"),sQuery(id+"F4.wireOp",EDGE,"E587"),sQuery(id+"F4.wireOp",EDGE,"E588"),sQuery(id+"F4.wireOp",EDGE,"E589"),sQuery(id+"F4.wireOp",EDGE,"E590"),sQuery(id+"F4.wireOp",EDGE,"E591"),sQuery(id+"F4.wireOp",EDGE,"E592"),sQuery(id+"F4.wireOp",EDGE,"E593"),sQuery(id+"F4.wireOp",EDGE,"E594"),sQuery(id+"F4.wireOp",EDGE,"E595"),sQuery(id+"F4.wireOp",EDGE,"E596"),sQuery(id+"F4.wireOp",EDGE,"E597"),sQuery(id+"F4.wireOp",EDGE,"E598"),sQuery(id+"F4.wireOp",EDGE,"E599"),sQuery(id+"F4.wireOp",EDGE,"E600"),sQuery(id+"F4.wireOp",EDGE,"E601"),sQuery(id+"F4.wireOp",EDGE,"E602"),sQuery(id+"F4.wireOp",EDGE,"E603"),sQuery(id+"F4.wireOp",EDGE,"E604"),sQuery(id+"F4.wireOp",EDGE,"E605"),sQuery(id+"F4.wireOp",EDGE,"E606"),sQuery(id+"F4.wireOp",EDGE,"E607"),sQuery(id+"F4.wireOp",EDGE,"E608"),sQuery(id+"F4.wireOp",EDGE,"E609"),sQuery(id+"F4.wireOp",EDGE,"E610"),sQuery(id+"F4.wireOp",EDGE,"E611"),sQuery(id+"F4.wireOp",EDGE,"E612"),sQuery(id+"F4.wireOp",EDGE,"E613"),sQuery(id+"F4.wireOp",EDGE,"E614"),sQuery(id+"F4.wireOp",EDGE,"E615"),sQuery(id+"F4.wireOp",EDGE,"E616"),sQuery(id+"F4.wireOp",EDGE,"E617"),sQuery(id+"F4.wireOp",EDGE,"E618"),sQuery(id+"F4.wireOp",EDGE,"E619"),sQuery(id+"F4.wireOp",EDGE,"E620"),sQuery(id+"F4.wireOp",EDGE,"E621"),sQuery(id+"F4.wireOp",EDGE,"E622"),sQuery(id+"F4.wireOp",EDGE,"E623"),sQuery(id+"F4.wireOp",EDGE,"E624"),sQuery(id+"F4.wireOp",EDGE,"E625"),sQuery(id+"F4.wireOp",EDGE,"E626"),sQuery(id+"F4.wireOp",EDGE,"E627"),sQuery(id+"F4.wireOp",EDGE,"E628"),sQuery(id+"F4.wireOp",EDGE,"E629"),sQuery(id+"F4.wireOp",EDGE,"E630"),sQuery(id+"F4.wireOp",EDGE,"E631"),sQuery(id+"F4.wireOp",EDGE,"E632"),sQuery(id+"F4.wireOp",EDGE,"E633"),sQuery(id+"F4.wireOp",EDGE,"E634"),sQuery(id+"F4.wireOp",EDGE,"E635"),sQuery(id+"F4.wireOp",EDGE,"E636"),sQuery(id+"F4.wireOp",EDGE,"E637"),sQuery(id+"F4.wireOp",EDGE,"E638"),sQuery(id+"F4.wireOp",EDGE,"E639"),sQuery(id+"F4.wireOp",EDGE,"E640"),sQuery(id+"F4.wireOp",EDGE,"E641"),sQuery(id+"F4.wireOp",EDGE,"E642"),sQuery(id+"F4.wireOp",EDGE,"E643"),sQuery(id+"F4.wireOp",EDGE,"E644"),sQuery(id+"F4.wireOp",EDGE,"E645"),sQuery(id+"F4.wireOp",EDGE,"E646"),sQuery(id+"F4.wireOp",EDGE,"E647"),sQuery(id+"F4.wireOp",EDGE,"E648"),sQuery(id+"F4.wireOp",EDGE,"E649"),sQuery(id+"F4.wireOp",EDGE,"E650"),sQuery(id+"F4.wireOp",EDGE,"E651"),sQuery(id+"F4.wireOp",EDGE,"E652"),sQuery(id+"F4.wireOp",EDGE,"E653"),sQuery(id+"F4.wireOp",EDGE,"E654"),sQuery(id+"F4.wireOp",EDGE,"E655"),sQuery(id+"F4.wireOp",EDGE,"E656"),sQuery(id+"F4.wireOp",EDGE,"E657"),sQuery(id+"F4.wireOp",EDGE,"E658"),sQuery(id+"F4.wireOp",EDGE,"E659"),sQuery(id+"F4.wireOp",EDGE,"E660"),sQuery(id+"F4.wireOp",EDGE,"E661"),sQuery(id+"F4.wireOp",EDGE,"E662"),sQuery(id+"F4.wireOp",EDGE,"E663"),sQuery(id+"F4.wireOp",EDGE,"E664"),sQuery(id+"F4.wireOp",EDGE,"E665"),sQuery(id+"F4.wireOp",EDGE,"E666"),sQuery(id+"F4.wireOp",EDGE,"E667"),sQuery(id+"F4.wireOp",EDGE,"E668"),sQuery(id+"F4.wireOp",EDGE,"E669"),sQuery(id+"F4.wireOp",EDGE,"E670"),sQuery(id+"F4.wireOp",EDGE,"E671"),sQuery(id+"F4.wireOp",EDGE,"E672"),sQuery(id+"F4.wireOp",EDGE,"E673"),sQuery(id+"F4.wireOp",EDGE,"E674"),sQuery(id+"F4.wireOp",EDGE,"E675"),sQuery(id+"F4.wireOp",EDGE,"E676"),sQuery(id+"F4.wireOp",EDGE,"E677"),sQuery(id+"F4.wireOp",EDGE,"E678"),sQuery(id+"F4.wireOp",EDGE,"E679"),sQuery(id+"F4.wireOp",EDGE,"E680"),sQuery(id+"F4.wireOp",EDGE,"E681"),sQuery(id+"F4.wireOp",EDGE,"E682"),sQuery(id+"F4.wireOp",EDGE,"E683"),sQuery(id+"F4.wireOp",EDGE,"E684"),sQuery(id+"F4.wireOp",EDGE,"E685"),sQuery(id+"F4.wireOp",EDGE,"E686"),sQuery(id+"F4.wireOp",EDGE,"E687"),sQuery(id+"F4.wireOp",EDGE,"E688"),sQuery(id+"F4.wireOp",EDGE,"E689"),sQuery(id+"F4.wireOp",EDGE,"E690"),sQuery(id+"F4.wireOp",EDGE,"E691"),sQuery(id+"F4.wireOp",EDGE,"E692"),sQuery(id+"F4.wireOp",EDGE,"E693"),sQuery(id+"F4.wireOp",EDGE,"E694"),sQuery(id+"F4.wireOp",EDGE,"E695"),sQuery(id+"F4.wireOp",EDGE,"E696"),sQuery(id+"F4.wireOp",EDGE,"E697"),sQuery(id+"F4.wireOp",EDGE,"E698"),sQuery(id+"F4.wireOp",EDGE,"E699"),sQuery(id+"F4.wireOp",EDGE,"E700"),sQuery(id+"F4.wireOp",EDGE,"E701"),sQuery(id+"F4.wireOp",EDGE,"E702"),sQuery(id+"F4.wireOp",EDGE,"E703"),sQuery(id+"F4.wireOp",EDGE,"E704"),sQuery(id+"F4.wireOp",EDGE,"E705"),sQuery(id+"F4.wireOp",EDGE,"E706"),sQuery(id+"F4.wireOp",EDGE,"E707"),sQuery(id+"F4.wireOp",EDGE,"E708"),sQuery(id+"F4.wireOp",EDGE,"E709"),sQuery(id+"F4.wireOp",EDGE,"E710"),sQuery(id+"F4.wireOp",EDGE,"E711"),sQuery(id+"F4.wireOp",EDGE,"E712"),sQuery(id+"F4.wireOp",EDGE,"E713"),sQuery(id+"F4.wireOp",EDGE,"E714"),sQuery(id+"F4.wireOp",EDGE,"E715"),sQuery(id+"F4.wireOp",EDGE,"E716"),sQuery(id+"F4.wireOp",EDGE,"E717"),sQuery(id+"F4.wireOp",EDGE,"E718"),sQuery(id+"F4.wireOp",EDGE,"E719"),sQuery(id+"F4.wireOp",EDGE,"E720"),sQuery(id+"F4.wireOp",EDGE,"E721"),sQuery(id+"F4.wireOp",EDGE,"E722"),sQuery(id+"F4.wireOp",EDGE,"E723"),sQuery(id+"F4.wireOp",EDGE,"E724"),sQuery(id+"F4.wireOp",EDGE,"E725"),sQuery(id+"F4.wireOp",EDGE,"E726"),sQuery(id+"F4.wireOp",EDGE,"E727"),sQuery(id+"F4.wireOp",EDGE,"E728"),sQuery(id+"F4.wireOp",EDGE,"E729"),sQuery(id+"F4.wireOp",EDGE,"E730"),sQuery(id+"F4.wireOp",EDGE,"E731"),sQuery(id+"F4.wireOp",EDGE,"E732"),sQuery(id+"F4.wireOp",EDGE,"E733"),sQuery(id+"F4.wireOp",EDGE,"E734"),sQuery(id+"F4.wireOp",EDGE,"E735"),sQuery(id+"F4.wireOp",EDGE,"E736"),sQuery(id+"F4.wireOp",EDGE,"E737"),sQuery(id+"F4.wireOp",EDGE,"E738"),sQuery(id+"F4.wireOp",EDGE,"E739"),sQuery(id+"F4.wireOp",EDGE,"E740"),sQuery(id+"F4.wireOp",EDGE,"E741"),sQuery(id+"F4.wireOp",EDGE,"E742"),sQuery(id+"F4.wireOp",EDGE,"E743"),sQuery(id+"F4.wireOp",EDGE,"E744"),sQuery(id+"F4.wireOp",EDGE,"E745"),sQuery(id+"F4.wireOp",EDGE,"E746"),sQuery(id+"F4.wireOp",EDGE,"E747"),sQuery(id+"F4.wireOp",EDGE,"E748"),sQuery(id+"F4.wireOp",EDGE,"E749"),sQuery(id+"F4.wireOp",EDGE,"E750"),sQuery(id+"F4.wireOp",EDGE,"E751"),sQuery(id+"F4.wireOp",EDGE,"E752"),sQuery(id+"F4.wireOp",EDGE,"E753"),sQuery(id+"F4.wireOp",EDGE,"E754"),sQuery(id+"F4.wireOp",EDGE,"E755"),sQuery(id+"F4.wireOp",EDGE,"E756"),sQuery(id+"F4.wireOp",EDGE,"E757"),sQuery(id+"F4.wireOp",EDGE,"E758"),sQuery(id+"F4.wireOp",EDGE,"E759"),sQuery(id+"F4.wireOp",EDGE,"E760"),sQuery(id+"F4.wireOp",EDGE,"E761"),sQuery(id+"F4.wireOp",EDGE,"E762"),sQuery(id+"F4.wireOp",EDGE,"E763"),sQuery(id+"F4.wireOp",EDGE,"E764"),sQuery(id+"F4.wireOp",EDGE,"E765"),sQuery(id+"F4.wireOp",EDGE,"E766"),sQuery(id+"F4.wireOp",EDGE,"E767"),sQuery(id+"F4.wireOp",EDGE,"E768"),sQuery(id+"F4.wireOp",EDGE,"E769"),sQuery(id+"F4.wireOp",EDGE,"E770"),sQuery(id+"F4.wireOp",EDGE,"E771"),sQuery(id+"F4.wireOp",EDGE,"E772"),sQuery(id+"F4.wireOp",EDGE,"E773"),sQuery(id+"F4.wireOp",EDGE,"E774"),sQuery(id+"F4.wireOp",EDGE,"E775"),sQuery(id+"F4.wireOp",EDGE,"E776"),sQuery(id+"F4.wireOp",EDGE,"E777"),sQuery(id+"F4.wireOp",EDGE,"E778"),sQuery(id+"F4.wireOp",EDGE,"E779"),sQuery(id+"F4.wireOp",EDGE,"E780"),sQuery(id+"F4.wireOp",EDGE,"E781"),sQuery(id+"F4.wireOp",EDGE,"E782"),sQuery(id+"F4.wireOp",EDGE,"E783"),sQuery(id+"F4.wireOp",EDGE,"E784"),sQuery(id+"F4.wireOp",EDGE,"E785"),sQuery(id+"F4.wireOp",EDGE,"E786"),sQuery(id+"F4.wireOp",EDGE,"E787"),sQuery(id+"F4.wireOp",EDGE,"E788"),sQuery(id+"F4.wireOp",EDGE,"E789"),sQuery(id+"F4.wireOp",EDGE,"E790"),sQuery(id+"F4.wireOp",EDGE,"E791"),sQuery(id+"F4.wireOp",EDGE,"E792"),sQuery(id+"F4.wireOp",EDGE,"E793"),sQuery(id+"F4.wireOp",EDGE,"E794"),sQuery(id+"F4.wireOp",EDGE,"E795"),sQuery(id+"F4.wireOp",EDGE,"E796"),sQuery(id+"F4.wireOp",EDGE,"E797"),sQuery(id+"F4.wireOp",EDGE,"E798"),sQuery(id+"F4.wireOp",EDGE,"E799"),sQuery(id+"F4.wireOp",EDGE,"E800"),sQuery(id+"F4.wireOp",EDGE,"E801"),sQuery(id+"F4.wireOp",EDGE,"E802"),sQuery(id+"F4.wireOp",EDGE,"E803"),sQuery(id+"F4.wireOp",EDGE,"E804"),sQuery(id+"F4.wireOp",EDGE,"E805"),sQuery(id+"F4.wireOp",EDGE,"E806"),sQuery(id+"F4.wireOp",EDGE,"E807"),sQuery(id+"F4.wireOp",EDGE,"E808"),sQuery(id+"F4.wireOp",EDGE,"E809"),sQuery(id+"F4.wireOp",EDGE,"E810"),sQuery(id+"F4.wireOp",EDGE,"E811"),sQuery(id+"F4.wireOp",EDGE,"E812"),sQuery(id+"F4.wireOp",EDGE,"E813"),sQuery(id+"F4.wireOp",EDGE,"E814"),sQuery(id+"F4.wireOp",EDGE,"E815"),sQuery(id+"F4.wireOp",EDGE,"E816"),sQuery(id+"F4.wireOp",EDGE,"E817"),sQuery(id+"F4.wireOp",EDGE,"E818"),sQuery(id+"F4.wireOp",EDGE,"E819"),sQuery(id+"F4.wireOp",EDGE,"E820"),sQuery(id+"F4.wireOp",EDGE,"E821"),sQuery(id+"F4.wireOp",EDGE,"E822"),sQuery(id+"F4.wireOp",EDGE,"E823"),sQuery(id+"F4.wireOp",EDGE,"E824"),sQuery(id+"F4.wireOp",EDGE,"E825"),sQuery(id+"F4.wireOp",EDGE,"E826"),sQuery(id+"F4.wireOp",EDGE,"E827"),sQuery(id+"F4.wireOp",EDGE,"E828"),sQuery(id+"F4.wireOp",EDGE,"E829"),sQuery(id+"F4.wireOp",EDGE,"E830"),sQuery(id+"F4.wireOp",EDGE,"E831"),sQuery(id+"F4.wireOp",EDGE,"E832"),sQuery(id+"F4.wireOp",EDGE,"E833"),sQuery(id+"F4.wireOp",EDGE,"E834"),sQuery(id+"F4.wireOp",EDGE,"E837.0"),sQuery(id+"F4.wireOp",EDGE,"E837.1"),sQuery(id+"F4.wireOp",EDGE,"E837.2"),sQuery(id+"F4.wireOp",EDGE,"E837.3"),sQuery(id+"F4.wireOp",EDGE,"E837.4"),sQuery(id+"F4.wireOp",EDGE,"E837.5")])],"isStart":true});
            var Q9;
            Q9=makeQuery(id+"F5.opExtrude","SWEPT_BODY",BODY,{"disambiguationData":[OSD([sQuery(id+"F4.wireOp",EDGE,"E512"),sQuery(id+"F4.wireOp",EDGE,"E514"),sQuery(id+"F4.wireOp",EDGE,"E515"),sQuery(id+"F4.wireOp",EDGE,"E516"),sQuery(id+"F4.wireOp",EDGE,"E517"),sQuery(id+"F4.wireOp",EDGE,"E518"),sQuery(id+"F4.wireOp",EDGE,"E519"),sQuery(id+"F4.wireOp",EDGE,"E520"),sQuery(id+"F4.wireOp",EDGE,"E521"),sQuery(id+"F4.wireOp",EDGE,"E522"),sQuery(id+"F4.wireOp",EDGE,"E523"),sQuery(id+"F4.wireOp",EDGE,"E524"),sQuery(id+"F4.wireOp",EDGE,"E525"),sQuery(id+"F4.wireOp",EDGE,"E526"),sQuery(id+"F4.wireOp",EDGE,"E527"),sQuery(id+"F4.wireOp",EDGE,"E528"),sQuery(id+"F4.wireOp",EDGE,"E529"),sQuery(id+"F4.wireOp",EDGE,"E530"),sQuery(id+"F4.wireOp",EDGE,"E531"),sQuery(id+"F4.wireOp",EDGE,"E532"),sQuery(id+"F4.wireOp",EDGE,"E533"),sQuery(id+"F4.wireOp",EDGE,"E534"),sQuery(id+"F4.wireOp",EDGE,"E535"),sQuery(id+"F4.wireOp",EDGE,"E536"),sQuery(id+"F4.wireOp",EDGE,"E537"),sQuery(id+"F4.wireOp",EDGE,"E538"),sQuery(id+"F4.wireOp",EDGE,"E539"),sQuery(id+"F4.wireOp",EDGE,"E540"),sQuery(id+"F4.wireOp",EDGE,"E541"),sQuery(id+"F4.wireOp",EDGE,"E542"),sQuery(id+"F4.wireOp",EDGE,"E543"),sQuery(id+"F4.wireOp",EDGE,"E544"),sQuery(id+"F4.wireOp",EDGE,"E545"),sQuery(id+"F4.wireOp",EDGE,"E546"),sQuery(id+"F4.wireOp",EDGE,"E547"),sQuery(id+"F4.wireOp",EDGE,"E548"),sQuery(id+"F4.wireOp",EDGE,"E549"),sQuery(id+"F4.wireOp",EDGE,"E550"),sQuery(id+"F4.wireOp",EDGE,"E551"),sQuery(id+"F4.wireOp",EDGE,"E552"),sQuery(id+"F4.wireOp",EDGE,"E553"),sQuery(id+"F4.wireOp",EDGE,"E554"),sQuery(id+"F4.wireOp",EDGE,"E555"),sQuery(id+"F4.wireOp",EDGE,"E556"),sQuery(id+"F4.wireOp",EDGE,"E557"),sQuery(id+"F4.wireOp",EDGE,"E558"),sQuery(id+"F4.wireOp",EDGE,"E559"),sQuery(id+"F4.wireOp",EDGE,"E560"),sQuery(id+"F4.wireOp",EDGE,"E561"),sQuery(id+"F4.wireOp",EDGE,"E562"),sQuery(id+"F4.wireOp",EDGE,"E563"),sQuery(id+"F4.wireOp",EDGE,"E564"),sQuery(id+"F4.wireOp",EDGE,"E565"),sQuery(id+"F4.wireOp",EDGE,"E566"),sQuery(id+"F4.wireOp",EDGE,"E567"),sQuery(id+"F4.wireOp",EDGE,"E568"),sQuery(id+"F4.wireOp",EDGE,"E569"),sQuery(id+"F4.wireOp",EDGE,"E570"),sQuery(id+"F4.wireOp",EDGE,"E571"),sQuery(id+"F4.wireOp",EDGE,"E572"),sQuery(id+"F4.wireOp",EDGE,"E573"),sQuery(id+"F4.wireOp",EDGE,"E574"),sQuery(id+"F4.wireOp",EDGE,"E575"),sQuery(id+"F4.wireOp",EDGE,"E576"),sQuery(id+"F4.wireOp",EDGE,"E577"),sQuery(id+"F4.wireOp",EDGE,"E578"),sQuery(id+"F4.wireOp",EDGE,"E579"),sQuery(id+"F4.wireOp",EDGE,"E580"),sQuery(id+"F4.wireOp",EDGE,"E581"),sQuery(id+"F4.wireOp",EDGE,"E582"),sQuery(id+"F4.wireOp",EDGE,"E583"),sQuery(id+"F4.wireOp",EDGE,"E584"),sQuery(id+"F4.wireOp",EDGE,"E585"),sQuery(id+"F4.wireOp",EDGE,"E586"),sQuery(id+"F4.wireOp",EDGE,"E587"),sQuery(id+"F4.wireOp",EDGE,"E588"),sQuery(id+"F4.wireOp",EDGE,"E589"),sQuery(id+"F4.wireOp",EDGE,"E590"),sQuery(id+"F4.wireOp",EDGE,"E591"),sQuery(id+"F4.wireOp",EDGE,"E592"),sQuery(id+"F4.wireOp",EDGE,"E593"),sQuery(id+"F4.wireOp",EDGE,"E594"),sQuery(id+"F4.wireOp",EDGE,"E595"),sQuery(id+"F4.wireOp",EDGE,"E596"),sQuery(id+"F4.wireOp",EDGE,"E597"),sQuery(id+"F4.wireOp",EDGE,"E598"),sQuery(id+"F4.wireOp",EDGE,"E599"),sQuery(id+"F4.wireOp",EDGE,"E600"),sQuery(id+"F4.wireOp",EDGE,"E601"),sQuery(id+"F4.wireOp",EDGE,"E602"),sQuery(id+"F4.wireOp",EDGE,"E603"),sQuery(id+"F4.wireOp",EDGE,"E604"),sQuery(id+"F4.wireOp",EDGE,"E605"),sQuery(id+"F4.wireOp",EDGE,"E606"),sQuery(id+"F4.wireOp",EDGE,"E607"),sQuery(id+"F4.wireOp",EDGE,"E608"),sQuery(id+"F4.wireOp",EDGE,"E609"),sQuery(id+"F4.wireOp",EDGE,"E610"),sQuery(id+"F4.wireOp",EDGE,"E611"),sQuery(id+"F4.wireOp",EDGE,"E612"),sQuery(id+"F4.wireOp",EDGE,"E613"),sQuery(id+"F4.wireOp",EDGE,"E614"),sQuery(id+"F4.wireOp",EDGE,"E615"),sQuery(id+"F4.wireOp",EDGE,"E616"),sQuery(id+"F4.wireOp",EDGE,"E617"),sQuery(id+"F4.wireOp",EDGE,"E618"),sQuery(id+"F4.wireOp",EDGE,"E619"),sQuery(id+"F4.wireOp",EDGE,"E620"),sQuery(id+"F4.wireOp",EDGE,"E621"),sQuery(id+"F4.wireOp",EDGE,"E622"),sQuery(id+"F4.wireOp",EDGE,"E623"),sQuery(id+"F4.wireOp",EDGE,"E624"),sQuery(id+"F4.wireOp",EDGE,"E625"),sQuery(id+"F4.wireOp",EDGE,"E626"),sQuery(id+"F4.wireOp",EDGE,"E627"),sQuery(id+"F4.wireOp",EDGE,"E628"),sQuery(id+"F4.wireOp",EDGE,"E629"),sQuery(id+"F4.wireOp",EDGE,"E630"),sQuery(id+"F4.wireOp",EDGE,"E631"),sQuery(id+"F4.wireOp",EDGE,"E632"),sQuery(id+"F4.wireOp",EDGE,"E633"),sQuery(id+"F4.wireOp",EDGE,"E634"),sQuery(id+"F4.wireOp",EDGE,"E635"),sQuery(id+"F4.wireOp",EDGE,"E636"),sQuery(id+"F4.wireOp",EDGE,"E637"),sQuery(id+"F4.wireOp",EDGE,"E638"),sQuery(id+"F4.wireOp",EDGE,"E639"),sQuery(id+"F4.wireOp",EDGE,"E640"),sQuery(id+"F4.wireOp",EDGE,"E641"),sQuery(id+"F4.wireOp",EDGE,"E642"),sQuery(id+"F4.wireOp",EDGE,"E643"),sQuery(id+"F4.wireOp",EDGE,"E644"),sQuery(id+"F4.wireOp",EDGE,"E645"),sQuery(id+"F4.wireOp",EDGE,"E646"),sQuery(id+"F4.wireOp",EDGE,"E647"),sQuery(id+"F4.wireOp",EDGE,"E648"),sQuery(id+"F4.wireOp",EDGE,"E649"),sQuery(id+"F4.wireOp",EDGE,"E650"),sQuery(id+"F4.wireOp",EDGE,"E651"),sQuery(id+"F4.wireOp",EDGE,"E652"),sQuery(id+"F4.wireOp",EDGE,"E653"),sQuery(id+"F4.wireOp",EDGE,"E654"),sQuery(id+"F4.wireOp",EDGE,"E655"),sQuery(id+"F4.wireOp",EDGE,"E656"),sQuery(id+"F4.wireOp",EDGE,"E657"),sQuery(id+"F4.wireOp",EDGE,"E658"),sQuery(id+"F4.wireOp",EDGE,"E659"),sQuery(id+"F4.wireOp",EDGE,"E660"),sQuery(id+"F4.wireOp",EDGE,"E661"),sQuery(id+"F4.wireOp",EDGE,"E662"),sQuery(id+"F4.wireOp",EDGE,"E663"),sQuery(id+"F4.wireOp",EDGE,"E664"),sQuery(id+"F4.wireOp",EDGE,"E665"),sQuery(id+"F4.wireOp",EDGE,"E666"),sQuery(id+"F4.wireOp",EDGE,"E667"),sQuery(id+"F4.wireOp",EDGE,"E668"),sQuery(id+"F4.wireOp",EDGE,"E669"),sQuery(id+"F4.wireOp",EDGE,"E670"),sQuery(id+"F4.wireOp",EDGE,"E671"),sQuery(id+"F4.wireOp",EDGE,"E672"),sQuery(id+"F4.wireOp",EDGE,"E673"),sQuery(id+"F4.wireOp",EDGE,"E674"),sQuery(id+"F4.wireOp",EDGE,"E675"),sQuery(id+"F4.wireOp",EDGE,"E676"),sQuery(id+"F4.wireOp",EDGE,"E677"),sQuery(id+"F4.wireOp",EDGE,"E678"),sQuery(id+"F4.wireOp",EDGE,"E679"),sQuery(id+"F4.wireOp",EDGE,"E680"),sQuery(id+"F4.wireOp",EDGE,"E681"),sQuery(id+"F4.wireOp",EDGE,"E682"),sQuery(id+"F4.wireOp",EDGE,"E683"),sQuery(id+"F4.wireOp",EDGE,"E684"),sQuery(id+"F4.wireOp",EDGE,"E685"),sQuery(id+"F4.wireOp",EDGE,"E686"),sQuery(id+"F4.wireOp",EDGE,"E687"),sQuery(id+"F4.wireOp",EDGE,"E688"),sQuery(id+"F4.wireOp",EDGE,"E689"),sQuery(id+"F4.wireOp",EDGE,"E690"),sQuery(id+"F4.wireOp",EDGE,"E691"),sQuery(id+"F4.wireOp",EDGE,"E692"),sQuery(id+"F4.wireOp",EDGE,"E693"),sQuery(id+"F4.wireOp",EDGE,"E694"),sQuery(id+"F4.wireOp",EDGE,"E695"),sQuery(id+"F4.wireOp",EDGE,"E696"),sQuery(id+"F4.wireOp",EDGE,"E697"),sQuery(id+"F4.wireOp",EDGE,"E698"),sQuery(id+"F4.wireOp",EDGE,"E699"),sQuery(id+"F4.wireOp",EDGE,"E700"),sQuery(id+"F4.wireOp",EDGE,"E701"),sQuery(id+"F4.wireOp",EDGE,"E702"),sQuery(id+"F4.wireOp",EDGE,"E703"),sQuery(id+"F4.wireOp",EDGE,"E704"),sQuery(id+"F4.wireOp",EDGE,"E705"),sQuery(id+"F4.wireOp",EDGE,"E706"),sQuery(id+"F4.wireOp",EDGE,"E707"),sQuery(id+"F4.wireOp",EDGE,"E708"),sQuery(id+"F4.wireOp",EDGE,"E709"),sQuery(id+"F4.wireOp",EDGE,"E710"),sQuery(id+"F4.wireOp",EDGE,"E711"),sQuery(id+"F4.wireOp",EDGE,"E712"),sQuery(id+"F4.wireOp",EDGE,"E713"),sQuery(id+"F4.wireOp",EDGE,"E714"),sQuery(id+"F4.wireOp",EDGE,"E715"),sQuery(id+"F4.wireOp",EDGE,"E716"),sQuery(id+"F4.wireOp",EDGE,"E717"),sQuery(id+"F4.wireOp",EDGE,"E718"),sQuery(id+"F4.wireOp",EDGE,"E719"),sQuery(id+"F4.wireOp",EDGE,"E720"),sQuery(id+"F4.wireOp",EDGE,"E721"),sQuery(id+"F4.wireOp",EDGE,"E722"),sQuery(id+"F4.wireOp",EDGE,"E723"),sQuery(id+"F4.wireOp",EDGE,"E724"),sQuery(id+"F4.wireOp",EDGE,"E725"),sQuery(id+"F4.wireOp",EDGE,"E726"),sQuery(id+"F4.wireOp",EDGE,"E727"),sQuery(id+"F4.wireOp",EDGE,"E728"),sQuery(id+"F4.wireOp",EDGE,"E729"),sQuery(id+"F4.wireOp",EDGE,"E730"),sQuery(id+"F4.wireOp",EDGE,"E731"),sQuery(id+"F4.wireOp",EDGE,"E732"),sQuery(id+"F4.wireOp",EDGE,"E733"),sQuery(id+"F4.wireOp",EDGE,"E734"),sQuery(id+"F4.wireOp",EDGE,"E735"),sQuery(id+"F4.wireOp",EDGE,"E736"),sQuery(id+"F4.wireOp",EDGE,"E737"),sQuery(id+"F4.wireOp",EDGE,"E738"),sQuery(id+"F4.wireOp",EDGE,"E739"),sQuery(id+"F4.wireOp",EDGE,"E740"),sQuery(id+"F4.wireOp",EDGE,"E741"),sQuery(id+"F4.wireOp",EDGE,"E742"),sQuery(id+"F4.wireOp",EDGE,"E743"),sQuery(id+"F4.wireOp",EDGE,"E744"),sQuery(id+"F4.wireOp",EDGE,"E745"),sQuery(id+"F4.wireOp",EDGE,"E746"),sQuery(id+"F4.wireOp",EDGE,"E747"),sQuery(id+"F4.wireOp",EDGE,"E748"),sQuery(id+"F4.wireOp",EDGE,"E749"),sQuery(id+"F4.wireOp",EDGE,"E750"),sQuery(id+"F4.wireOp",EDGE,"E751"),sQuery(id+"F4.wireOp",EDGE,"E752"),sQuery(id+"F4.wireOp",EDGE,"E753"),sQuery(id+"F4.wireOp",EDGE,"E754"),sQuery(id+"F4.wireOp",EDGE,"E755"),sQuery(id+"F4.wireOp",EDGE,"E756"),sQuery(id+"F4.wireOp",EDGE,"E757"),sQuery(id+"F4.wireOp",EDGE,"E758"),sQuery(id+"F4.wireOp",EDGE,"E759"),sQuery(id+"F4.wireOp",EDGE,"E760"),sQuery(id+"F4.wireOp",EDGE,"E761"),sQuery(id+"F4.wireOp",EDGE,"E762"),sQuery(id+"F4.wireOp",EDGE,"E763"),sQuery(id+"F4.wireOp",EDGE,"E764"),sQuery(id+"F4.wireOp",EDGE,"E765"),sQuery(id+"F4.wireOp",EDGE,"E766"),sQuery(id+"F4.wireOp",EDGE,"E767"),sQuery(id+"F4.wireOp",EDGE,"E768"),sQuery(id+"F4.wireOp",EDGE,"E769"),sQuery(id+"F4.wireOp",EDGE,"E770"),sQuery(id+"F4.wireOp",EDGE,"E771"),sQuery(id+"F4.wireOp",EDGE,"E772"),sQuery(id+"F4.wireOp",EDGE,"E773"),sQuery(id+"F4.wireOp",EDGE,"E774"),sQuery(id+"F4.wireOp",EDGE,"E775"),sQuery(id+"F4.wireOp",EDGE,"E776"),sQuery(id+"F4.wireOp",EDGE,"E777"),sQuery(id+"F4.wireOp",EDGE,"E778"),sQuery(id+"F4.wireOp",EDGE,"E779"),sQuery(id+"F4.wireOp",EDGE,"E780"),sQuery(id+"F4.wireOp",EDGE,"E781"),sQuery(id+"F4.wireOp",EDGE,"E782"),sQuery(id+"F4.wireOp",EDGE,"E783"),sQuery(id+"F4.wireOp",EDGE,"E784"),sQuery(id+"F4.wireOp",EDGE,"E785"),sQuery(id+"F4.wireOp",EDGE,"E786"),sQuery(id+"F4.wireOp",EDGE,"E787"),sQuery(id+"F4.wireOp",EDGE,"E788"),sQuery(id+"F4.wireOp",EDGE,"E789"),sQuery(id+"F4.wireOp",EDGE,"E790"),sQuery(id+"F4.wireOp",EDGE,"E791"),sQuery(id+"F4.wireOp",EDGE,"E792"),sQuery(id+"F4.wireOp",EDGE,"E793"),sQuery(id+"F4.wireOp",EDGE,"E794"),sQuery(id+"F4.wireOp",EDGE,"E795"),sQuery(id+"F4.wireOp",EDGE,"E796"),sQuery(id+"F4.wireOp",EDGE,"E797"),sQuery(id+"F4.wireOp",EDGE,"E798"),sQuery(id+"F4.wireOp",EDGE,"E799"),sQuery(id+"F4.wireOp",EDGE,"E800"),sQuery(id+"F4.wireOp",EDGE,"E801"),sQuery(id+"F4.wireOp",EDGE,"E802"),sQuery(id+"F4.wireOp",EDGE,"E803"),sQuery(id+"F4.wireOp",EDGE,"E804"),sQuery(id+"F4.wireOp",EDGE,"E805"),sQuery(id+"F4.wireOp",EDGE,"E806"),sQuery(id+"F4.wireOp",EDGE,"E807"),sQuery(id+"F4.wireOp",EDGE,"E808"),sQuery(id+"F4.wireOp",EDGE,"E809"),sQuery(id+"F4.wireOp",EDGE,"E810"),sQuery(id+"F4.wireOp",EDGE,"E811"),sQuery(id+"F4.wireOp",EDGE,"E812"),sQuery(id+"F4.wireOp",EDGE,"E813"),sQuery(id+"F4.wireOp",EDGE,"E814"),sQuery(id+"F4.wireOp",EDGE,"E815"),sQuery(id+"F4.wireOp",EDGE,"E816"),sQuery(id+"F4.wireOp",EDGE,"E817"),sQuery(id+"F4.wireOp",EDGE,"E818"),sQuery(id+"F4.wireOp",EDGE,"E819"),sQuery(id+"F4.wireOp",EDGE,"E820"),sQuery(id+"F4.wireOp",EDGE,"E821"),sQuery(id+"F4.wireOp",EDGE,"E822"),sQuery(id+"F4.wireOp",EDGE,"E823"),sQuery(id+"F4.wireOp",EDGE,"E824"),sQuery(id+"F4.wireOp",EDGE,"E825"),sQuery(id+"F4.wireOp",EDGE,"E826"),sQuery(id+"F4.wireOp",EDGE,"E827"),sQuery(id+"F4.wireOp",EDGE,"E828"),sQuery(id+"F4.wireOp",EDGE,"E829"),sQuery(id+"F4.wireOp",EDGE,"E830"),sQuery(id+"F4.wireOp",EDGE,"E831"),sQuery(id+"F4.wireOp",EDGE,"E832"),sQuery(id+"F4.wireOp",EDGE,"E833"),sQuery(id+"F4.wireOp",EDGE,"E834"),sQuery(id+"F4.wireOp",EDGE,"E837.0"),sQuery(id+"F4.wireOp",EDGE,"E837.1"),sQuery(id+"F4.wireOp",EDGE,"E837.2"),sQuery(id+"F4.wireOp",EDGE,"E837.3"),sQuery(id+"F4.wireOp",EDGE,"E837.4"),sQuery(id+"F4.wireOp",EDGE,"E837.5")])]});
            extrude(context, id + "F7", {"entities" : qUnion([Q0, Q1, Q2, Q3, Q4, Q5, Q6, Q7]), "operationType" : NewBodyOperationType.ADD, "endBound" : BoundingType.UP_TO_SURFACE, "endBoundEntityFace" : qUnion([Q8]), "endBoundEntityBody" : qUnion([Q9]), "depth" : 25 * mm});
        }
        {
            var Q0;
            Q0=makeQuery(id+"F7.opExtrude","CAP_FACE",FACE,{"disambiguationData":[OSD([sQuery(id+"F6.wireOp",EDGE,"E844")])],"isStart":false});
            var sketch = newSketch(context, id + "F8", { "sketchPlane" : qUnion([Q0])});
            skLineSegment(sketch, "E845.0", {"start": v(-1.51, -8.87) * mm, "end": v(-8.44, -3.12) * mm});
            skLineSegment(sketch, "E846.0", {"start": v(-8.44, -3.12) * mm, "end": v(-6.93, 5.75) * mm});
            skLineSegment(sketch, "E847.0", {"start": v(-6.93, 5.75) * mm, "end": v(1.51, 8.87) * mm});
            skLineSegment(sketch, "E848.0", {"start": v(1.51, 8.87) * mm, "end": v(8.44, 3.12) * mm});
            skLineSegment(sketch, "E849.0", {"start": v(8.44, 3.12) * mm, "end": v(6.93, -5.75) * mm});
            skLineSegment(sketch, "E850.0", {"start": v(6.93, -5.75) * mm, "end": v(-1.51, -8.87) * mm});
            skSolve(sketch);
        }
        {
            var Q0;
            Q0=makeQuery(id+"F8.imprint","IMPRINT",FACE,{"disambiguationData":[TD([[makeQuery(id+"F8.imprint","IMPRINT",EDGE,{"derivedFrom":sQuery(id+"F8.wireOp",EDGE,"E845.0")}),-1.0]])]});
            var Q1;
            Q1=makeQuery(id+"F5.opExtrude","CAP_FACE",FACE,{"disambiguationData":[OSD([sQuery(id+"F4.wireOp",EDGE,"E512"),sQuery(id+"F4.wireOp",EDGE,"E514"),sQuery(id+"F4.wireOp",EDGE,"E515"),sQuery(id+"F4.wireOp",EDGE,"E516"),sQuery(id+"F4.wireOp",EDGE,"E517"),sQuery(id+"F4.wireOp",EDGE,"E518"),sQuery(id+"F4.wireOp",EDGE,"E519"),sQuery(id+"F4.wireOp",EDGE,"E520"),sQuery(id+"F4.wireOp",EDGE,"E521"),sQuery(id+"F4.wireOp",EDGE,"E522"),sQuery(id+"F4.wireOp",EDGE,"E523"),sQuery(id+"F4.wireOp",EDGE,"E524"),sQuery(id+"F4.wireOp",EDGE,"E525"),sQuery(id+"F4.wireOp",EDGE,"E526"),sQuery(id+"F4.wireOp",EDGE,"E527"),sQuery(id+"F4.wireOp",EDGE,"E528"),sQuery(id+"F4.wireOp",EDGE,"E529"),sQuery(id+"F4.wireOp",EDGE,"E530"),sQuery(id+"F4.wireOp",EDGE,"E531"),sQuery(id+"F4.wireOp",EDGE,"E532"),sQuery(id+"F4.wireOp",EDGE,"E533"),sQuery(id+"F4.wireOp",EDGE,"E534"),sQuery(id+"F4.wireOp",EDGE,"E535"),sQuery(id+"F4.wireOp",EDGE,"E536"),sQuery(id+"F4.wireOp",EDGE,"E537"),sQuery(id+"F4.wireOp",EDGE,"E538"),sQuery(id+"F4.wireOp",EDGE,"E539"),sQuery(id+"F4.wireOp",EDGE,"E540"),sQuery(id+"F4.wireOp",EDGE,"E541"),sQuery(id+"F4.wireOp",EDGE,"E542"),sQuery(id+"F4.wireOp",EDGE,"E543"),sQuery(id+"F4.wireOp",EDGE,"E544"),sQuery(id+"F4.wireOp",EDGE,"E545"),sQuery(id+"F4.wireOp",EDGE,"E546"),sQuery(id+"F4.wireOp",EDGE,"E547"),sQuery(id+"F4.wireOp",EDGE,"E548"),sQuery(id+"F4.wireOp",EDGE,"E549"),sQuery(id+"F4.wireOp",EDGE,"E550"),sQuery(id+"F4.wireOp",EDGE,"E551"),sQuery(id+"F4.wireOp",EDGE,"E552"),sQuery(id+"F4.wireOp",EDGE,"E553"),sQuery(id+"F4.wireOp",EDGE,"E554"),sQuery(id+"F4.wireOp",EDGE,"E555"),sQuery(id+"F4.wireOp",EDGE,"E556"),sQuery(id+"F4.wireOp",EDGE,"E557"),sQuery(id+"F4.wireOp",EDGE,"E558"),sQuery(id+"F4.wireOp",EDGE,"E559"),sQuery(id+"F4.wireOp",EDGE,"E560"),sQuery(id+"F4.wireOp",EDGE,"E561"),sQuery(id+"F4.wireOp",EDGE,"E562"),sQuery(id+"F4.wireOp",EDGE,"E563"),sQuery(id+"F4.wireOp",EDGE,"E564"),sQuery(id+"F4.wireOp",EDGE,"E565"),sQuery(id+"F4.wireOp",EDGE,"E566"),sQuery(id+"F4.wireOp",EDGE,"E567"),sQuery(id+"F4.wireOp",EDGE,"E568"),sQuery(id+"F4.wireOp",EDGE,"E569"),sQuery(id+"F4.wireOp",EDGE,"E570"),sQuery(id+"F4.wireOp",EDGE,"E571"),sQuery(id+"F4.wireOp",EDGE,"E572"),sQuery(id+"F4.wireOp",EDGE,"E573"),sQuery(id+"F4.wireOp",EDGE,"E574"),sQuery(id+"F4.wireOp",EDGE,"E575"),sQuery(id+"F4.wireOp",EDGE,"E576"),sQuery(id+"F4.wireOp",EDGE,"E577"),sQuery(id+"F4.wireOp",EDGE,"E578"),sQuery(id+"F4.wireOp",EDGE,"E579"),sQuery(id+"F4.wireOp",EDGE,"E580"),sQuery(id+"F4.wireOp",EDGE,"E581"),sQuery(id+"F4.wireOp",EDGE,"E582"),sQuery(id+"F4.wireOp",EDGE,"E583"),sQuery(id+"F4.wireOp",EDGE,"E584"),sQuery(id+"F4.wireOp",EDGE,"E585"),sQuery(id+"F4.wireOp",EDGE,"E586"),sQuery(id+"F4.wireOp",EDGE,"E587"),sQuery(id+"F4.wireOp",EDGE,"E588"),sQuery(id+"F4.wireOp",EDGE,"E589"),sQuery(id+"F4.wireOp",EDGE,"E590"),sQuery(id+"F4.wireOp",EDGE,"E591"),sQuery(id+"F4.wireOp",EDGE,"E592"),sQuery(id+"F4.wireOp",EDGE,"E593"),sQuery(id+"F4.wireOp",EDGE,"E594"),sQuery(id+"F4.wireOp",EDGE,"E595"),sQuery(id+"F4.wireOp",EDGE,"E596"),sQuery(id+"F4.wireOp",EDGE,"E597"),sQuery(id+"F4.wireOp",EDGE,"E598"),sQuery(id+"F4.wireOp",EDGE,"E599"),sQuery(id+"F4.wireOp",EDGE,"E600"),sQuery(id+"F4.wireOp",EDGE,"E601"),sQuery(id+"F4.wireOp",EDGE,"E602"),sQuery(id+"F4.wireOp",EDGE,"E603"),sQuery(id+"F4.wireOp",EDGE,"E604"),sQuery(id+"F4.wireOp",EDGE,"E605"),sQuery(id+"F4.wireOp",EDGE,"E606"),sQuery(id+"F4.wireOp",EDGE,"E607"),sQuery(id+"F4.wireOp",EDGE,"E608"),sQuery(id+"F4.wireOp",EDGE,"E609"),sQuery(id+"F4.wireOp",EDGE,"E610"),sQuery(id+"F4.wireOp",EDGE,"E611"),sQuery(id+"F4.wireOp",EDGE,"E612"),sQuery(id+"F4.wireOp",EDGE,"E613"),sQuery(id+"F4.wireOp",EDGE,"E614"),sQuery(id+"F4.wireOp",EDGE,"E615"),sQuery(id+"F4.wireOp",EDGE,"E616"),sQuery(id+"F4.wireOp",EDGE,"E617"),sQuery(id+"F4.wireOp",EDGE,"E618"),sQuery(id+"F4.wireOp",EDGE,"E619"),sQuery(id+"F4.wireOp",EDGE,"E620"),sQuery(id+"F4.wireOp",EDGE,"E621"),sQuery(id+"F4.wireOp",EDGE,"E622"),sQuery(id+"F4.wireOp",EDGE,"E623"),sQuery(id+"F4.wireOp",EDGE,"E624"),sQuery(id+"F4.wireOp",EDGE,"E625"),sQuery(id+"F4.wireOp",EDGE,"E626"),sQuery(id+"F4.wireOp",EDGE,"E627"),sQuery(id+"F4.wireOp",EDGE,"E628"),sQuery(id+"F4.wireOp",EDGE,"E629"),sQuery(id+"F4.wireOp",EDGE,"E630"),sQuery(id+"F4.wireOp",EDGE,"E631"),sQuery(id+"F4.wireOp",EDGE,"E632"),sQuery(id+"F4.wireOp",EDGE,"E633"),sQuery(id+"F4.wireOp",EDGE,"E634"),sQuery(id+"F4.wireOp",EDGE,"E635"),sQuery(id+"F4.wireOp",EDGE,"E636"),sQuery(id+"F4.wireOp",EDGE,"E637"),sQuery(id+"F4.wireOp",EDGE,"E638"),sQuery(id+"F4.wireOp",EDGE,"E639"),sQuery(id+"F4.wireOp",EDGE,"E640"),sQuery(id+"F4.wireOp",EDGE,"E641"),sQuery(id+"F4.wireOp",EDGE,"E642"),sQuery(id+"F4.wireOp",EDGE,"E643"),sQuery(id+"F4.wireOp",EDGE,"E644"),sQuery(id+"F4.wireOp",EDGE,"E645"),sQuery(id+"F4.wireOp",EDGE,"E646"),sQuery(id+"F4.wireOp",EDGE,"E647"),sQuery(id+"F4.wireOp",EDGE,"E648"),sQuery(id+"F4.wireOp",EDGE,"E649"),sQuery(id+"F4.wireOp",EDGE,"E650"),sQuery(id+"F4.wireOp",EDGE,"E651"),sQuery(id+"F4.wireOp",EDGE,"E652"),sQuery(id+"F4.wireOp",EDGE,"E653"),sQuery(id+"F4.wireOp",EDGE,"E654"),sQuery(id+"F4.wireOp",EDGE,"E655"),sQuery(id+"F4.wireOp",EDGE,"E656"),sQuery(id+"F4.wireOp",EDGE,"E657"),sQuery(id+"F4.wireOp",EDGE,"E658"),sQuery(id+"F4.wireOp",EDGE,"E659"),sQuery(id+"F4.wireOp",EDGE,"E660"),sQuery(id+"F4.wireOp",EDGE,"E661"),sQuery(id+"F4.wireOp",EDGE,"E662"),sQuery(id+"F4.wireOp",EDGE,"E663"),sQuery(id+"F4.wireOp",EDGE,"E664"),sQuery(id+"F4.wireOp",EDGE,"E665"),sQuery(id+"F4.wireOp",EDGE,"E666"),sQuery(id+"F4.wireOp",EDGE,"E667"),sQuery(id+"F4.wireOp",EDGE,"E668"),sQuery(id+"F4.wireOp",EDGE,"E669"),sQuery(id+"F4.wireOp",EDGE,"E670"),sQuery(id+"F4.wireOp",EDGE,"E671"),sQuery(id+"F4.wireOp",EDGE,"E672"),sQuery(id+"F4.wireOp",EDGE,"E673"),sQuery(id+"F4.wireOp",EDGE,"E674"),sQuery(id+"F4.wireOp",EDGE,"E675"),sQuery(id+"F4.wireOp",EDGE,"E676"),sQuery(id+"F4.wireOp",EDGE,"E677"),sQuery(id+"F4.wireOp",EDGE,"E678"),sQuery(id+"F4.wireOp",EDGE,"E679"),sQuery(id+"F4.wireOp",EDGE,"E680"),sQuery(id+"F4.wireOp",EDGE,"E681"),sQuery(id+"F4.wireOp",EDGE,"E682"),sQuery(id+"F4.wireOp",EDGE,"E683"),sQuery(id+"F4.wireOp",EDGE,"E684"),sQuery(id+"F4.wireOp",EDGE,"E685"),sQuery(id+"F4.wireOp",EDGE,"E686"),sQuery(id+"F4.wireOp",EDGE,"E687"),sQuery(id+"F4.wireOp",EDGE,"E688"),sQuery(id+"F4.wireOp",EDGE,"E689"),sQuery(id+"F4.wireOp",EDGE,"E690"),sQuery(id+"F4.wireOp",EDGE,"E691"),sQuery(id+"F4.wireOp",EDGE,"E692"),sQuery(id+"F4.wireOp",EDGE,"E693"),sQuery(id+"F4.wireOp",EDGE,"E694"),sQuery(id+"F4.wireOp",EDGE,"E695"),sQuery(id+"F4.wireOp",EDGE,"E696"),sQuery(id+"F4.wireOp",EDGE,"E697"),sQuery(id+"F4.wireOp",EDGE,"E698"),sQuery(id+"F4.wireOp",EDGE,"E699"),sQuery(id+"F4.wireOp",EDGE,"E700"),sQuery(id+"F4.wireOp",EDGE,"E701"),sQuery(id+"F4.wireOp",EDGE,"E702"),sQuery(id+"F4.wireOp",EDGE,"E703"),sQuery(id+"F4.wireOp",EDGE,"E704"),sQuery(id+"F4.wireOp",EDGE,"E705"),sQuery(id+"F4.wireOp",EDGE,"E706"),sQuery(id+"F4.wireOp",EDGE,"E707"),sQuery(id+"F4.wireOp",EDGE,"E708"),sQuery(id+"F4.wireOp",EDGE,"E709"),sQuery(id+"F4.wireOp",EDGE,"E710"),sQuery(id+"F4.wireOp",EDGE,"E711"),sQuery(id+"F4.wireOp",EDGE,"E712"),sQuery(id+"F4.wireOp",EDGE,"E713"),sQuery(id+"F4.wireOp",EDGE,"E714"),sQuery(id+"F4.wireOp",EDGE,"E715"),sQuery(id+"F4.wireOp",EDGE,"E716"),sQuery(id+"F4.wireOp",EDGE,"E717"),sQuery(id+"F4.wireOp",EDGE,"E718"),sQuery(id+"F4.wireOp",EDGE,"E719"),sQuery(id+"F4.wireOp",EDGE,"E720"),sQuery(id+"F4.wireOp",EDGE,"E721"),sQuery(id+"F4.wireOp",EDGE,"E722"),sQuery(id+"F4.wireOp",EDGE,"E723"),sQuery(id+"F4.wireOp",EDGE,"E724"),sQuery(id+"F4.wireOp",EDGE,"E725"),sQuery(id+"F4.wireOp",EDGE,"E726"),sQuery(id+"F4.wireOp",EDGE,"E727"),sQuery(id+"F4.wireOp",EDGE,"E728"),sQuery(id+"F4.wireOp",EDGE,"E729"),sQuery(id+"F4.wireOp",EDGE,"E730"),sQuery(id+"F4.wireOp",EDGE,"E731"),sQuery(id+"F4.wireOp",EDGE,"E732"),sQuery(id+"F4.wireOp",EDGE,"E733"),sQuery(id+"F4.wireOp",EDGE,"E734"),sQuery(id+"F4.wireOp",EDGE,"E735"),sQuery(id+"F4.wireOp",EDGE,"E736"),sQuery(id+"F4.wireOp",EDGE,"E737"),sQuery(id+"F4.wireOp",EDGE,"E738"),sQuery(id+"F4.wireOp",EDGE,"E739"),sQuery(id+"F4.wireOp",EDGE,"E740"),sQuery(id+"F4.wireOp",EDGE,"E741"),sQuery(id+"F4.wireOp",EDGE,"E742"),sQuery(id+"F4.wireOp",EDGE,"E743"),sQuery(id+"F4.wireOp",EDGE,"E744"),sQuery(id+"F4.wireOp",EDGE,"E745"),sQuery(id+"F4.wireOp",EDGE,"E746"),sQuery(id+"F4.wireOp",EDGE,"E747"),sQuery(id+"F4.wireOp",EDGE,"E748"),sQuery(id+"F4.wireOp",EDGE,"E749"),sQuery(id+"F4.wireOp",EDGE,"E750"),sQuery(id+"F4.wireOp",EDGE,"E751"),sQuery(id+"F4.wireOp",EDGE,"E752"),sQuery(id+"F4.wireOp",EDGE,"E753"),sQuery(id+"F4.wireOp",EDGE,"E754"),sQuery(id+"F4.wireOp",EDGE,"E755"),sQuery(id+"F4.wireOp",EDGE,"E756"),sQuery(id+"F4.wireOp",EDGE,"E757"),sQuery(id+"F4.wireOp",EDGE,"E758"),sQuery(id+"F4.wireOp",EDGE,"E759"),sQuery(id+"F4.wireOp",EDGE,"E760"),sQuery(id+"F4.wireOp",EDGE,"E761"),sQuery(id+"F4.wireOp",EDGE,"E762"),sQuery(id+"F4.wireOp",EDGE,"E763"),sQuery(id+"F4.wireOp",EDGE,"E764"),sQuery(id+"F4.wireOp",EDGE,"E765"),sQuery(id+"F4.wireOp",EDGE,"E766"),sQuery(id+"F4.wireOp",EDGE,"E767"),sQuery(id+"F4.wireOp",EDGE,"E768"),sQuery(id+"F4.wireOp",EDGE,"E769"),sQuery(id+"F4.wireOp",EDGE,"E770"),sQuery(id+"F4.wireOp",EDGE,"E771"),sQuery(id+"F4.wireOp",EDGE,"E772"),sQuery(id+"F4.wireOp",EDGE,"E773"),sQuery(id+"F4.wireOp",EDGE,"E774"),sQuery(id+"F4.wireOp",EDGE,"E775"),sQuery(id+"F4.wireOp",EDGE,"E776"),sQuery(id+"F4.wireOp",EDGE,"E777"),sQuery(id+"F4.wireOp",EDGE,"E778"),sQuery(id+"F4.wireOp",EDGE,"E779"),sQuery(id+"F4.wireOp",EDGE,"E780"),sQuery(id+"F4.wireOp",EDGE,"E781"),sQuery(id+"F4.wireOp",EDGE,"E782"),sQuery(id+"F4.wireOp",EDGE,"E783"),sQuery(id+"F4.wireOp",EDGE,"E784"),sQuery(id+"F4.wireOp",EDGE,"E785"),sQuery(id+"F4.wireOp",EDGE,"E786"),sQuery(id+"F4.wireOp",EDGE,"E787"),sQuery(id+"F4.wireOp",EDGE,"E788"),sQuery(id+"F4.wireOp",EDGE,"E789"),sQuery(id+"F4.wireOp",EDGE,"E790"),sQuery(id+"F4.wireOp",EDGE,"E791"),sQuery(id+"F4.wireOp",EDGE,"E792"),sQuery(id+"F4.wireOp",EDGE,"E793"),sQuery(id+"F4.wireOp",EDGE,"E794"),sQuery(id+"F4.wireOp",EDGE,"E795"),sQuery(id+"F4.wireOp",EDGE,"E796"),sQuery(id+"F4.wireOp",EDGE,"E797"),sQuery(id+"F4.wireOp",EDGE,"E798"),sQuery(id+"F4.wireOp",EDGE,"E799"),sQuery(id+"F4.wireOp",EDGE,"E800"),sQuery(id+"F4.wireOp",EDGE,"E801"),sQuery(id+"F4.wireOp",EDGE,"E802"),sQuery(id+"F4.wireOp",EDGE,"E803"),sQuery(id+"F4.wireOp",EDGE,"E804"),sQuery(id+"F4.wireOp",EDGE,"E805"),sQuery(id+"F4.wireOp",EDGE,"E806"),sQuery(id+"F4.wireOp",EDGE,"E807"),sQuery(id+"F4.wireOp",EDGE,"E808"),sQuery(id+"F4.wireOp",EDGE,"E809"),sQuery(id+"F4.wireOp",EDGE,"E810"),sQuery(id+"F4.wireOp",EDGE,"E811"),sQuery(id+"F4.wireOp",EDGE,"E812"),sQuery(id+"F4.wireOp",EDGE,"E813"),sQuery(id+"F4.wireOp",EDGE,"E814"),sQuery(id+"F4.wireOp",EDGE,"E815"),sQuery(id+"F4.wireOp",EDGE,"E816"),sQuery(id+"F4.wireOp",EDGE,"E817"),sQuery(id+"F4.wireOp",EDGE,"E818"),sQuery(id+"F4.wireOp",EDGE,"E819"),sQuery(id+"F4.wireOp",EDGE,"E820"),sQuery(id+"F4.wireOp",EDGE,"E821"),sQuery(id+"F4.wireOp",EDGE,"E822"),sQuery(id+"F4.wireOp",EDGE,"E823"),sQuery(id+"F4.wireOp",EDGE,"E824"),sQuery(id+"F4.wireOp",EDGE,"E825"),sQuery(id+"F4.wireOp",EDGE,"E826"),sQuery(id+"F4.wireOp",EDGE,"E827"),sQuery(id+"F4.wireOp",EDGE,"E828"),sQuery(id+"F4.wireOp",EDGE,"E829"),sQuery(id+"F4.wireOp",EDGE,"E830"),sQuery(id+"F4.wireOp",EDGE,"E831"),sQuery(id+"F4.wireOp",EDGE,"E832"),sQuery(id+"F4.wireOp",EDGE,"E833"),sQuery(id+"F4.wireOp",EDGE,"E834"),sQuery(id+"F4.wireOp",EDGE,"E837.0"),sQuery(id+"F4.wireOp",EDGE,"E837.1"),sQuery(id+"F4.wireOp",EDGE,"E837.2"),sQuery(id+"F4.wireOp",EDGE,"E837.3"),sQuery(id+"F4.wireOp",EDGE,"E837.4"),sQuery(id+"F4.wireOp",EDGE,"E837.5")])],"isStart":false});
            extrude(context, id + "F9", {"entities" : qUnion([Q0]), "operationType" : NewBodyOperationType.ADD, "endBound" : BoundingType.UP_TO_SURFACE, "endBoundEntityFace" : qUnion([Q1]), "depth" : 25 * mm});
        }
        {
            var Q0;
            Q0=makeQuery(id+"F9.opExtrude","CAP_FACE",FACE,{"disambiguationData":[OSD([sQuery(id+"F8.wireOp",EDGE,"E845.0"),sQuery(id+"F8.wireOp",EDGE,"E846.0"),sQuery(id+"F8.wireOp",EDGE,"E847.0"),sQuery(id+"F8.wireOp",EDGE,"E848.0"),sQuery(id+"F8.wireOp",EDGE,"E849.0"),sQuery(id+"F8.wireOp",EDGE,"E850.0")])],"isStart":false});
            var sketch = newSketch(context, id + "F10", { "sketchPlane" : qUnion([Q0])});
            skCircle(sketch, "E851", {"center": v(0, 0) * mm, "radius": 5 * mm});
            skSolve(sketch);
        }
        {
            var Q0;
            Q0=makeQuery(id+"F10.imprint","IMPRINT",FACE,{"disambiguationData":[TD([[makeQuery(id+"F10.imprint","IMPRINT",EDGE,{"derivedFrom":sQuery(id+"F10.wireOp",EDGE,"E851")}),1.0]])]});
            var Q1;
            Q1=makeQuery(id+"F1.opExtrude","SWEPT_BODY",BODY,{"disambiguationData":[OSD([sQuery(id+"F0.wireOp",EDGE,"E0"),sQuery(id+"F0.wireOp",EDGE,"E1"),sQuery(id+"F0.wireOp",EDGE,"E2"),sQuery(id+"F0.wireOp",EDGE,"E3"),sQuery(id+"F0.wireOp",EDGE,"E4"),sQuery(id+"F0.wireOp",EDGE,"E5"),sQuery(id+"F0.wireOp",EDGE,"E6"),sQuery(id+"F0.wireOp",EDGE,"E7"),sQuery(id+"F0.wireOp",EDGE,"E8"),sQuery(id+"F0.wireOp",EDGE,"E9"),sQuery(id+"F0.wireOp",EDGE,"E10"),sQuery(id+"F0.wireOp",EDGE,"E11"),sQuery(id+"F0.wireOp",EDGE,"E12"),sQuery(id+"F0.wireOp",EDGE,"E13"),sQuery(id+"F0.wireOp",EDGE,"E14"),sQuery(id+"F0.wireOp",EDGE,"E15"),sQuery(id+"F0.wireOp",EDGE,"E16"),sQuery(id+"F0.wireOp",EDGE,"E17"),sQuery(id+"F0.wireOp",EDGE,"E18"),sQuery(id+"F0.wireOp",EDGE,"E19"),sQuery(id+"F0.wireOp",EDGE,"E20"),sQuery(id+"F0.wireOp",EDGE,"E21"),sQuery(id+"F0.wireOp",EDGE,"E22"),sQuery(id+"F0.wireOp",EDGE,"E23"),sQuery(id+"F0.wireOp",EDGE,"E24"),sQuery(id+"F0.wireOp",EDGE,"E25"),sQuery(id+"F0.wireOp",EDGE,"E26"),sQuery(id+"F0.wireOp",EDGE,"E27"),sQuery(id+"F0.wireOp",EDGE,"E28"),sQuery(id+"F0.wireOp",EDGE,"E29"),sQuery(id+"F0.wireOp",EDGE,"E30"),sQuery(id+"F0.wireOp",EDGE,"E31"),sQuery(id+"F0.wireOp",EDGE,"E32"),sQuery(id+"F0.wireOp",EDGE,"E33"),sQuery(id+"F0.wireOp",EDGE,"E34"),sQuery(id+"F0.wireOp",EDGE,"E35"),sQuery(id+"F0.wireOp",EDGE,"E36"),sQuery(id+"F0.wireOp",EDGE,"E37"),sQuery(id+"F0.wireOp",EDGE,"E38"),sQuery(id+"F0.wireOp",EDGE,"E39"),sQuery(id+"F0.wireOp",EDGE,"E40"),sQuery(id+"F0.wireOp",EDGE,"E41"),sQuery(id+"F0.wireOp",EDGE,"E42"),sQuery(id+"F0.wireOp",EDGE,"E43"),sQuery(id+"F0.wireOp",EDGE,"E44"),sQuery(id+"F0.wireOp",EDGE,"E45"),sQuery(id+"F0.wireOp",EDGE,"E46"),sQuery(id+"F0.wireOp",EDGE,"E47"),sQuery(id+"F0.wireOp",EDGE,"E48"),sQuery(id+"F0.wireOp",EDGE,"E49"),sQuery(id+"F0.wireOp",EDGE,"E50"),sQuery(id+"F0.wireOp",EDGE,"E51"),sQuery(id+"F0.wireOp",EDGE,"E52"),sQuery(id+"F0.wireOp",EDGE,"E53"),sQuery(id+"F0.wireOp",EDGE,"E54"),sQuery(id+"F0.wireOp",EDGE,"E55"),sQuery(id+"F0.wireOp",EDGE,"E56"),sQuery(id+"F0.wireOp",EDGE,"E57"),sQuery(id+"F0.wireOp",EDGE,"E58"),sQuery(id+"F0.wireOp",EDGE,"E59"),sQuery(id+"F0.wireOp",EDGE,"E60"),sQuery(id+"F0.wireOp",EDGE,"E61"),sQuery(id+"F0.wireOp",EDGE,"E62"),sQuery(id+"F0.wireOp",EDGE,"E63"),sQuery(id+"F0.wireOp",EDGE,"E64"),sQuery(id+"F0.wireOp",EDGE,"E65"),sQuery(id+"F0.wireOp",EDGE,"E66"),sQuery(id+"F0.wireOp",EDGE,"E67"),sQuery(id+"F0.wireOp",EDGE,"E68"),sQuery(id+"F0.wireOp",EDGE,"E69"),sQuery(id+"F0.wireOp",EDGE,"E70"),sQuery(id+"F0.wireOp",EDGE,"E71"),sQuery(id+"F0.wireOp",EDGE,"E72"),sQuery(id+"F0.wireOp",EDGE,"E73"),sQuery(id+"F0.wireOp",EDGE,"E74"),sQuery(id+"F0.wireOp",EDGE,"E75"),sQuery(id+"F0.wireOp",EDGE,"E76"),sQuery(id+"F0.wireOp",EDGE,"E77"),sQuery(id+"F0.wireOp",EDGE,"E78"),sQuery(id+"F0.wireOp",EDGE,"E79"),sQuery(id+"F0.wireOp",EDGE,"E80"),sQuery(id+"F0.wireOp",EDGE,"E81"),sQuery(id+"F0.wireOp",EDGE,"E82"),sQuery(id+"F0.wireOp",EDGE,"E83"),sQuery(id+"F0.wireOp",EDGE,"E84"),sQuery(id+"F0.wireOp",EDGE,"E85"),sQuery(id+"F0.wireOp",EDGE,"E86"),sQuery(id+"F0.wireOp",EDGE,"E87"),sQuery(id+"F0.wireOp",EDGE,"E88"),sQuery(id+"F0.wireOp",EDGE,"E89"),sQuery(id+"F0.wireOp",EDGE,"E90"),sQuery(id+"F0.wireOp",EDGE,"E91"),sQuery(id+"F0.wireOp",EDGE,"E92"),sQuery(id+"F0.wireOp",EDGE,"E93"),sQuery(id+"F0.wireOp",EDGE,"E94"),sQuery(id+"F0.wireOp",EDGE,"E95"),sQuery(id+"F0.wireOp",EDGE,"E96"),sQuery(id+"F0.wireOp",EDGE,"E97"),sQuery(id+"F0.wireOp",EDGE,"E98"),sQuery(id+"F0.wireOp",EDGE,"E99"),sQuery(id+"F0.wireOp",EDGE,"E100"),sQuery(id+"F0.wireOp",EDGE,"E101"),sQuery(id+"F0.wireOp",EDGE,"E102"),sQuery(id+"F0.wireOp",EDGE,"E103"),sQuery(id+"F0.wireOp",EDGE,"E104"),sQuery(id+"F0.wireOp",EDGE,"E105"),sQuery(id+"F0.wireOp",EDGE,"E106"),sQuery(id+"F0.wireOp",EDGE,"E107"),sQuery(id+"F0.wireOp",EDGE,"E108"),sQuery(id+"F0.wireOp",EDGE,"E109"),sQuery(id+"F0.wireOp",EDGE,"E110"),sQuery(id+"F0.wireOp",EDGE,"E111"),sQuery(id+"F0.wireOp",EDGE,"E112"),sQuery(id+"F0.wireOp",EDGE,"E113"),sQuery(id+"F0.wireOp",EDGE,"E114"),sQuery(id+"F0.wireOp",EDGE,"E115"),sQuery(id+"F0.wireOp",EDGE,"E116"),sQuery(id+"F0.wireOp",EDGE,"E117"),sQuery(id+"F0.wireOp",EDGE,"E118"),sQuery(id+"F0.wireOp",EDGE,"E119"),sQuery(id+"F0.wireOp",EDGE,"E120"),sQuery(id+"F0.wireOp",EDGE,"E121"),sQuery(id+"F0.wireOp",EDGE,"E122"),sQuery(id+"F0.wireOp",EDGE,"E123"),sQuery(id+"F0.wireOp",EDGE,"E124"),sQuery(id+"F0.wireOp",EDGE,"E125"),sQuery(id+"F0.wireOp",EDGE,"E126"),sQuery(id+"F0.wireOp",EDGE,"E127"),sQuery(id+"F0.wireOp",EDGE,"E128"),sQuery(id+"F0.wireOp",EDGE,"E129"),sQuery(id+"F0.wireOp",EDGE,"E130"),sQuery(id+"F0.wireOp",EDGE,"E131"),sQuery(id+"F0.wireOp",EDGE,"E132"),sQuery(id+"F0.wireOp",EDGE,"E133"),sQuery(id+"F0.wireOp",EDGE,"E134"),sQuery(id+"F0.wireOp",EDGE,"E135"),sQuery(id+"F0.wireOp",EDGE,"E136"),sQuery(id+"F0.wireOp",EDGE,"E137"),sQuery(id+"F0.wireOp",EDGE,"E138"),sQuery(id+"F0.wireOp",EDGE,"E139"),sQuery(id+"F0.wireOp",EDGE,"E140"),sQuery(id+"F0.wireOp",EDGE,"E141"),sQuery(id+"F0.wireOp",EDGE,"E142"),sQuery(id+"F0.wireOp",EDGE,"E143"),sQuery(id+"F0.wireOp",EDGE,"E144"),sQuery(id+"F0.wireOp",EDGE,"E145"),sQuery(id+"F0.wireOp",EDGE,"E146"),sQuery(id+"F0.wireOp",EDGE,"E147"),sQuery(id+"F0.wireOp",EDGE,"E148"),sQuery(id+"F0.wireOp",EDGE,"E149"),sQuery(id+"F0.wireOp",EDGE,"E150"),sQuery(id+"F0.wireOp",EDGE,"E151"),sQuery(id+"F0.wireOp",EDGE,"E152"),sQuery(id+"F0.wireOp",EDGE,"E153"),sQuery(id+"F0.wireOp",EDGE,"E154"),sQuery(id+"F0.wireOp",EDGE,"E155"),sQuery(id+"F0.wireOp",EDGE,"E156"),sQuery(id+"F0.wireOp",EDGE,"E157"),sQuery(id+"F0.wireOp",EDGE,"E158"),sQuery(id+"F0.wireOp",EDGE,"E159"),sQuery(id+"F0.wireOp",EDGE,"E160"),sQuery(id+"F0.wireOp",EDGE,"E161"),sQuery(id+"F0.wireOp",EDGE,"E162"),sQuery(id+"F0.wireOp",EDGE,"E163"),sQuery(id+"F0.wireOp",EDGE,"E164"),sQuery(id+"F0.wireOp",EDGE,"E165"),sQuery(id+"F0.wireOp",EDGE,"E166"),sQuery(id+"F0.wireOp",EDGE,"E167"),sQuery(id+"F0.wireOp",EDGE,"E168"),sQuery(id+"F0.wireOp",EDGE,"E169"),sQuery(id+"F0.wireOp",EDGE,"E170"),sQuery(id+"F0.wireOp",EDGE,"E171"),sQuery(id+"F0.wireOp",EDGE,"E172"),sQuery(id+"F0.wireOp",EDGE,"E173"),sQuery(id+"F0.wireOp",EDGE,"E174"),sQuery(id+"F0.wireOp",EDGE,"E175"),sQuery(id+"F0.wireOp",EDGE,"E176"),sQuery(id+"F0.wireOp",EDGE,"E177"),sQuery(id+"F0.wireOp",EDGE,"E178"),sQuery(id+"F0.wireOp",EDGE,"E179"),sQuery(id+"F0.wireOp",EDGE,"E180"),sQuery(id+"F0.wireOp",EDGE,"E181"),sQuery(id+"F0.wireOp",EDGE,"E182"),sQuery(id+"F0.wireOp",EDGE,"E183"),sQuery(id+"F0.wireOp",EDGE,"E184"),sQuery(id+"F0.wireOp",EDGE,"E185"),sQuery(id+"F0.wireOp",EDGE,"E186"),sQuery(id+"F0.wireOp",EDGE,"E187"),sQuery(id+"F0.wireOp",EDGE,"E188"),sQuery(id+"F0.wireOp",EDGE,"E189"),sQuery(id+"F0.wireOp",EDGE,"E190"),sQuery(id+"F0.wireOp",EDGE,"E191"),sQuery(id+"F0.wireOp",EDGE,"E192"),sQuery(id+"F0.wireOp",EDGE,"E193"),sQuery(id+"F0.wireOp",EDGE,"E194"),sQuery(id+"F0.wireOp",EDGE,"E195"),sQuery(id+"F0.wireOp",EDGE,"E196"),sQuery(id+"F0.wireOp",EDGE,"E197"),sQuery(id+"F0.wireOp",EDGE,"E198"),sQuery(id+"F0.wireOp",EDGE,"E199"),sQuery(id+"F0.wireOp",EDGE,"E200"),sQuery(id+"F0.wireOp",EDGE,"E201"),sQuery(id+"F0.wireOp",EDGE,"E202"),sQuery(id+"F0.wireOp",EDGE,"E203"),sQuery(id+"F0.wireOp",EDGE,"E204"),sQuery(id+"F0.wireOp",EDGE,"E205"),sQuery(id+"F0.wireOp",EDGE,"E206"),sQuery(id+"F0.wireOp",EDGE,"E207"),sQuery(id+"F0.wireOp",EDGE,"E208"),sQuery(id+"F0.wireOp",EDGE,"E209"),sQuery(id+"F0.wireOp",EDGE,"E210"),sQuery(id+"F0.wireOp",EDGE,"E211"),sQuery(id+"F0.wireOp",EDGE,"E212"),sQuery(id+"F0.wireOp",EDGE,"E213"),sQuery(id+"F0.wireOp",EDGE,"E214"),sQuery(id+"F0.wireOp",EDGE,"E215"),sQuery(id+"F0.wireOp",EDGE,"E216"),sQuery(id+"F0.wireOp",EDGE,"E217"),sQuery(id+"F0.wireOp",EDGE,"E218"),sQuery(id+"F0.wireOp",EDGE,"E219"),sQuery(id+"F0.wireOp",EDGE,"E220"),sQuery(id+"F0.wireOp",EDGE,"E221"),sQuery(id+"F0.wireOp",EDGE,"E222"),sQuery(id+"F0.wireOp",EDGE,"E223"),sQuery(id+"F0.wireOp",EDGE,"E224"),sQuery(id+"F0.wireOp",EDGE,"E225"),sQuery(id+"F0.wireOp",EDGE,"E226"),sQuery(id+"F0.wireOp",EDGE,"E227"),sQuery(id+"F0.wireOp",EDGE,"E228"),sQuery(id+"F0.wireOp",EDGE,"E229"),sQuery(id+"F0.wireOp",EDGE,"E230"),sQuery(id+"F0.wireOp",EDGE,"E231"),sQuery(id+"F0.wireOp",EDGE,"E232"),sQuery(id+"F0.wireOp",EDGE,"E233"),sQuery(id+"F0.wireOp",EDGE,"E234"),sQuery(id+"F0.wireOp",EDGE,"E235"),sQuery(id+"F0.wireOp",EDGE,"E236"),sQuery(id+"F0.wireOp",EDGE,"E237"),sQuery(id+"F0.wireOp",EDGE,"E238"),sQuery(id+"F0.wireOp",EDGE,"E239"),sQuery(id+"F0.wireOp",EDGE,"E240"),sQuery(id+"F0.wireOp",EDGE,"E241"),sQuery(id+"F0.wireOp",EDGE,"E242"),sQuery(id+"F0.wireOp",EDGE,"E243"),sQuery(id+"F0.wireOp",EDGE,"E244"),sQuery(id+"F0.wireOp",EDGE,"E245"),sQuery(id+"F0.wireOp",EDGE,"E246"),sQuery(id+"F0.wireOp",EDGE,"E247"),sQuery(id+"F0.wireOp",EDGE,"E248"),sQuery(id+"F0.wireOp",EDGE,"E249"),sQuery(id+"F0.wireOp",EDGE,"E250"),sQuery(id+"F0.wireOp",EDGE,"E251"),sQuery(id+"F0.wireOp",EDGE,"E252"),sQuery(id+"F0.wireOp",EDGE,"E253"),sQuery(id+"F0.wireOp",EDGE,"E254"),sQuery(id+"F0.wireOp",EDGE,"E255"),sQuery(id+"F0.wireOp",EDGE,"E256"),sQuery(id+"F0.wireOp",EDGE,"E257"),sQuery(id+"F0.wireOp",EDGE,"E258"),sQuery(id+"F0.wireOp",EDGE,"E259"),sQuery(id+"F0.wireOp",EDGE,"E260"),sQuery(id+"F0.wireOp",EDGE,"E261"),sQuery(id+"F0.wireOp",EDGE,"E262"),sQuery(id+"F0.wireOp",EDGE,"E263"),sQuery(id+"F0.wireOp",EDGE,"E264"),sQuery(id+"F0.wireOp",EDGE,"E265"),sQuery(id+"F0.wireOp",EDGE,"E266"),sQuery(id+"F0.wireOp",EDGE,"E267"),sQuery(id+"F0.wireOp",EDGE,"E268"),sQuery(id+"F0.wireOp",EDGE,"E269"),sQuery(id+"F0.wireOp",EDGE,"E270"),sQuery(id+"F0.wireOp",EDGE,"E271"),sQuery(id+"F0.wireOp",EDGE,"E272"),sQuery(id+"F0.wireOp",EDGE,"E273"),sQuery(id+"F0.wireOp",EDGE,"E274"),sQuery(id+"F0.wireOp",EDGE,"E275"),sQuery(id+"F0.wireOp",EDGE,"E276"),sQuery(id+"F0.wireOp",EDGE,"E277"),sQuery(id+"F0.wireOp",EDGE,"E278"),sQuery(id+"F0.wireOp",EDGE,"E279"),sQuery(id+"F0.wireOp",EDGE,"E280"),sQuery(id+"F0.wireOp",EDGE,"E281"),sQuery(id+"F0.wireOp",EDGE,"E282"),sQuery(id+"F0.wireOp",EDGE,"E283"),sQuery(id+"F0.wireOp",EDGE,"E284"),sQuery(id+"F0.wireOp",EDGE,"E285"),sQuery(id+"F0.wireOp",EDGE,"E286"),sQuery(id+"F0.wireOp",EDGE,"E287"),sQuery(id+"F0.wireOp",EDGE,"E288"),sQuery(id+"F0.wireOp",EDGE,"E289"),sQuery(id+"F0.wireOp",EDGE,"E290"),sQuery(id+"F0.wireOp",EDGE,"E291"),sQuery(id+"F0.wireOp",EDGE,"E292"),sQuery(id+"F0.wireOp",EDGE,"E293"),sQuery(id+"F0.wireOp",EDGE,"E294"),sQuery(id+"F0.wireOp",EDGE,"E295"),sQuery(id+"F0.wireOp",EDGE,"E296"),sQuery(id+"F0.wireOp",EDGE,"E297"),sQuery(id+"F0.wireOp",EDGE,"E298"),sQuery(id+"F0.wireOp",EDGE,"E299"),sQuery(id+"F0.wireOp",EDGE,"E300"),sQuery(id+"F0.wireOp",EDGE,"E301"),sQuery(id+"F0.wireOp",EDGE,"E302"),sQuery(id+"F0.wireOp",EDGE,"E303"),sQuery(id+"F0.wireOp",EDGE,"E304"),sQuery(id+"F0.wireOp",EDGE,"E305"),sQuery(id+"F0.wireOp",EDGE,"E306"),sQuery(id+"F0.wireOp",EDGE,"E307"),sQuery(id+"F0.wireOp",EDGE,"E308"),sQuery(id+"F0.wireOp",EDGE,"E309"),sQuery(id+"F0.wireOp",EDGE,"E310"),sQuery(id+"F0.wireOp",EDGE,"E311"),sQuery(id+"F0.wireOp",EDGE,"E312"),sQuery(id+"F0.wireOp",EDGE,"E313"),sQuery(id+"F0.wireOp",EDGE,"E314"),sQuery(id+"F0.wireOp",EDGE,"E315"),sQuery(id+"F0.wireOp",EDGE,"E316"),sQuery(id+"F0.wireOp",EDGE,"E317"),sQuery(id+"F0.wireOp",EDGE,"E318"),sQuery(id+"F0.wireOp",EDGE,"E319"),sQuery(id+"F0.wireOp",EDGE,"E320"),sQuery(id+"F0.wireOp",EDGE,"E321"),sQuery(id+"F0.wireOp",EDGE,"E322"),sQuery(id+"F0.wireOp",EDGE,"E323"),sQuery(id+"F0.wireOp",EDGE,"E324"),sQuery(id+"F0.wireOp",EDGE,"E325"),sQuery(id+"F0.wireOp",EDGE,"E326"),sQuery(id+"F0.wireOp",EDGE,"E327"),sQuery(id+"F0.wireOp",EDGE,"E328"),sQuery(id+"F0.wireOp",EDGE,"E329"),sQuery(id+"F0.wireOp",EDGE,"E330"),sQuery(id+"F0.wireOp",EDGE,"E331"),sQuery(id+"F0.wireOp",EDGE,"E332"),sQuery(id+"F0.wireOp",EDGE,"E333"),sQuery(id+"F0.wireOp",EDGE,"E334"),sQuery(id+"F0.wireOp",EDGE,"E335"),sQuery(id+"F0.wireOp",EDGE,"E336"),sQuery(id+"F0.wireOp",EDGE,"E337"),sQuery(id+"F0.wireOp",EDGE,"E338"),sQuery(id+"F0.wireOp",EDGE,"E339"),sQuery(id+"F0.wireOp",EDGE,"E340"),sQuery(id+"F0.wireOp",EDGE,"E341"),sQuery(id+"F0.wireOp",EDGE,"E342"),sQuery(id+"F0.wireOp",EDGE,"E343"),sQuery(id+"F0.wireOp",EDGE,"E344"),sQuery(id+"F0.wireOp",EDGE,"E345"),sQuery(id+"F0.wireOp",EDGE,"E346"),sQuery(id+"F0.wireOp",EDGE,"E347"),sQuery(id+"F0.wireOp",EDGE,"E348"),sQuery(id+"F0.wireOp",EDGE,"E349"),sQuery(id+"F0.wireOp",EDGE,"E350"),sQuery(id+"F0.wireOp",EDGE,"E351"),sQuery(id+"F0.wireOp",EDGE,"E352"),sQuery(id+"F0.wireOp",EDGE,"E353"),sQuery(id+"F0.wireOp",EDGE,"E354"),sQuery(id+"F0.wireOp",EDGE,"E355"),sQuery(id+"F0.wireOp",EDGE,"E356"),sQuery(id+"F0.wireOp",EDGE,"E357"),sQuery(id+"F0.wireOp",EDGE,"E358"),sQuery(id+"F0.wireOp",EDGE,"E359"),sQuery(id+"F0.wireOp",EDGE,"E360"),sQuery(id+"F0.wireOp",EDGE,"E361"),sQuery(id+"F0.wireOp",EDGE,"E362"),sQuery(id+"F0.wireOp",EDGE,"E363"),sQuery(id+"F0.wireOp",EDGE,"E364"),sQuery(id+"F0.wireOp",EDGE,"E365"),sQuery(id+"F0.wireOp",EDGE,"E366"),sQuery(id+"F0.wireOp",EDGE,"E367"),sQuery(id+"F0.wireOp",EDGE,"E368"),sQuery(id+"F0.wireOp",EDGE,"E369"),sQuery(id+"F0.wireOp",EDGE,"E370"),sQuery(id+"F0.wireOp",EDGE,"E371"),sQuery(id+"F0.wireOp",EDGE,"E372"),sQuery(id+"F0.wireOp",EDGE,"E373"),sQuery(id+"F0.wireOp",EDGE,"E374"),sQuery(id+"F0.wireOp",EDGE,"E375"),sQuery(id+"F0.wireOp",EDGE,"E376"),sQuery(id+"F0.wireOp",EDGE,"E377"),sQuery(id+"F0.wireOp",EDGE,"E378"),sQuery(id+"F0.wireOp",EDGE,"E379"),sQuery(id+"F0.wireOp",EDGE,"E380"),sQuery(id+"F0.wireOp",EDGE,"E381"),sQuery(id+"F0.wireOp",EDGE,"E382"),sQuery(id+"F0.wireOp",EDGE,"E383"),sQuery(id+"F0.wireOp",EDGE,"E384"),sQuery(id+"F0.wireOp",EDGE,"E385"),sQuery(id+"F0.wireOp",EDGE,"E386"),sQuery(id+"F0.wireOp",EDGE,"E387"),sQuery(id+"F0.wireOp",EDGE,"E388"),sQuery(id+"F0.wireOp",EDGE,"E389"),sQuery(id+"F0.wireOp",EDGE,"E390"),sQuery(id+"F0.wireOp",EDGE,"E391"),sQuery(id+"F0.wireOp",EDGE,"E392"),sQuery(id+"F0.wireOp",EDGE,"E393"),sQuery(id+"F0.wireOp",EDGE,"E394"),sQuery(id+"F0.wireOp",EDGE,"E395"),sQuery(id+"F0.wireOp",EDGE,"E396"),sQuery(id+"F0.wireOp",EDGE,"E397"),sQuery(id+"F0.wireOp",EDGE,"E398"),sQuery(id+"F0.wireOp",EDGE,"E399"),sQuery(id+"F0.wireOp",EDGE,"E400"),sQuery(id+"F0.wireOp",EDGE,"E401"),sQuery(id+"F0.wireOp",EDGE,"E402"),sQuery(id+"F0.wireOp",EDGE,"E403"),sQuery(id+"F0.wireOp",EDGE,"E404"),sQuery(id+"F0.wireOp",EDGE,"E405"),sQuery(id+"F0.wireOp",EDGE,"E406"),sQuery(id+"F0.wireOp",EDGE,"E407"),sQuery(id+"F0.wireOp",EDGE,"E408"),sQuery(id+"F0.wireOp",EDGE,"E409"),sQuery(id+"F0.wireOp",EDGE,"E410"),sQuery(id+"F0.wireOp",EDGE,"E411"),sQuery(id+"F0.wireOp",EDGE,"E412"),sQuery(id+"F0.wireOp",EDGE,"E413"),sQuery(id+"F0.wireOp",EDGE,"E414"),sQuery(id+"F0.wireOp",EDGE,"E415"),sQuery(id+"F0.wireOp",EDGE,"E416"),sQuery(id+"F0.wireOp",EDGE,"E417"),sQuery(id+"F0.wireOp",EDGE,"E418"),sQuery(id+"F0.wireOp",EDGE,"E419"),sQuery(id+"F0.wireOp",EDGE,"E420"),sQuery(id+"F0.wireOp",EDGE,"E421"),sQuery(id+"F0.wireOp",EDGE,"E422"),sQuery(id+"F0.wireOp",EDGE,"E423"),sQuery(id+"F0.wireOp",EDGE,"E424"),sQuery(id+"F0.wireOp",EDGE,"E425"),sQuery(id+"F0.wireOp",EDGE,"E426"),sQuery(id+"F0.wireOp",EDGE,"E427"),sQuery(id+"F0.wireOp",EDGE,"E428"),sQuery(id+"F0.wireOp",EDGE,"E429"),sQuery(id+"F0.wireOp",EDGE,"E430"),sQuery(id+"F0.wireOp",EDGE,"E431"),sQuery(id+"F0.wireOp",EDGE,"E432"),sQuery(id+"F0.wireOp",EDGE,"E433"),sQuery(id+"F0.wireOp",EDGE,"E434"),sQuery(id+"F0.wireOp",EDGE,"E435"),sQuery(id+"F0.wireOp",EDGE,"E436"),sQuery(id+"F0.wireOp",EDGE,"E437"),sQuery(id+"F0.wireOp",EDGE,"E438"),sQuery(id+"F0.wireOp",EDGE,"E439"),sQuery(id+"F0.wireOp",EDGE,"E440"),sQuery(id+"F0.wireOp",EDGE,"E490"),sQuery(id+"F0.wireOp",EDGE,"E492"),sQuery(id+"F0.wireOp",EDGE,"E494"),sQuery(id+"F0.wireOp",EDGE,"E496"),sQuery(id+"F0.wireOp",EDGE,"E498"),sQuery(id+"F0.wireOp",EDGE,"E499"),sQuery(id+"F0.wireOp",EDGE,"E500"),sQuery(id+"F0.wireOp",EDGE,"E501"),sQuery(id+"F0.wireOp",EDGE,"E502"),sQuery(id+"F0.wireOp",EDGE,"E503"),sQuery(id+"F0.wireOp",EDGE,"E506")])]});
            extrude(context, id + "F11", {"entities" : qUnion([Q0]), "operationType" : NewBodyOperationType.REMOVE, "endBound" : BoundingType.THROUGH_ALL, "oppositeDirection" : true, "endBoundEntityBody" : qUnion([Q1]), "depth" : 25 * mm});
        }
    });
